FCSTD DOCUMENT  (FreeCAD 1.1R44795 (Git))
Label: Travel_buddy_V1.1
License: All rights reserved
LicenseURL: https://en.wikipedia.org/wiki/All_rights_reserved
objects: Part::Feature×201, Sketcher::SketchObject×50, App::Point×35, PartDesign::Pad×31, App::Part×21, PartDesign::Pocket×18, PartDesign::Body×14, PartDesign::Fillet×14, PartDesign::SubShapeBinder×8, PartDesign::Chamfer×6, PartDesign::Plane×3, PartDesign::LinearPattern×3, Spreadsheet::Sheet×1, PartDesign::Thickness×1, PartDesign::Revolution×1, PartDesign::Groove×1, PartDesign::FeatureBase×1, PartDesign::Boolean×1, Part::DatumPoint×1, Part::DatumPlane×1
note: 552 computed .brp shape members not serialized (recipe doc carries the construction recipe); baked Part::Feature solids carry a one-line shape summary decoded from their .brp

FEATURE [Part::Feature] Part__Feature003  label="FPC0_5K-DH-24PWB"
  Placement = pos=(129.7,-96.32,1.595) rot=(0,0,-1;1.5708rad)
  shape: bbox 5.251 x 15.51 x 3.201 mm, 2199 faces (baked)
FEATURE [Part::Feature] Part__Feature004  label="MESHTASTIC_REPEATER_HANDLE_1__1"
  shape: bbox 4.5 x 4.5 x 0.5047 mm, 32 faces (baked)
FEATURE [Part::Feature] Part__Feature005  label="MESHTASTIC_REPEATER_HANDLE_1__2"
  shape: bbox 6.901 x 4.502 x 3.811 mm, 367 faces (baked)
FEATURE [App::Part] MESHTASTIC_REPEATER_HANDLE_1_3__ASM
  Group = -> [Part__Feature004,Part__Feature005]
  Origin = -> Origin002
FEATURE [App::Part] TS4543TP_ASM
  Group = -> [MESHTASTIC_REPEATER_HANDLE_1_3__ASM]
  Origin = -> Origin003
  Placement = pos=(120.7,-117.2,1.595) rot=(0,0,-1;1.5708rad)
FEATURE [Part::Feature] Part__Feature009  label="FPC0_5K-DH-30PWB"
  Placement = pos=(112.1,-96.1,1.595) rot=(0,0,1;0rad)
  shape: bbox 18.51 x 5.251 x 3.201 mm, 2685 faces (baked)
FEATURE [Part::Feature] Part__Feature023  label="MESHTASTIC_REPEATER_HANDLE_1__3"
  shape: bbox 7.796 x 8.2 x 6.5 mm, 341 faces (baked)
FEATURE [Part::Feature] Part__Feature024  label="MESHTASTIC_REPEATER_HANDLE_1__4"
  shape: bbox 0.2041 x 0.1074 x 0.001 mm, 8 faces (baked)
FEATURE [Part::Feature] Part__Feature025  label="MESHTASTIC_REPEATER_HANDLE_1__5"
  shape: bbox 0.2106 x 0.1532 x 0.001 mm, 16 faces (baked)
FEATURE [Part::Feature] Part__Feature026  label="MESHTASTIC_REPEATER_HANDLE_1__6"
  shape: bbox 0.2041 x 0.1095 x 0.001 mm, 14 faces (baked)
FEATURE [Part::Feature] Part__Feature027  label="MESHTASTIC_REPEATER_HANDLE_1__7"
  shape: bbox 0.204 x 0.1665 x 0.001 mm, 16 faces (baked)
FEATURE [Part::Feature] Part__Feature028  label="MESHTASTIC_REPEATER_HANDLE_1__8"
  shape: bbox 0.2041 x 0.183 x 0.001 mm, 16 faces (baked)
FEATURE [Part::Feature] Part__Feature029  label="MESHTASTIC_REPEATER_HANDLE_1__9"
  shape: bbox 0.2041 x 0.1095 x 0.001 mm, 14 faces (baked)
FEATURE [Part::Feature] Part__Feature030  label="MESHTASTIC_REPEATER_HANDLE_1_10"
  shape: bbox 0.1522 x 0.1175 x 0.001 mm, 24 faces (baked)
FEATURE [Part::Feature] Part__Feature031  label="MESHTASTIC_REPEATER_HANDLE_1_11"
  shape: bbox 0.1521 x 0.09841 x 0.001 mm, 23 faces (baked)
FEATURE [Part::Feature] Part__Feature032  label="MESHTASTIC_REPEATER_HANDLE_1_12"
  shape: bbox 0.214 x 0.1394 x 0.001 mm, 17 faces (baked)
FEATURE [Part::Feature] Part__Feature033  label="MESHTASTIC_REPEATER_HANDLE_1_13"
  shape: bbox 0.2041 x 0.1095 x 0.001 mm, 14 faces (baked)
FEATURE [Part::Feature] Part__Feature034  label="MESHTASTIC_REPEATER_HANDLE_1_14"
  shape: bbox 0.204 x 0.1665 x 0.001 mm, 16 faces (baked)
FEATURE [Part::Feature] Part__Feature035  label="MESHTASTIC_REPEATER_HANDLE_1_15"
  shape: bbox 0.2041 x 0.183 x 0.001 mm, 16 faces (baked)
FEATURE [Part::Feature] Part__Feature036  label="MESHTASTIC_REPEATER_HANDLE_1_16"
  shape: bbox 0.6764 x 0.9228 x 0.00103 mm, 37 faces (baked)
FEATURE [App::Part] MESHTASTIC_REPEATER_HANDLE_1_21_ASM
  Group = -> [Part__Feature023,Part__Feature024,Part__Feature025,Part__Feature026,Part__Feature027,Part__Feature028,Part__Feature029,Part__Feature030,Part__Feature031,Part__Feature032,Part__Feature033,Part__Feature034,Part__Feature035,Part__Feature036]
  Origin = -> Origin004
FEATURE [App::Part] K1_5203UA_06_ASM  label="K1-5203UA-06_ASM"
  Group = -> [MESHTASTIC_REPEATER_HANDLE_1_21_ASM]
  Origin = -> Origin005
  Placement = pos=(131.8,-117.2,1.595) rot=(0,0,1;0.785398rad)
FEATURE [Part::Feature] Part__Feature038  label="MESHTASTIC_REPEATER_HANDLE_1_17"
  shape: bbox 9 x 3.5 x 2.5 mm, 44 faces (baked)
FEATURE [Part::Feature] Part__Feature039  label="MESHTASTIC_REPEATER_HANDLE_1_18"
  shape: bbox 9.002 x 7.602 x 6.602 mm, 126 faces (baked)
FEATURE [Part::Feature] Part__Feature040  label="MESHTASTIC_REPEATER_HANDLE_1_19"
  shape: bbox 0.1074 x 0.2041 x 0.001 mm, 8 faces (baked)
FEATURE [Part::Feature] Part__Feature041  label="MESHTASTIC_REPEATER_HANDLE_1_20"
  shape: bbox 0.1532 x 0.2106 x 0.001 mm, 16 faces (baked)
FEATURE [Part::Feature] Part__Feature042  label="MESHTASTIC_REPEATER_HANDLE_1_22"
  shape: bbox 0.1095 x 0.2041 x 0.001 mm, 14 faces (baked)
FEATURE [Part::Feature] Part__Feature043  label="MESHTASTIC_REPEATER_HANDLE_1_24"
  shape: bbox 0.1665 x 0.204 x 0.001 mm, 16 faces (baked)
FEATURE [Part::Feature] Part__Feature044  label="MESHTASTIC_REPEATER_HANDLE_1_25"
  shape: bbox 0.183 x 0.2041 x 0.001 mm, 16 faces (baked)
FEATURE [Part::Feature] Part__Feature045  label="MESHTASTIC_REPEATER_HANDLE_1_26"
  shape: bbox 0.1095 x 0.2041 x 0.001 mm, 14 faces (baked)
FEATURE [Part::Feature] Part__Feature046  label="MESHTASTIC_REPEATER_HANDLE_1_27"
  shape: bbox 0.1175 x 0.1522 x 0.001 mm, 24 faces (baked)
FEATURE [Part::Feature] Part__Feature047  label="MESHTASTIC_REPEATER_HANDLE_1_28"
  shape: bbox 0.09841 x 0.1521 x 0.001 mm, 23 faces (baked)
FEATURE [Part::Feature] Part__Feature048  label="MESHTASTIC_REPEATER_HANDLE_1_29"
  shape: bbox 0.1394 x 0.214 x 0.001 mm, 17 faces (baked)
FEATURE [Part::Feature] Part__Feature049  label="MESHTASTIC_REPEATER_HANDLE_1_30"
  shape: bbox 0.1095 x 0.2041 x 0.001 mm, 14 faces (baked)
FEATURE [Part::Feature] Part__Feature050  label="MESHTASTIC_REPEATER_HANDLE_1_31"
  shape: bbox 0.1665 x 0.204 x 0.001 mm, 16 faces (baked)
FEATURE [Part::Feature] Part__Feature051  label="MESHTASTIC_REPEATER_HANDLE_1_32"
  shape: bbox 0.183 x 0.2041 x 0.001 mm, 16 faces (baked)
FEATURE [Part::Feature] Part__Feature052  label="MESHTASTIC_REPEATER_HANDLE_1_33"
  shape: bbox 0.9228 x 0.6764 x 0.00103 mm, 37 faces (baked)
FEATURE [App::Part] MESHTASTIC_REPEATER_HANDLE_1_23_ASM
  Group = -> [Part__Feature038,Part__Feature039,Part__Feature040,Part__Feature041,Part__Feature042,Part__Feature043,Part__Feature044,Part__Feature045,Part__Feature046,Part__Feature047,Part__Feature048,Part__Feature049,Part__Feature050,Part__Feature051,Part__Feature052]
  Origin = -> Origin006
FEATURE [App::Part] SK_3245D_02_L4_ASM  label="SK-3245D-02-L4_ASM"
  Group = -> [MESHTASTIC_REPEATER_HANDLE_1_23_ASM]
  Origin = -> Origin007
  Placement = pos=(92.0567,-102.6,1.595) rot=(0,0,-1;1.5708rad)
FEATURE [Part::Feature] Part__Feature072  label="USB_C_RECEPTACLE_GCT_USB4105-_1"
  shape: bbox 0.25 x 2.4 x 0.1 mm, 6 faces (baked)
FEATURE [Part::Feature] Part__Feature073  label="USB_C_RECEPTACLE_GCT_USB4105-_2"
  shape: bbox 0.25 x 2.4 x 0.1 mm, 6 faces (baked)
FEATURE [Part::Feature] Part__Feature074  label="USB_C_RECEPTACLE_GCT_USB4105-_3"
  shape: bbox 0.25 x 1.9 x 0.1 mm, 6 faces (baked)
FEATURE [Part::Feature] Part__Feature075  label="USB_C_RECEPTACLE_GCT_USB4105-_4"
  shape: bbox 0.25 x 1.9 x 0.1 mm, 6 faces (baked)
FEATURE [Part::Feature] Part__Feature076  label="USB_C_RECEPTACLE_GCT_USB4105-_5"
  shape: bbox 0.25 x 2.4 x 0.1 mm, 6 faces (baked)
FEATURE [Part::Feature] Part__Feature077  label="USB_C_RECEPTACLE_GCT_USB4105-_6"
  shape: bbox 0.25 x 2.4 x 0.1 mm, 6 faces (baked)
FEATURE [Part::Feature] Part__Feature078  label="USB_C_RECEPTACLE_GCT_USB4105-_7"
  shape: bbox 0.25 x 1.9 x 0.1 mm, 6 faces (baked)
FEATURE [Part::Feature] Part__Feature079  label="USB_C_RECEPTACLE_GCT_USB4105-_8"
  shape: bbox 0.25 x 1.9 x 0.1 mm, 6 faces (baked)
FEATURE [Part::Feature] Part__Feature080  label="USB_C_RECEPTACLE_GCT_USB4105-_9"
  shape: bbox 4.45 x 7.05 x 3.59 mm, 69 faces (baked)
FEATURE [Part::Feature] Part__Feature081  label="USB_C_RECEPTACLE_GCT_USB4105_10"
  shape: bbox 0.2 x 0.8 x 0.12 mm, 6 faces (baked)
FEATURE [Part::Feature] Part__Feature082  label="USB_C_RECEPTACLE_GCT_USB4105_11"
  shape: bbox 0.2 x 0.8 x 0.12 mm, 6 faces (baked)
FEATURE [Part::Feature] Part__Feature083  label="USB_C_RECEPTACLE_GCT_USB4105_12"
  shape: bbox 0.2 x 0.8 x 0.12 mm, 6 faces (baked)
FEATURE [Part::Feature] Part__Feature084  label="USB_C_RECEPTACLE_GCT_USB4105_13"
  shape: bbox 0.2 x 0.8 x 0.12 mm, 6 faces (baked)
FEATURE [Part::Feature] Part__Feature085  label="USB_C_RECEPTACLE_GCT_USB4105_14"
  shape: bbox 0.2 x 0.8 x 0.12 mm, 6 faces (baked)
FEATURE [Part::Feature] Part__Feature086  label="USB_C_RECEPTACLE_GCT_USB4105_15"
  shape: bbox 0.2 x 0.8 x 0.12 mm, 6 faces (baked)
FEATURE [Part::Feature] Part__Feature087  label="USB_C_RECEPTACLE_GCT_USB4105_16"
  shape: bbox 0.2 x 0.8 x 0.12 mm, 6 faces (baked)
FEATURE [Part::Feature] Part__Feature088  label="USB_C_RECEPTACLE_GCT_USB4105_17"
  shape: bbox 0.2 x 0.8 x 0.12 mm, 6 faces (baked)
FEATURE [Part::Feature] Part__Feature089  label="USB_C_RECEPTACLE_GCT_USB4105_18"
  shape: bbox 4.47 x 7.33 x 4.26 mm, 161 faces (baked)
FEATURE [Part::Feature] Part__Feature090  label="USB_C_RECEPTACLE_GCT_USB4105_19"
  shape: bbox 0.25 x 2.4 x 0.1 mm, 6 faces (baked)
FEATURE [Part::Feature] Part__Feature091  label="USB_C_RECEPTACLE_GCT_USB4105_20"
  shape: bbox 0.25 x 2.4 x 0.1 mm, 6 faces (baked)
FEATURE [Part::Feature] Part__Feature092  label="USB_C_RECEPTACLE_GCT_USB4105_21"
  shape: bbox 0.25 x 1.9 x 0.1 mm, 6 faces (baked)
FEATURE [Part::Feature] Part__Feature093  label="USB_C_RECEPTACLE_GCT_USB4105_22"
  shape: bbox 0.25 x 1.9 x 0.1 mm, 6 faces (baked)
FEATURE [Part::Feature] Part__Feature094  label="USB_C_RECEPTACLE_GCT_USB4105_23"
  shape: bbox 0.25 x 2.4 x 0.1 mm, 6 faces (baked)
FEATURE [Part::Feature] Part__Feature095  label="USB_C_RECEPTACLE_GCT_USB4105_24"
  shape: bbox 0.25 x 2.4 x 0.1 mm, 6 faces (baked)
FEATURE [Part::Feature] Part__Feature096  label="USB_C_RECEPTACLE_GCT_USB4105_25"
  shape: bbox 0.25 x 1.9 x 0.1 mm, 6 faces (baked)
FEATURE [Part::Feature] Part__Feature097  label="USB_C_RECEPTACLE_GCT_USB4105_26"
  shape: bbox 0.25 x 1.9 x 0.1 mm, 6 faces (baked)
FEATURE [Part::Feature] Part__Feature098  label="USB_C_RECEPTACLE_GCT_USB4105_27"
  shape: bbox 4.45 x 7.05 x 3.59 mm, 69 faces (baked)
FEATURE [Part::Feature] Part__Feature099  label="USB_C_RECEPTACLE_GCT_USB4105_28"
  shape: bbox 0.2 x 0.8 x 0.12 mm, 6 faces (baked)
FEATURE [Part::Feature] Part__Feature100  label="USB_C_RECEPTACLE_GCT_USB4105_29"
  shape: bbox 0.2 x 0.8 x 0.12 mm, 6 faces (baked)
FEATURE [Part::Feature] Part__Feature101  label="USB_C_RECEPTACLE_GCT_USB4105_30"
  shape: bbox 0.2 x 0.8 x 0.12 mm, 6 faces (baked)
FEATURE [Part::Feature] Part__Feature102  label="USB_C_RECEPTACLE_GCT_USB4105_31"
  shape: bbox 0.2 x 0.8 x 0.12 mm, 6 faces (baked)
FEATURE [Part::Feature] Part__Feature103  label="USB_C_RECEPTACLE_GCT_USB4105_32"
  shape: bbox 0.2 x 0.8 x 0.12 mm, 6 faces (baked)
FEATURE [Part::Feature] Part__Feature104  label="USB_C_RECEPTACLE_GCT_USB4105_33"
  shape: bbox 0.2 x 0.8 x 0.12 mm, 6 faces (baked)
FEATURE [Part::Feature] Part__Feature105  label="USB_C_RECEPTACLE_GCT_USB4105_34"
  shape: bbox 0.2 x 0.8 x 0.12 mm, 6 faces (baked)
FEATURE [Part::Feature] Part__Feature106  label="USB_C_RECEPTACLE_GCT_USB4105_35"
  shape: bbox 0.2 x 0.8 x 0.12 mm, 6 faces (baked)
FEATURE [Part::Feature] Part__Feature107  label="USB_C_RECEPTACLE_GCT_USB4105_36"
  shape: bbox 4.47 x 7.33 x 4.26 mm, 161 faces (baked)
FEATURE [App::Part] USB_C_RECEPTACLE_GCT_USB4105_XX_ASM  label="USB_C_RECEPTACLE_GCT_USB4105-XX_ASM"
  Group = -> [Part__Feature072,Part__Feature073,Part__Feature074,Part__Feature075,Part__Feature076,Part__Feature077,Part__Feature078,Part__Feature079,Part__Feature080,Part__Feature081,Part__Feature082,Part__Feature083,Part__Feature084,Part__Feature085,Part__Feature086,Part__Feature087,Part__Feature088,Part__Feature089,Part__Feature090,Part__Feature091,Part__Feature092,Part__Feature093,Part__Feature094,+13 more]
  Origin = -> Origin009
  Placement = pos=(92.8,-116.7,1.595) rot=(0,0,-1;1.5708rad)
FEATURE [Part::Feature] Part__Feature108  label="S2B-PH-SM4-TB-2_0-BAT_1"
  shape: bbox 0.5 x 3.45 x 7.65 mm, 21 faces (baked)
FEATURE [Part::Feature] Part__Feature109  label="S2B-PH-SM4-TB-2_0-BAT_2"
  shape: bbox 0.5 x 3.45 x 7.65 mm, 21 faces (baked)
FEATURE [Part::Feature] Part__Feature110  label="S2B-PH-SM4-TB-2_0-BAT_3"
  shape: bbox 0.4 x 2.2 x 2.9 mm, 16 faces (baked)
FEATURE [Part::Feature] Part__Feature111  label="S2B-PH-SM4-TB-2_0-BAT_4"
  shape: bbox 7.9 x 5.5 x 7.6 mm, 88 faces (baked)
FEATURE [Part::Feature] Part__Feature112  label="S2B-PH-SM4-TB-2_0-BAT_5"
  shape: bbox 0.4 x 2.2 x 2.9 mm, 16 faces (baked)
FEATURE [App::Part] S2B_PH_SM4_TB_2_0_BAT_ASM  label="S2B-PH-SM4-TB-2_0-BAT_ASM"
  Group = -> [Part__Feature108,Part__Feature109,Part__Feature110,Part__Feature111,Part__Feature112]
  Origin = -> Origin010
  Placement = pos=(98.9,-131.3,1.595) rot=(1,0,0;1.5708rad)
FEATURE [Part::Feature] Part__Feature114  label="MESHTASTIC_REPEATER_HANDLE_1_34"
  shape: bbox 7 x 3.7 x 4.257 mm, 143 faces (baked)
FEATURE [Part::Feature] Part__Feature115  label="MESHTASTIC_REPEATER_HANDLE_1_35"
  shape: bbox 7.801 x 1.101 x 3.501 mm, 292 faces (baked)
FEATURE [App::Part] MESHTASTIC_REPEATER_HANDLE_1_43_ASM
  Group = -> [Part__Feature114,Part__Feature115]
  Origin = -> Origin011
FEATURE [App::Part] K2_1112SA_A4DW_01_ASM  label="K2-1112SA-A4DW-01_ASM"
  Group = -> [MESHTASTIC_REPEATER_HANDLE_1_43_ASM]
  Origin = -> Origin012
  Placement = pos=(91.735,-93,1.595) rot=(0,0,1;1.5708rad)
FEATURE [Part::Feature] Part__Feature118  label="320110032_GROVE--WOSHI"
  Placement = pos=(126.1,-130.939,1.595) rot=(0,0,-1;1.5708rad)
  shape: bbox 11.9 x 10.5 x 5.2 mm, 137 faces (baked)
FEATURE [Part::Feature] Part__Feature236  label="MESHTASTIC_REPEATER_HANDLE_1_036"
  shape: bbox 0.1522 x 0.1175 x 0.001 mm, 24 faces (baked)
FEATURE [App::Part] __25_2A_WT_ASM  label="1_25-2A-WT_ASM"
  Group = -> [Part__Feature236]
  Origin = -> Origin028
  Placement = pos=(98.9,-128.5,-0.085) rot=(0,1,0;3.14159rad)
FEATURE [Part::Feature] Part__Feature258  label="U_FL-R-SMT-1"
  Placement = pos=(155.43,-85.97,-22.585) rot=(0,0.707107,0.707107;3.14159rad)
  shape: bbox 3 x 3.1 x 1.254 mm, 59 faces (baked)
FEATURE [Part::Feature] Part__Feature318  label="MESHTASTIC_REPEATER_HANDLE_1_037"
  shape: bbox 9 x 3.5 x 2.5 mm, 44 faces (baked)
FEATURE [App::Part] MLT_8530_ASM  label="MLT-8530_ASM"
  Group = -> [Part__Feature318]
  Origin = -> Origin034
  Placement = pos=(132.4,-120.2,-0.085) rot=(0.707107,-0.707107,0;3.14159rad)
FEATURE [Part::Feature] Part__Feature343  label="MESHTASTIC_REPEATER_HAND-335774"
  shape: bbox 11.6 x 11 x 0.7984 mm, 32 faces (baked)
FEATURE [Part::Feature] Part__Feature344  label="MESHTASTIC_REPEATER_HAND-336798"
  shape: bbox 3.1 x 3 x 1.26 mm, 121 faces (baked)
FEATURE [Part::Feature] Part__Feature345  label="MESHTASTIC_REPEATER_HAND-340261"
  shape: bbox 11.3 x 10.1 x 2.15 mm, 59 faces (baked)
FEATURE [App::Part] WIO_SX1262_ASM  label="WIO-SX1262_ASM"
  Group = -> [Part__Feature343,Part__Feature344,Part__Feature345]
  Origin = -> Origin038
  Placement = pos=(115.729,-94.5,-0.085) rot=(1,0,0;3.14159rad)
FEATURE [Part::Feature] Part__Feature1355  label="MESHTASTIC_REPEATER_HANDLE_SILK"
  shape: bbox 48.07 x 52 x 1.66 mm, 604 faces, 0 solids (baked)
FEATURE [Part::Feature] Part__Feature1356  label="MESHTASTIC_REPEATER_HANDLE_PCB"
  shape: bbox 48.07 x 52 x 5.31 mm, 248 faces (baked)
FEATURE [App::Part] MESHTASTIC_REPEATER_HANDLE_1_ASM  label="Wio_tracker_L1-MinimalStep"
  Group = -> [Part__Feature003,TS4543TP_ASM,Part__Feature009,K1_5203UA_06_ASM,SK_3245D_02_L4_ASM,USB_C_RECEPTACLE_GCT_USB4105_XX_ASM,S2B_PH_SM4_TB_2_0_BAT_ASM,K2_1112SA_A4DW_01_ASM,Part__Feature118,__25_2A_WT_ASM,Part__Feature258,MLT_8530_ASM,WIO_SX1262_ASM,Part__Feature1355,Part__Feature1356]
  Origin = -> Origin052
  Placement = pos=(124.75,-5.55,-136.35) rot=(0,-0.707107,0.707107;3.14159rad)
FEATURE [Spreadsheet::Sheet] Spreadsheet
  cells = A1='General; C1='Solar panel; E1='GPS antenna; G1='Keypad; A2(Tolerance)=0.2; C2(Solar_panel_x)=69; E2(GPS_ant_Size)=15; G2(KPD_x_ofset)=6; A3(Wall)=1.5; C3(Solar_panel_y)=110; G3(KPD_y_ofset)=10; A4(Fillet)=2; A5(body_height)==17 + Wall; G5(KPD_x_grid)=20; G6(KPD_y_grid)=15; A7(twoM_holes_thread)=1.7; A8(threeM_holes_thread)=2.7; G8(KPD_tab_length)==KPD_x_grid - 7; A9(threeM_holes_slip_fit)=3.2; G9(KPD_tab_margin_sides)=1; G10(KPD_tab_margin_bottom)=1.5; A11(Mounting_height)==body_height - Wall; A15(EINKfoam)=2.7
FEATURE [Part::Feature] Part__Feature  label="Choc_V1"
  Placement = pos=(108.835,-85.6907,1.595) rot=(0,0,1;0rad)
  shape: bbox 15 x 15 x 11.08 mm, 495 faces, 5 solids (baked)
FEATURE [Part::Feature] Part__Feature1442  label="Choc_V002"
  Placement = pos=(90.8431,-85.6984,1.595) rot=(0,0,1;0rad)
  shape: bbox 15 x 15 x 11.08 mm, 495 faces, 5 solids (baked)
FEATURE [Part::Feature] Part__Feature1443  label="Choc_V003"
  Placement = pos=(72.8446,-102.701,1.595) rot=(0,0,1;0rad)
  shape: bbox 15 x 15 x 11.08 mm, 495 faces, 5 solids (baked)
FEATURE [Part::Feature] Part__Feature1444  label="Choc_V004"
  Placement = pos=(72.85,-68.7,1.595) rot=(0,0,1;0rad)
  shape: bbox 15 x 15 x 11.08 mm, 495 faces, 5 solids (baked)
FEATURE [Part::Feature] Part__Feature1445  label="PinHeader_1x03_P2.54mm_Vertical"
  Placement = pos=(133.2,-50.97,1.595) rot=(0,0,1;0rad)
  shape: bbox 2.54 x 7.62 x 11.54 mm, 76 faces (baked)
FEATURE [Part::Feature] Part__Feature1446  label="Choc_V005"
  Placement = pos=(72.8454,-85.7013,1.595) rot=(0,0,1;0rad)
  shape: bbox 15 x 15 x 11.08 mm, 495 faces, 5 solids (baked)
FEATURE [Part::Feature] Part__Feature1447  label="Choc_V006"
  Placement = pos=(90.8449,-102.697,1.595) rot=(0,0,1;0rad)
  shape: bbox 15 x 15 x 11.08 mm, 495 faces, 5 solids (baked)
FEATURE [Part::Feature] Part__Feature1448  label="Choc_V007"
  Placement = pos=(126.847,-85.6531,1.595) rot=(0,0,1;0rad)
  shape: bbox 15 x 15 x 11.08 mm, 495 faces, 5 solids (baked)
FEATURE [Part::Feature] Part__Feature1449  label="Choc_V008"
  Placement = pos=(126.864,-102.697,1.595) rot=(0,0,1;0rad)
  shape: bbox 15 x 15 x 11.08 mm, 495 faces, 5 solids (baked)
FEATURE [Part::Feature] Part__Feature1450  label="Choc_V009"
  Placement = pos=(126.849,-68.7,1.595) rot=(0,0,1;0rad)
  shape: bbox 15 x 15 x 11.08 mm, 495 faces, 5 solids (baked)
FEATURE [Part::Feature] Part__Feature1451  label="Choc_V010"
  Placement = pos=(108.843,-68.7,1.595) rot=(0,0,1;0rad)
  shape: bbox 15 x 15 x 11.08 mm, 495 faces, 5 solids (baked)
FEATURE [Part::Feature] Part__Feature1452  label="Choc_V011"
  Placement = pos=(90.8359,-68.7,1.595) rot=(0,0,1;0rad)
  shape: bbox 15 x 15 x 11.08 mm, 495 faces, 5 solids (baked)
FEATURE [Part::Feature] Part__Feature1453  label="Choc_V012"
  Placement = pos=(108.838,-102.697,1.595) rot=(0,0,1;0rad)
  shape: bbox 15 x 15 x 11.08 mm, 495 faces, 5 solids (baked)
FEATURE [Part::Feature] Part__Feature1454  label="C_0805_2012Metric"
  Placement = pos=(99.7,-53.45,-0.085) rot=(0.707107,-0.707107,0;3.14159rad)
  shape: bbox 1.25 x 2 x 1.25 mm, 28 faces (baked)
FEATURE [Part::Feature] Part__Feature1455  label="D_SOD-323"
  Placement = pos=(98.8,-82.95,-0.085) rot=(0.707107,-0.707107,0;3.14159rad)
  shape: bbox 1.25 x 2.5 x 1.11 mm, 59 faces (baked)
FEATURE [Part::Feature] Part__Feature1456  label="D_SOD-324"
  Placement = pos=(116.8,-65.95,-0.085) rot=(0.707107,-0.707107,0;3.14159rad)
  shape: bbox 1.25 x 2.5 x 1.11 mm, 59 faces (baked)
FEATURE [Part::Feature] Part__Feature1457  label="D_SOD-325"
  Placement = pos=(130.8,-79.55,-0.085) rot=(0,1,0;3.14159rad)
  shape: bbox 2.5 x 1.25 x 1.11 mm, 59 faces (baked)
FEATURE [Part::Feature] Part__Feature1458  label="D_SOD-326"
  Placement = pos=(116.816,-99.9438,-0.085) rot=(0.707107,-0.707107,0;3.14159rad)
  shape: bbox 1.25 x 2.5 x 1.11 mm, 59 faces (baked)
FEATURE [Part::Feature] Part__Feature1459  label="R_0805_2012Metric"
  Placement = pos=(129.499,-50.9679,-0.085) rot=(0,1,0;3.14159rad)
  shape: bbox 2 x 1.2 x 0.45 mm, 26 faces (baked)
FEATURE [Part::Feature] Part__Feature1460  label="D_SOD-327"
  Placement = pos=(130.813,-96.557,-0.085) rot=(0,1,0;3.14159rad)
  shape: bbox 2.5 x 1.25 x 1.11 mm, 59 faces (baked)
FEATURE [Part::Feature] Part__Feature1461  label="C_0805_2012Metric001"
  Placement = pos=(95.6851,-53.3637,-0.085) rot=(0.707107,0.707107,0;3.14159rad)
  shape: bbox 1.25 x 2 x 1.25 mm, 28 faces (baked)
FEATURE [Part::Feature] Part__Feature1462  label="C_0805_2012Metric002"
  Placement = pos=(90.3,-50.75,-0.085) rot=(0.707107,0.707107,0;3.14159rad)
  shape: bbox 1.25 x 2 x 1.25 mm, 28 faces (baked)
FEATURE [Part::Feature] Part__Feature1463  label="C_0805_2012Metric003"
  Placement = pos=(101.8,-53.45,-0.085) rot=(0.707107,-0.707107,0;3.14159rad)
  shape: bbox 1.25 x 2 x 1.25 mm, 28 faces (baked)
FEATURE [Part::Feature] Part__Feature1464  label="SOT-23"
  Placement = pos=(92.5,-53.35,-0.085) rot=(0,1,0;3.14159rad)
  shape: bbox 2.5 x 3 x 1.2 mm, 69 faces (baked)
FEATURE [Part::Feature] Part__Feature1465  label="R_0805_2012Metric001"
  Placement = pos=(129.5,-53.5112,-0.085) rot=(0,1,0;3.14159rad)
  shape: bbox 2 x 1.2 x 0.45 mm, 26 faces (baked)
FEATURE [Part::Feature] Part__Feature1466  label="D_SOD-328"
  Placement = pos=(80.8,-82.95,-0.085) rot=(0.707107,-0.707107,0;3.14159rad)
  shape: bbox 1.25 x 2.5 x 1.11 mm, 59 faces (baked)
FEATURE [Part::Feature] Part__Feature1467  label="JST_PH_S4B-PH-K_1x04_P2.00mm_Horizontal"
  Placement = pos=(75.3,-52.2,-0.085) rot=(1,0,0;3.14159rad)
  shape: bbox 9.9 x 7.6 x 8.25 mm, 174 faces (baked)
FEATURE [Part::Feature] Part__Feature1468  label="D_SOD-329"
  Placement = pos=(80.8,-99.95,-0.085) rot=(0.707107,-0.707107,0;3.14159rad)
  shape: bbox 1.25 x 2.5 x 1.11 mm, 59 faces (baked)
FEATURE [Part::Feature] Part__Feature1469  label="D_SOD-330"
  Placement = pos=(98.8,-99.95,-0.085) rot=(0.707107,-0.707107,0;3.14159rad)
  shape: bbox 1.25 x 2.5 x 1.11 mm, 59 faces (baked)
FEATURE [Part::Feature] Part__Feature1470  label="SOIC-20W_7.5x12.8mm_P1.27mm"
  Placement = pos=(109.7,-53.45,-0.085) rot=(0.707107,-0.707107,0;3.14159rad)
  shape: bbox 12.8 x 10.3 x 2.75 mm, 327 faces (baked)
FEATURE [Part::Feature] Part__Feature1471  label="D_SOD-331"
  Placement = pos=(116.8,-82.95,-0.085) rot=(0.707107,-0.707107,0;3.14159rad)
  shape: bbox 1.25 x 2.5 x 1.11 mm, 59 faces (baked)
FEATURE [Part::Feature] Part__Feature1472  label="D_SOD-332"
  Placement = pos=(98.8,-65.95,-0.085) rot=(0.707107,-0.707107,0;3.14159rad)
  shape: bbox 1.25 x 2.5 x 1.11 mm, 59 faces (baked)
FEATURE [Part::Feature] Part__Feature1473  label="D_SOD-333"
  Placement = pos=(130.8,-62.55,-0.085) rot=(0,1,0;3.14159rad)
  shape: bbox 2.5 x 1.25 x 1.11 mm, 59 faces (baked)
FEATURE [Part::Feature] Part__Feature1474  label="D_SOD-334"
  Placement = pos=(80.8,-65.95,-0.085) rot=(0.707107,-0.707107,0;3.14159rad)
  shape: bbox 1.25 x 2.5 x 1.11 mm, 59 faces (baked)
FEATURE [Part::Feature] Part__Feature1475  label="T9_keyboard_PCB"
  shape: bbox 70.5 x 65.3 x 1.51 mm, 85 faces (baked)
FEATURE [App::Part] T9_keyboard_1  label="T9_keyboard-Choco_switches-V0"
  Group = -> [Part__Feature,Part__Feature1442,Part__Feature1443,Part__Feature1444,Part__Feature1445,Part__Feature1446,Part__Feature1447,Part__Feature1448,Part__Feature1449,Part__Feature1450,Part__Feature1451,Part__Feature1452,Part__Feature1453,Part__Feature1454,Part__Feature1455,Part__Feature1456,Part__Feature1457,Part__Feature1458,Part__Feature1459,Part__Feature1460,Part__Feature1461,Part__Feature1462,+13 more]
  Origin = -> Origin068
  Placement = pos=(-99,-14.5,99.5) rot=(1,0,0;1.5708rad)
FEATURE [Sketcher::SketchObject] Sketch
  ArcFitTolerance = 1e-06
  AttachmentSupport = -> [XZ_Plane067]
  ExternalTypes = [0]
  FullyConstrained = true
  MakeInternals = false
  MapMode = 5
  Placement = pos=(0,0,0) rot=(1,0,0;1.5708rad)
  _ExternalGeoVersion = 0
  sketch-geometry (5):
    g0: LineSegment StartX=-34.5 StartY=-55 StartZ=0 EndX=34.5 EndY=-55 EndZ=0
    g1: LineSegment StartX=34.5 StartY=-55 StartZ=0 EndX=34.5 EndY=55 EndZ=0
    g2: LineSegment StartX=34.5 StartY=55 StartZ=0 EndX=-34.5 EndY=55 EndZ=0
    g3: LineSegment StartX=-34.5 StartY=55 StartZ=0 EndX=-34.5 EndY=-55 EndZ=0
    g4: GeomPoint [constr] X=0 Y=0 Z=0
  constraints (12):
    c: Coincident(g0,g1)
    c: Coincident(g1,g2)
    c: Coincident(g2,g3)
    c: Coincident(g3,g0)
    c: Horizontal(g0)
    c: Horizontal(g2)
    c: Vertical(g1)
    c: Vertical(g3)
    c: Symmetric(g2,g0,g4)
    c: Distance(g1,g3) = 69
    c: Distance(g0,g2) = 110
    c: Coincident(g4,g-1)
FEATURE [PartDesign::Pad] Pad
  Direction = (0,-1,2e-16)
  Length = 2.2
  Length2 = 10
  Placement = pos=(0,0,0) rot=(1,0,0;1.5708rad)
  Profile = -> Sketch
  ReferenceAxis = -> Sketch [N_Axis]
  Refine = true
  Reversed = true
  SideType = 0
  Suppressed = false
  Type = 0
  Type2 = 0
FEATURE [PartDesign::Body] Body  label="Solar_panel"
  AllowCompound = false
  Group = -> [Sketch,Pad]
  Origin = -> Origin
  Tip = -> Pad
FEATURE [Part::Feature] Part__Feature1476  label="D_SOD-335"
  Placement = pos=(165.1,-90,1.595) rot=(0,0,1;0rad)
  shape: bbox 2.5 x 1.25 x 1.11 mm, 59 faces (baked)
FEATURE [Part::Feature] Part__Feature1477  label="D_SOD-336"
  Placement = pos=(118.9,-130,1.595) rot=(0,0,1;3.14159rad)
  shape: bbox 2.5 x 1.25 x 1.11 mm, 59 faces (baked)
FEATURE [Part::Feature] Part__Feature1478  label="D_SOD-337"
  Placement = pos=(165.1,-130,1.595) rot=(0,0,1;0rad)
  shape: bbox 2.5 x 1.25 x 1.11 mm, 59 faces (baked)
FEATURE [Part::Feature] Part__Feature1479  label="C_0805_2012Metric004"
  Placement = pos=(145.7,-90.8,1.595) rot=(0,0,1;1.5708rad)
  shape: bbox 1.25 x 2 x 1.25 mm, 28 faces (baked)
FEATURE [Part::Feature] Part__Feature1480  label="SW_Push_1P1T_XKB_TS-1187A"
  Placement = pos=(122,-66,1.595) rot=(0,0,1;0rad)
  shape: bbox 6.5 x 5.1 x 1.4 mm, 132 faces, 10 solids (baked)
FEATURE [Part::Feature] Part__Feature1481  label="SW_Push_1P1T_XKB_TS-1187A001"
  Placement = pos=(142,-126,1.595) rot=(0,0,1;0rad)
  shape: bbox 6.5 x 5.1 x 1.4 mm, 132 faces, 10 solids (baked)
FEATURE [Part::Feature] Part__Feature1482  label="D_SOD-338"
  Placement = pos=(118.9,-110,1.595) rot=(0,0,1;3.14159rad)
  shape: bbox 2.5 x 1.25 x 1.11 mm, 59 faces (baked)
FEATURE [Part::Feature] Part__Feature1483  label="R_0805_2012Metric002"
  Placement = pos=(160.9,-97.2,1.595) rot=(0,0,1;3.14159rad)
  shape: bbox 2 x 1.2 x 0.45 mm, 26 faces (baked)
FEATURE [Part::Feature] Part__Feature1484  label="D_SOD-339"
  Placement = pos=(137.1,-88.45,1.595) rot=(0,0,-1;1.5708rad)
  shape: bbox 1.25 x 2.5 x 1.11 mm, 59 faces (baked)
FEATURE [Part::Feature] Part__Feature1485  label="D_SOD-340"
  Placement = pos=(136.9,-128.4,1.595) rot=(0,0,-1;1.5708rad)
  shape: bbox 1.25 x 2.5 x 1.11 mm, 59 faces (baked)
FEATURE [Part::Feature] Part__Feature1486  label="D_SOD-341"
  Placement = pos=(139,-70.6,1.595) rot=(0,0,-1;1.5708rad)
  shape: bbox 1.25 x 2.5 x 1.11 mm, 59 faces (baked)
FEATURE [Part::Feature] Part__Feature1487  label="SW_Push_1P1T_XKB_TS-1187A002"
  Placement = pos=(162,-106,1.595) rot=(0,0,1;0rad)
  shape: bbox 6.5 x 5.1 x 1.4 mm, 132 faces, 10 solids (baked)
FEATURE [Part::Feature] Part__Feature1488  label="SOT-024"
  Placement = pos=(151.7,-95.55,1.595) rot=(0,0,1;3.14159rad)
  shape: bbox 2.5 x 3 x 1.2 mm, 69 faces (baked)
FEATURE [Part::Feature] Part__Feature1489  label="D_SOD-342"
  Placement = pos=(139,-110.6,1.595) rot=(0,0,-1;1.5708rad)
  shape: bbox 1.25 x 2.5 x 1.11 mm, 59 faces (baked)
FEATURE [Part::Feature] Part__Feature1490  label="SW_Push_1P1T_XKB_TS-1187A003"
  Placement = pos=(122,-126,1.595) rot=(0,0,1;0rad)
  shape: bbox 6.5 x 5.1 x 1.4 mm, 132 faces, 10 solids (baked)
FEATURE [Part::Feature] Part__Feature1491  label="SW_Push_1P1T_XKB_TS-1187A004"
  Placement = pos=(122,-106,1.595) rot=(0,0,1;0rad)
  shape: bbox 6.5 x 5.1 x 1.4 mm, 132 faces, 10 solids (baked)
FEATURE [Part::Feature] Part__Feature1493  label="D_SOD-343"
  Placement = pos=(118.9,-90,1.595) rot=(0,0,1;3.14159rad)
  shape: bbox 2.5 x 1.25 x 1.11 mm, 59 faces (baked)
FEATURE [Part::Feature] Part__Feature1494  label="SW_Push_1P1T_XKB_TS-1187A005"
  Placement = pos=(142,-86,1.595) rot=(0,0,1;0rad)
  shape: bbox 6.5 x 5.1 x 1.4 mm, 132 faces, 10 solids (baked)
FEATURE [Part::Feature] Part__Feature1495  label="SW_Push_1P1T_XKB_TS-1187A006"
  Placement = pos=(122,-86,1.595) rot=(0,0,1;0rad)
  shape: bbox 6.5 x 5.1 x 1.4 mm, 132 faces, 10 solids (baked)
FEATURE [Part::Feature] Part__Feature1496  label="D_SOD-344"
  Placement = pos=(165.1,-70,1.595) rot=(0,0,1;0rad)
  shape: bbox 2.5 x 1.25 x 1.11 mm, 59 faces (baked)
FEATURE [Part::Feature] Part__Feature1497  label="C_0805_2012Metric005"
  Placement = pos=(147.7,-90.3,1.595) rot=(0,0,1;1.5708rad)
  shape: bbox 1.25 x 2 x 1.25 mm, 28 faces (baked)
FEATURE [Part::Feature] Part__Feature1498  label="D_SOD-345"
  Placement = pos=(118.9,-70,1.595) rot=(0,0,1;3.14159rad)
  shape: bbox 2.5 x 1.25 x 1.11 mm, 59 faces (baked)
FEATURE [Part::Feature] Part__Feature1499  label="SW_Push_1P1T_XKB_TS-1187A007"
  Placement = pos=(162,-66,1.595) rot=(0,0,1;0rad)
  shape: bbox 6.5 x 5.1 x 1.4 mm, 132 faces, 10 solids (baked)
FEATURE [Part::Feature] Part__Feature1500  label="C_0805_2012Metric006"
  Placement = pos=(151.6,-98.45,1.595) rot=(0,0,1;0rad)
  shape: bbox 2 x 1.25 x 1.25 mm, 28 faces (baked)
FEATURE [Part::Feature] Part__Feature1501  label="D_SOD-346"
  Placement = pos=(165.1,-110,1.595) rot=(0,0,1;0rad)
  shape: bbox 2.5 x 1.25 x 1.11 mm, 59 faces (baked)
FEATURE [Part::Feature] Part__Feature1502  label="SW_Push_1P1T_XKB_TS-1187A008"
  Placement = pos=(142,-66,1.595) rot=(0,0,1;0rad)
  shape: bbox 6.5 x 5.1 x 1.4 mm, 132 faces, 10 solids (baked)
FEATURE [Part::Feature] Part__Feature1503  label="C_0805_2012Metric007"
  Placement = pos=(154.8,-95.65,1.595) rot=(0,0,-1;1.5708rad)
  shape: bbox 1.25 x 2 x 1.25 mm, 28 faces (baked)
FEATURE [Part::Feature] Part__Feature1504  label="SW_Push_1P1T_XKB_TS-1187A009"
  Placement = pos=(162,-86,1.595) rot=(0,0,1;0rad)
  shape: bbox 6.5 x 5.1 x 1.4 mm, 132 faces, 10 solids (baked)
FEATURE [Part::Feature] Part__Feature1505  label="SW_Push_1P1T_XKB_TS-1187A010"
  Placement = pos=(162,-126,1.595) rot=(0,0,1;0rad)
  shape: bbox 6.5 x 5.1 x 1.4 mm, 132 faces, 10 solids (baked)
FEATURE [Part::Feature] Part__Feature1506  label="SW_Push_1P1T_XKB_TS-1187A011"
  Placement = pos=(142,-106,1.595) rot=(0,0,1;0rad)
  shape: bbox 6.5 x 5.1 x 1.4 mm, 132 faces, 10 solids (baked)
FEATURE [Part::Feature] Part__Feature1507  label="R_0805_2012Metric003"
  Placement = pos=(160.9,-95.1,1.595) rot=(0,0,1;3.14159rad)
  shape: bbox 2 x 1.2 x 0.45 mm, 26 faces (baked)
FEATURE [Part::Feature] Part__Feature1508  label="JST_PH_S4B-PH-K_1x04_P2.00mm_Horizontal001"
  Placement = pos=(146.6,-100.65,-0.085) rot=(1,0,0;3.14159rad)
  shape: bbox 9.9 x 7.6 x 8.25 mm, 174 faces (baked)
FEATURE [Part::Feature] Part__Feature1509  label="T9_keyboard_PCB001"
  shape: bbox 50.6 x 70 x 1.51 mm, 13 faces (baked)
FEATURE [App::Part] T9_keyboard_002  label="T9_keyboard-MicroSwitches-V1"
  Group = -> [Part__Feature1476,Part__Feature1477,Part__Feature1478,Part__Feature1479,Part__Feature1480,Part__Feature1481,Part__Feature1482,Part__Feature1483,Part__Feature1484,Part__Feature1485,Part__Feature1486,Part__Feature1487,Part__Feature1488,Part__Feature1489,Part__Feature1490,Part__Feature1491,Part__Feature1493,Part__Feature1494,Part__Feature1495,Part__Feature1496,Part__Feature1497,Part__Feature1498,+11 more]
  Origin = -> Origin069
  Placement = pos=(136,-13.05,-77) rot=(0,-0.707107,0.707107;3.14159rad)
FEATURE [Sketcher::SketchObject] Sketch007
  ArcFitTolerance = 1e-06
  AttachmentSupport = -> [XZ_Plane067]
  ExternalTypes = [0]
  FullyConstrained = true
  MakeInternals = false
  MapMode = 5
  Placement = pos=(0,0,0) rot=(1,0,0;1.5708rad)
  _ExternalGeoVersion = 0
  sketch-geometry (5):
    g0: LineSegment StartX=-17.25 StartY=-26.25 StartZ=0 EndX=17.25 EndY=-26.25 EndZ=0
    g1: LineSegment StartX=17.25 StartY=-26.25 StartZ=0 EndX=17.25 EndY=26.25 EndZ=0
    g2: LineSegment StartX=17.25 StartY=26.25 StartZ=0 EndX=-17.25 EndY=26.25 EndZ=0
    g3: LineSegment StartX=-17.25 StartY=26.25 StartZ=0 EndX=-17.25 EndY=-26.25 EndZ=0
    g4: GeomPoint [constr] X=0 Y=0 Z=0
  constraints (12):
    c: Coincident(g0,g1)
    c: Coincident(g1,g2)
    c: Coincident(g2,g3)
    c: Coincident(g3,g0)
    c: Horizontal(g0)
    c: Horizontal(g2)
    c: Vertical(g1)
    c: Vertical(g3)
    c: Symmetric(g2,g0,g4)
    c: Distance(g1,g3) = 34.5
    c: Distance(g0,g2) = 52.5
    c: Coincident(g4,g-1)
FEATURE [PartDesign::Pad] Pad006
  Direction = (0,-1,2e-16)
  Length = 10.3
  Length2 = 10
  Placement = pos=(0,0,0) rot=(1,0,0;1.5708rad)
  Profile = -> Sketch007
  ReferenceAxis = -> Sketch007 [N_Axis]
  Refine = true
  SideType = 0
  Suppressed = false
  Type = 0
  Type2 = 0
FEATURE [PartDesign::Body] Body003  label="Proposed Battery"
  AllowCompound = false
  Group = -> [Sketch007,Pad006]
  Origin = -> Origin073
  Placement = pos=(16.2,-1.65,27.1) rot=(0,-1,0;3.14159rad)
  Tip = -> Pad006
FEATURE [Sketcher::SketchObject] Sketch008
  ArcFitTolerance = 1e-06
  AttachmentSupport = -> [XZ_Plane067]
  ExternalTypes = [0]
  FullyConstrained = true
  MakeInternals = false
  MapMode = 5
  Placement = pos=(0,0,0) rot=(1,0,0;1.5708rad)
  _ExternalGeoVersion = 0
  sketch-geometry (5):
    g0: LineSegment StartX=-30 StartY=-25 StartZ=0 EndX=30 EndY=-25 EndZ=0
    g1: LineSegment StartX=30 StartY=-25 StartZ=0 EndX=30 EndY=25 EndZ=0
    g2: LineSegment StartX=30 StartY=25 StartZ=0 EndX=-30 EndY=25 EndZ=0
    g3: LineSegment StartX=-30 StartY=25 StartZ=0 EndX=-30 EndY=-25 EndZ=0
    g4: GeomPoint [constr] X=0 Y=0 Z=0
  constraints (12):
    c: Coincident(g0,g1)
    c: Coincident(g1,g2)
    c: Coincident(g2,g3)
    c: Coincident(g3,g0)
    c: Horizontal(g0)
    c: Horizontal(g2)
    c: Vertical(g1)
    c: Vertical(g3)
    c: Symmetric(g2,g0,g4)
    c: Distance(g1,g3) = 60
    c: Distance(g0,g2) = 50
    c: Coincident(g4,g-1)
FEATURE [PartDesign::Pad] Pad007
  Direction = (0,-1,2e-16)
  Length = 6
  Length2 = 10
  Placement = pos=(0,0,0) rot=(1,0,0;1.5708rad)
  Profile = -> Sketch008
  ReferenceAxis = -> Sketch008 [N_Axis]
  Refine = true
  SideType = 0
  Suppressed = false
  Type = 0
  Type2 = 0
FEATURE [PartDesign::Body] Body006  label="Battery 60x50x6-2.2Ah"
  AllowCompound = false
  Group = -> [Sketch008,Pad007]
  Origin = -> Origin076
  Placement = pos=(0,-1.5,29.4) rot=(0,0,1;0rad)
  Tip = -> Pad007
FEATURE [Sketcher::SketchObject] Sketch012
  ArcFitTolerance = 1e-06
  AttachmentSupport = -> [XZ_Plane067]
  ExternalTypes = [0]
  FullyConstrained = true
  MakeInternals = false
  MapMode = 5
  Placement = pos=(0,0,0) rot=(1,0,0;1.5708rad)
  _ExternalGeoVersion = 0
  expr: Constraints[9] = Spreadsheet.GPS_ant_Size
  sketch-geometry (5):
    g0: LineSegment StartX=-7.5 StartY=-7.5 StartZ=0 EndX=7.5 EndY=-7.5 EndZ=0
    g1: LineSegment StartX=7.5 StartY=-7.5 StartZ=0 EndX=7.5 EndY=7.5 EndZ=0
    g2: LineSegment StartX=7.5 StartY=7.5 StartZ=0 EndX=-7.5 EndY=7.5 EndZ=0
    g3: LineSegment StartX=-7.5 StartY=7.5 StartZ=0 EndX=-7.5 EndY=-7.5 EndZ=0
    g4: GeomPoint [constr] X=0 Y=0 Z=0
  constraints (12):
    c: Coincident(g0,g1)
    c: Coincident(g1,g2)
    c: Coincident(g2,g3)
    c: Coincident(g3,g0)
    c: Horizontal(g0)
    c: Horizontal(g2)
    c: Vertical(g1)
    c: Vertical(g3)
    c: Symmetric(g2,g0,g4)
    c: Distance(g1,g3) = 15
    c: Coincident(g4,g-1)
    c: Equal(g3,g0)
FEATURE [PartDesign::Pad] Pad009
  Direction = (0,-1,2e-16)
  Length = 4
  Length2 = 10
  Placement = pos=(0,0,0) rot=(1,0,0;1.5708rad)
  Profile = -> Sketch012
  ReferenceAxis = -> Sketch012 [N_Axis]
  Refine = true
  SideType = 0
  Suppressed = false
  Type = 0
  Type2 = 0
FEATURE [PartDesign::Body] Body004  label="GPS"
  AllowCompound = false
  Group = -> [Sketch012,Pad009]
  Origin = -> Origin074
  Placement = pos=(23.55,-9.05,-58.3) rot=(1,0,0;1.5708rad)
  Tip = -> Pad009
FEATURE [PartDesign::SubShapeBinder] Binder
  BindCopyOnChange = 0
  BindMode = 0
  ClaimChildren = false
  Context = -> Part002 [Part001.Body007.Binder.]
  Fuse = false
  MakeFace = true
  OffsetFill = false
  OffsetIntersection = false
  OffsetJoinType = 0
  OffsetOpenResult = false
  PartialLoad = false
  Refine = true
  Relative = true
  Support = -> [Body002]
  _Version = 2
FEATURE [Part::Feature] Part__Feature1510  label="D_SOD-347"
  Placement = pos=(165.1,-90,1.595) rot=(0,0,1;0rad)
  shape: bbox 2.5 x 1.25 x 1.11 mm, 59 faces (baked)
FEATURE [Part::Feature] Part__Feature1511  label="D_SOD-348"
  Placement = pos=(118.9,-130,1.595) rot=(0,0,1;3.14159rad)
  shape: bbox 2.5 x 1.25 x 1.11 mm, 59 faces (baked)
FEATURE [Part::Feature] Part__Feature1512  label="D_SOD-349"
  Placement = pos=(165.1,-130,1.595) rot=(0,0,1;0rad)
  shape: bbox 2.5 x 1.25 x 1.11 mm, 59 faces (baked)
FEATURE [Part::Feature] Part__Feature1513  label="C_0805_2012Metric008"
  Placement = pos=(145.7,-90.8,1.595) rot=(0,0,1;1.5708rad)
  shape: bbox 1.25 x 2 x 1.25 mm, 28 faces (baked)
FEATURE [Part::Feature] Part__Feature1514  label="SW_Push_1P1T_XKB_TS-1187A012"
  Placement = pos=(122,-66,1.595) rot=(0,0,1;0rad)
  shape: bbox 6.5 x 5.1 x 1.4 mm, 132 faces, 10 solids (baked)
FEATURE [Part::Feature] Part__Feature1515  label="SW_Push_1P1T_XKB_TS-1187A013"
  Placement = pos=(142,-126,1.595) rot=(0,0,1;0rad)
  shape: bbox 6.5 x 5.1 x 1.4 mm, 132 faces, 10 solids (baked)
FEATURE [Part::Feature] Part__Feature1516  label="D_SOD-350"
  Placement = pos=(118.9,-110,1.595) rot=(0,0,1;3.14159rad)
  shape: bbox 2.5 x 1.25 x 1.11 mm, 59 faces (baked)
FEATURE [Part::Feature] Part__Feature1517  label="R_0805_2012Metric004"
  Placement = pos=(160.9,-97.2,1.595) rot=(0,0,1;3.14159rad)
  shape: bbox 2 x 1.2 x 0.45 mm, 26 faces (baked)
FEATURE [Part::Feature] Part__Feature1518  label="D_SOD-351"
  Placement = pos=(137.1,-88.45,1.595) rot=(0,0,-1;1.5708rad)
  shape: bbox 1.25 x 2.5 x 1.11 mm, 59 faces (baked)
FEATURE [Part::Feature] Part__Feature1519  label="D_SOD-352"
  Placement = pos=(136.9,-128.4,1.595) rot=(0,0,-1;1.5708rad)
  shape: bbox 1.25 x 2.5 x 1.11 mm, 59 faces (baked)
FEATURE [Part::Feature] Part__Feature1520  label="D_SOD-353"
  Placement = pos=(139,-70.6,1.595) rot=(0,0,-1;1.5708rad)
  shape: bbox 1.25 x 2.5 x 1.11 mm, 59 faces (baked)
FEATURE [Part::Feature] Part__Feature1521  label="SW_Push_1P1T_XKB_TS-1187A014"
  Placement = pos=(162,-106,1.595) rot=(0,0,1;0rad)
  shape: bbox 6.5 x 5.1 x 1.4 mm, 132 faces, 10 solids (baked)
FEATURE [Part::Feature] Part__Feature1522  label="SOT-025"
  Placement = pos=(151.7,-95.55,1.595) rot=(0,0,1;3.14159rad)
  shape: bbox 2.5 x 3 x 1.2 mm, 69 faces (baked)
FEATURE [Part::Feature] Part__Feature1523  label="D_SOD-354"
  Placement = pos=(139,-110.6,1.595) rot=(0,0,-1;1.5708rad)
  shape: bbox 1.25 x 2.5 x 1.11 mm, 59 faces (baked)
FEATURE [Part::Feature] Part__Feature1524  label="SW_Push_1P1T_XKB_TS-1187A015"
  Placement = pos=(122,-126,1.595) rot=(0,0,1;0rad)
  shape: bbox 6.5 x 5.1 x 1.4 mm, 132 faces, 10 solids (baked)
FEATURE [Part::Feature] Part__Feature1525  label="SW_Push_1P1T_XKB_TS-1187A016"
  Placement = pos=(122,-106,1.595) rot=(0,0,1;0rad)
  shape: bbox 6.5 x 5.1 x 1.4 mm, 132 faces, 10 solids (baked)
FEATURE [Part::Feature] Part__Feature1526  label="PinHeader_1x03_P2.54mm_Vertical001"
  Placement = pos=(164.6,-94.66,1.595) rot=(0,0,1;0rad)
  shape: bbox 2.54 x 7.62 x 11.54 mm, 76 faces (baked)
FEATURE [Part::Feature] Part__Feature1527  label="D_SOD-355"
  Placement = pos=(118.9,-90,1.595) rot=(0,0,1;3.14159rad)
  shape: bbox 2.5 x 1.25 x 1.11 mm, 59 faces (baked)
FEATURE [Part::Feature] Part__Feature1528  label="SW_Push_1P1T_XKB_TS-1187A017"
  Placement = pos=(142,-86,1.595) rot=(0,0,1;0rad)
  shape: bbox 6.5 x 5.1 x 1.4 mm, 132 faces, 10 solids (baked)
FEATURE [Part::Feature] Part__Feature1529  label="SW_Push_1P1T_XKB_TS-1187A018"
  Placement = pos=(122,-86,1.595) rot=(0,0,1;0rad)
  shape: bbox 6.5 x 5.1 x 1.4 mm, 132 faces, 10 solids (baked)
FEATURE [Part::Feature] Part__Feature1530  label="D_SOD-356"
  Placement = pos=(165.1,-70,1.595) rot=(0,0,1;0rad)
  shape: bbox 2.5 x 1.25 x 1.11 mm, 59 faces (baked)
FEATURE [Part::Feature] Part__Feature1531  label="C_0805_2012Metric009"
  Placement = pos=(147.7,-90.3,1.595) rot=(0,0,1;1.5708rad)
  shape: bbox 1.25 x 2 x 1.25 mm, 28 faces (baked)
FEATURE [Part::Feature] Part__Feature1532  label="D_SOD-357"
  Placement = pos=(118.9,-70,1.595) rot=(0,0,1;3.14159rad)
  shape: bbox 2.5 x 1.25 x 1.11 mm, 59 faces (baked)
FEATURE [Part::Feature] Part__Feature1533  label="SW_Push_1P1T_XKB_TS-1187A019"
  Placement = pos=(162,-66,1.595) rot=(0,0,1;0rad)
  shape: bbox 6.5 x 5.1 x 1.4 mm, 132 faces, 10 solids (baked)
FEATURE [Part::Feature] Part__Feature1534  label="C_0805_2012Metric010"
  Placement = pos=(151.6,-98.45,1.595) rot=(0,0,1;0rad)
  shape: bbox 2 x 1.25 x 1.25 mm, 28 faces (baked)
FEATURE [Part::Feature] Part__Feature1535  label="D_SOD-358"
  Placement = pos=(165.1,-110,1.595) rot=(0,0,1;0rad)
  shape: bbox 2.5 x 1.25 x 1.11 mm, 59 faces (baked)
FEATURE [Part::Feature] Part__Feature1536  label="SW_Push_1P1T_XKB_TS-1187A020"
  Placement = pos=(142,-66,1.595) rot=(0,0,1;0rad)
  shape: bbox 6.5 x 5.1 x 1.4 mm, 132 faces, 10 solids (baked)
FEATURE [Part::Feature] Part__Feature1537  label="C_0805_2012Metric011"
  Placement = pos=(154.8,-95.65,1.595) rot=(0,0,-1;1.5708rad)
  shape: bbox 1.25 x 2 x 1.25 mm, 28 faces (baked)
FEATURE [Part::Feature] Part__Feature1538  label="SW_Push_1P1T_XKB_TS-1187A021"
  Placement = pos=(162,-86,1.595) rot=(0,0,1;0rad)
  shape: bbox 6.5 x 5.1 x 1.4 mm, 132 faces, 10 solids (baked)
FEATURE [Part::Feature] Part__Feature1539  label="SW_Push_1P1T_XKB_TS-1187A022"
  Placement = pos=(162,-126,1.595) rot=(0,0,1;0rad)
  shape: bbox 6.5 x 5.1 x 1.4 mm, 132 faces, 10 solids (baked)
FEATURE [Part::Feature] Part__Feature1540  label="SW_Push_1P1T_XKB_TS-1187A023"
  Placement = pos=(142,-106,1.595) rot=(0,0,1;0rad)
  shape: bbox 6.5 x 5.1 x 1.4 mm, 132 faces, 10 solids (baked)
FEATURE [Part::Feature] Part__Feature1541  label="R_0805_2012Metric005"
  Placement = pos=(160.9,-95.1,1.595) rot=(0,0,1;3.14159rad)
  shape: bbox 2 x 1.2 x 0.45 mm, 26 faces (baked)
FEATURE [Part::Feature] Part__Feature1542  label="JST_PH_S4B-PH-K_1x04_P2.00mm_Horizontal002"
  Placement = pos=(146.6,-100.65,-0.085) rot=(1,0,0;3.14159rad)
  shape: bbox 9.9 x 7.6 x 8.25 mm, 174 faces (baked)
FEATURE [Part::Feature] Part__Feature1543  label="T9_keyboard_PCB002"
  shape: bbox 65 x 71 x 1.51 mm, 21 faces (baked)
FEATURE [App::Part] T9_keyboard_003  label="T9_keyboard-MicroSwitches-V1.1"
  Group = -> [Part__Feature1510,Part__Feature1511,Part__Feature1512,Part__Feature1513,Part__Feature1514,Part__Feature1515,Part__Feature1516,Part__Feature1517,Part__Feature1518,Part__Feature1519,Part__Feature1520,Part__Feature1521,Part__Feature1522,Part__Feature1523,Part__Feature1524,Part__Feature1525,Part__Feature1526,Part__Feature1527,Part__Feature1528,Part__Feature1529,Part__Feature1530,Part__Feature1531,+12 more]
  Origin = -> Origin078
  Placement = pos=(134.55,-13,-87.8) rot=(0,-0.707107,0.707107;3.14159rad)
FEATURE [Part::Feature] Part__Feature1544  label="SW_Push_1P1T_XKB_TS-1187A024"
  Placement = pos=(122,-66,1.595) rot=(0,0,1;0rad)
  shape: bbox 6.5 x 5.1 x 1.4 mm, 132 faces, 10 solids (baked)
FEATURE [Part::Feature] Part__Feature1545  label="SW_Push_1P1T_XKB_TS-1187A025"
  Placement = pos=(142,-111,1.595) rot=(0,0,1;0rad)
  shape: bbox 6.5 x 5.1 x 1.4 mm, 132 faces, 10 solids (baked)
FEATURE [Part::Feature] Part__Feature1546  label="SW_Push_1P1T_XKB_TS-1187A026"
  Placement = pos=(162,-96,1.595) rot=(0,0,1;0rad)
  shape: bbox 6.5 x 5.1 x 1.4 mm, 132 faces, 10 solids (baked)
FEATURE [Part::Feature] Part__Feature1547  label="SW_Push_1P1T_XKB_TS-1187A027"
  Placement = pos=(122,-111,1.595) rot=(0,0,1;0rad)
  shape: bbox 6.5 x 5.1 x 1.4 mm, 132 faces, 10 solids (baked)
FEATURE [Part::Feature] Part__Feature1548  label="SW_Push_1P1T_XKB_TS-1187A028"
  Placement = pos=(122,-96,1.595) rot=(0,0,1;0rad)
  shape: bbox 6.5 x 5.1 x 1.4 mm, 132 faces, 10 solids (baked)
FEATURE [Part::Feature] Part__Feature1549  label="SW_Push_1P1T_XKB_TS-1187A029"
  Placement = pos=(142,-81,1.595) rot=(0,0,1;0rad)
  shape: bbox 6.5 x 5.1 x 1.4 mm, 132 faces, 10 solids (baked)
FEATURE [Part::Feature] Part__Feature1550  label="SW_Push_1P1T_XKB_TS-1187A030"
  Placement = pos=(122,-81,1.595) rot=(0,0,1;0rad)
  shape: bbox 6.5 x 5.1 x 1.4 mm, 132 faces, 10 solids (baked)
FEATURE [Part::Feature] Part__Feature1551  label="SW_Push_1P1T_XKB_TS-1187A031"
  Placement = pos=(162,-66,1.595) rot=(0,0,1;0rad)
  shape: bbox 6.5 x 5.1 x 1.4 mm, 132 faces, 10 solids (baked)
FEATURE [Part::Feature] Part__Feature1552  label="SW_Push_1P1T_XKB_TS-1187A032"
  Placement = pos=(142,-66,1.595) rot=(0,0,1;0rad)
  shape: bbox 6.5 x 5.1 x 1.4 mm, 132 faces, 10 solids (baked)
FEATURE [Part::Feature] Part__Feature1553  label="SW_Push_1P1T_XKB_TS-1187A033"
  Placement = pos=(162,-81,1.595) rot=(0,0,1;0rad)
  shape: bbox 6.5 x 5.1 x 1.4 mm, 132 faces, 10 solids (baked)
FEATURE [Part::Feature] Part__Feature1554  label="SW_Push_1P1T_XKB_TS-1187A034"
  Placement = pos=(162,-111,1.595) rot=(0,0,1;0rad)
  shape: bbox 6.5 x 5.1 x 1.4 mm, 132 faces, 10 solids (baked)
FEATURE [Part::Feature] Part__Feature1555  label="SW_Push_1P1T_XKB_TS-1187A035"
  Placement = pos=(142,-96,1.595) rot=(0,0,1;0rad)
  shape: bbox 6.5 x 5.1 x 1.4 mm, 132 faces, 10 solids (baked)
FEATURE [Part::Feature] Part__Feature1556  label="T9_keyboard_PCB003"
  shape: bbox 60 x 55 x 1.51 mm, 15 faces (baked)
FEATURE [App::Part] T9_keyboard_004  label="T9_keyboard-MicroSwitches-V1.2"
  Group = -> [Part__Feature1544,Part__Feature1545,Part__Feature1546,Part__Feature1547,Part__Feature1548,Part__Feature1549,Part__Feature1550,Part__Feature1551,Part__Feature1552,Part__Feature1553,Part__Feature1554,Part__Feature1555,Part__Feature1556]
  Origin = -> Origin079
  Placement = pos=(135.5,-13.5,-70.05) rot=(0,0.707107,-0.707107;3.14159rad)
FEATURE [Sketcher::SketchObject] Sketch018
  ArcFitTolerance = 1e-06
  AttachmentSupport = -> [XZ_Plane067]
  ExternalTypes = [0]
  FullyConstrained = true
  MakeInternals = false
  MapMode = 5
  Placement = pos=(0,0,0) rot=(1,0,0;1.5708rad)
  _ExternalGeoVersion = 0
  sketch-geometry (5):
    g0: LineSegment StartX=-14.6 StartY=-29.6 StartZ=0 EndX=14.6 EndY=-29.6 EndZ=0
    g1: LineSegment StartX=14.6 StartY=-29.6 StartZ=0 EndX=14.6 EndY=29.6 EndZ=0
    g2: LineSegment StartX=14.6 StartY=29.6 StartZ=0 EndX=-14.6 EndY=29.6 EndZ=0
    g3: LineSegment StartX=-14.6 StartY=29.6 StartZ=0 EndX=-14.6 EndY=-29.6 EndZ=0
    g4: GeomPoint [constr] X=0 Y=0 Z=0
  constraints (12):
    c: Coincident(g0,g1)
    c: Coincident(g1,g2)
    c: Coincident(g2,g3)
    c: Coincident(g3,g0)
    c: Horizontal(g0)
    c: Horizontal(g2)
    c: Vertical(g1)
    c: Vertical(g3)
    c: Symmetric(g2,g0,g4)
    c: Coincident(g4,g-1)
    c: DistanceX(g2,g2) = 29.2
    c: DistanceY(g3,g3) = 59.2
FEATURE [PartDesign::Pad] Pad014
  Direction = (0,-1,2e-16)
  Length = 1
  Length2 = 10
  Placement = pos=(0,0,0) rot=(1,0,0;1.5708rad)
  Profile = -> Sketch018
  ReferenceAxis = -> Sketch018 [N_Axis]
  Refine = true
  SideType = 0
  Suppressed = false
  Type = 0
  Type2 = 0
FEATURE [PartDesign::Body] Body005  label="E-ink"
  AllowCompound = false
  Group = -> [Sketch018,Pad014]
  Origin = -> Origin075
  Placement = pos=(-2.6,-17.4,-39.9) rot=(0,1,0;4.71239rad)
  Tip = -> Pad014
FEATURE [Part::Feature] Part__Feature1557  label="ON-OFF button"
  Placement = pos=(35.8,-8.9,-34.5) rot=(-0.57735,-0.57735,0.57735;4.18879rad)
  shape: bbox 4.5 x 6 x 10.7 mm, 34 faces (baked)
FEATURE [Sketcher::SketchObject] Sketch023
  ArcFitTolerance = 1e-06
  ExternalTypes = [0]
  FullyConstrained = true
  MakeInternals = false
  MapMode = 5
  Placement = pos=(0,-20,4.5e-15) rot=(1,0,0;1.5708rad)
  _ExternalGeoVersion = 0
  sketch-geometry (5):
    g0: Circle CenterX=4.05 CenterY=-19.15 CenterZ=0 NormalX=0 NormalY=0 NormalZ=1 AngleXU=0 Radius=3.5
    g1: LineSegment [constr] StartX=4.05 StartY=-19.15 StartZ=0 EndX=37.5 EndY=-19.15 EndZ=0
    g2: GeomPoint [constr] X=37.5 Y=-19.65 Z=0
    g3: LineSegment [constr] StartX=4.05 StartY=-19.15 StartZ=0 EndX=-7.05 EndY=-19.15 EndZ=0
    g4: Circle CenterX=-7.05 CenterY=-19.15 CenterZ=0 NormalX=0 NormalY=0 NormalZ=1 AngleXU=0 Radius=3.75
  constraints (12):
    c: Diameter(g0) = 7
    c: Coincident(g1,g0)
    c: PointOnObject(g1,g-3)
    c: Horizontal(g1)
    c: Symmetric(g-3,g-3,g2)
    c: DistanceY(g2,g1) = 0.5
    c: DistanceX(g0,g-3) = 33.45
    c: Coincident(g3,g0)
    c: Horizontal(g3)
    c: Coincident(g4,g3)
    c: DistanceX(g3,g0) = 11.1
    c: Diameter(g4) = 7.5
FEATURE [PartDesign::SubShapeBinder] Binder001
  BindCopyOnChange = 0
  BindMode = 0
  ClaimChildren = false
  Context = -> Part002 [Part001.Body007.Binder001.]
  Fuse = false
  MakeFace = true
  OffsetFill = false
  OffsetIntersection = false
  OffsetJoinType = 0
  OffsetOpenResult = false
  PartialLoad = false
  Refine = true
  Relative = true
  Support = -> [Body002]
  _Version = 2
FEATURE [PartDesign::SubShapeBinder] Binder002
  BindCopyOnChange = 0
  BindMode = 0
  ClaimChildren = false
  Context = -> Part002 [Part001.Body008.Binder002.]
  Fuse = false
  MakeFace = true
  OffsetFill = false
  OffsetIntersection = false
  OffsetJoinType = 0
  OffsetOpenResult = false
  PartialLoad = false
  Refine = true
  Relative = true
  Support = -> [Body007[Pocket006.,Pocket006.]]
  _Version = 2
FEATURE [PartDesign::SubShapeBinder] Binder003
  BindCopyOnChange = 0
  BindMode = 0
  ClaimChildren = false
  Context = -> Part002 [Part001.Body009.Binder003.]
  Fuse = false
  MakeFace = true
  OffsetFill = false
  OffsetIntersection = false
  OffsetJoinType = 0
  OffsetOpenResult = false
  PartialLoad = false
  Refine = true
  Relative = true
  Support = -> [Body007[Pocket006.]]
  _Version = 2
FEATURE [Sketcher::SketchObject] Sketch032
  ArcFitTolerance = 1e-06
  ExternalTypes = [0]
  FullyConstrained = true
  MakeInternals = false
  MapMode = 5
  Placement = pos=(-3.3,-10.5,-19.15) rot=(-1,0,0;1.5708rad)
  _ExternalGeoVersion = 0
  expr: Constraints[13] = 1.9 + Spreadsheet.Tolerance / 2
  sketch-geometry (5):
    g0: LineSegment StartX=-3.75 StartY=1.41421 StartZ=0 EndX=-5.16421 EndY=0 EndZ=0
    g1: LineSegment StartX=-5.16421 StartY=0 StartZ=0 EndX=-3.75 EndY=-1.41421 EndZ=0
    g2: LineSegment StartX=-3.75 StartY=-1.41421 StartZ=0 EndX=-2.33579 EndY=7.1e-15 EndZ=0
    g3: LineSegment StartX=-2.33579 StartY=7.1e-15 StartZ=0 EndX=-3.75 EndY=1.41421 EndZ=0
    g4: Circle [constr] CenterX=-3.75 CenterY=3.6e-15 CenterZ=0 NormalX=0 NormalY=0 NormalZ=1 AngleXU=0 Radius=1.41421
  constraints (14):
    c: Coincident(g0,g1)
    c: Coincident(g1,g2)
    c: Coincident(g2,g3)
    c: Coincident(g3,g0)
    c: Equal(g0,g1)
    c: Equal(g0,g2)
    c: Equal(g0,g3)
    c: PointOnObject(g0,g4)
    c: PointOnObject(g1,g4)
    c: PointOnObject(g2,g4)
    c: PointOnObject(g3,g4)
    c: Coincident(g4,g-3)
    c: PointOnObject(g0,g-1)
    c: Distance(g0,g0) = 2
FEATURE [Sketcher::SketchObject] Sketch039
  ArcFitTolerance = 1e-06
  ExternalTypes = [0]
  FullyConstrained = true
  MakeInternals = false
  MapMode = 5
  Placement = pos=(0,-17.2,4.5e-15) rot=(1,0,0;1.5708rad)
  _ExternalGeoVersion = 0
  sketch-geometry (6):
    g0: LineSegment StartX=22.2142 StartY=-55.08 StartZ=0 EndX=27.8 EndY=-55.08 EndZ=0
    g1: LineSegment StartX=27.8 StartY=-55.08 StartZ=0 EndX=27.8 EndY=-49.4942 EndZ=0
    g2: LineSegment StartX=27.8 StartY=-49.4942 StartZ=0 EndX=22.2142 EndY=-55.08 EndZ=0
    g3: LineSegment StartX=27.8 StartY=-24.71 StartZ=0 EndX=22.2142 EndY=-24.71 EndZ=0
    g4: LineSegment StartX=22.2142 StartY=-24.71 StartZ=0 EndX=27.8 EndY=-30.2958 EndZ=0
    g5: LineSegment StartX=27.8 StartY=-30.2958 StartZ=0 EndX=27.8 EndY=-24.71 EndZ=0
  constraints (16):
    c: Horizontal(g0)
    c: Coincident(g0,g1)
    c: Vertical(g1)
    c: Coincident(g1,g2)
    c: Coincident(g2,g0)
    c: Parallel(g-4,g2)
    c: Coincident(g0,g-8)
    c: Distance(g-4,g2) = 1
    c: Coincident(g-6,g3)
    c: PointOnObject(g3,g-5)
    c: Coincident(g3,g4)
    c: PointOnObject(g4,g-6)
    c: Coincident(g4,g5)
    c: Coincident(g5,g3)
    c: Parallel(g-3,g4)
    c: Distance(g-3,g4) = 1
FEATURE [PartDesign::SubShapeBinder] Binder005
  BindCopyOnChange = 0
  BindMode = 0
  ClaimChildren = false
  Context = -> Part002 [Part001.Body007.Binder005.]
  Fuse = false
  MakeFace = true
  OffsetFill = false
  OffsetIntersection = false
  OffsetJoinType = 0
  OffsetOpenResult = false
  PartialLoad = false
  Refine = true
  Relative = true
  Support = -> [Body002]
  _Version = 2
FEATURE [PartDesign::SubShapeBinder] Binder006
  BindCopyOnChange = 0
  BindMode = 0
  ClaimChildren = false
  Context = -> Part001 [Group001.Body010.Binder006.]
  Fuse = false
  MakeFace = true
  OffsetFill = false
  OffsetIntersection = false
  OffsetJoinType = 0
  OffsetOpenResult = false
  PartialLoad = false
  Refine = true
  Relative = true
  Support = -> [Body002]
  _Version = 2
FEATURE [Sketcher::SketchObject] Sketch042
  ArcFitTolerance = 1e-06
  AttachmentSupport = -> [XZ_Plane071]
  ExternalGeometry = -> [Binder006]
  ExternalTypes = [0]
  FullyConstrained = true
  MakeInternals = false
  MapMode = 5
  Placement = pos=(0,0,0) rot=(1,0,0;1.5708rad)
  _ExternalGeoVersion = 0
  expr: Constraints[13] = Spreadsheet.Wall
  sketch-geometry (23):
    g0: ArcOfCircle CenterX=-35.5 CenterY=56 CenterZ=0 NormalX=0 NormalY=0 NormalZ=1 AngleXU=0 Radius=3.5 StartAngle=1.5708 EndAngle=3.14159
    g1: ArcOfCircle CenterX=35.5 CenterY=56 CenterZ=0 NormalX=0 NormalY=0 NormalZ=1 AngleXU=0 Radius=3.5 StartAngle=0 EndAngle=1.5708
    g2: LineSegment StartX=-35.5 StartY=59.5 StartZ=0 EndX=35.5 EndY=59.5 EndZ=0
    g3: LineSegment StartX=-39 StartY=56 StartZ=0 EndX=-39 EndY=-56 EndZ=0
    g4: ArcOfCircle CenterX=-35.5 CenterY=-56 CenterZ=0 NormalX=0 NormalY=0 NormalZ=1 AngleXU=0 Radius=3.5 StartAngle=3.14159 EndAngle=4.71239
    g5: ArcOfCircle CenterX=33.5 CenterY=-60.5 CenterZ=0 NormalX=0 NormalY=0 NormalZ=1 AngleXU=0 Radius=5.5 StartAngle=4.71239 EndAngle=6.28319
    g6: LineSegment StartX=39 StartY=56 StartZ=0 EndX=39 EndY=-60.5 EndZ=0
    g7: LineSegment StartX=-35.5 StartY=-59.5 StartZ=0 EndX=6.51788 EndY=-59.5 EndZ=0
    g8: LineSegment StartX=33.5 StartY=-66 StartZ=0 EndX=13.5 EndY=-66 EndZ=0
    g9: ArcOfCircle CenterX=13.5 CenterY=-60.5 CenterZ=0 NormalX=0 NormalY=0 NormalZ=1 AngleXU=0 Radius=5.5 StartAngle=3.21308 EndAngle=4.71239
    g10: ArcOfCircle CenterX=6.51788 CenterY=-61 CenterZ=0 NormalX=0 NormalY=0 NormalZ=1 AngleXU=0 Radius=1.5 StartAngle=0.0714894 EndAngle=1.5708
    g11: LineSegment StartX=-37.5 StartY=56 StartZ=0 EndX=-37.5 EndY=-56 EndZ=0
    g12: LineSegment StartX=-35.5 StartY=-58 StartZ=0 EndX=8 EndY=-58 EndZ=0
    g13: LineSegment StartX=9.5 StartY=-59.5 StartZ=0 EndX=9.5 EndY=-60.5 EndZ=0
    g14: LineSegment StartX=13.5 StartY=-64.5 StartZ=0 EndX=33.5 EndY=-64.5 EndZ=0
    g15: LineSegment StartX=37.5 StartY=-60.5 StartZ=0 EndX=37.5 EndY=56 EndZ=0
    g16: LineSegment StartX=35.5 StartY=58 StartZ=0 EndX=-35.5 EndY=58 EndZ=0
    g17: ArcOfCircle CenterX=-35.5 CenterY=56 CenterZ=0 NormalX=0 NormalY=0 NormalZ=1 AngleXU=0 Radius=2.00001 StartAngle=1.5708 EndAngle=3.14159
    g18: ArcOfCircle CenterX=35.5 CenterY=56 CenterZ=0 NormalX=0 NormalY=0 NormalZ=1 AngleXU=0 Radius=1.99999 StartAngle=6.28318 EndAngle=7.85399
    g19: ArcOfCircle CenterX=33.5 CenterY=-60.5 CenterZ=0 NormalX=0 NormalY=0 NormalZ=1 AngleXU=0 Radius=3.99999 StartAngle=4.71239 EndAngle=6.28319
    g20: ArcOfCircle CenterX=13.5 CenterY=-60.5 CenterZ=0 NormalX=0 NormalY=0 NormalZ=1 AngleXU=0 Radius=4.00001 StartAngle=3.14159 EndAngle=4.71239
    g21: ArcOfCircle CenterX=7.99999 CenterY=-59.5 CenterZ=0 NormalX=0 NormalY=0 NormalZ=1 AngleXU=0 Radius=1.50001 StartAngle=4.85905e-06 EndAngle=1.57079
    g22: ArcOfCircle CenterX=-35.5 CenterY=-56 CenterZ=0 NormalX=0 NormalY=0 NormalZ=1 AngleXU=0 Radius=2.00001 StartAngle=3.1416 EndAngle=4.71239
  constraints (53):
    c: Coincident(g0,g-4)
    c: Coincident(g1,g-6)
    c: Horizontal(g2)
    c: Tangent(g2,g0) = 1.5708
    c: Tangent(g2,g1) = 1.5708
    c: Vertical(g3)
    c: Coincident(g4,g-12)
    c: Coincident(g5,g-9)
    c: Vertical(g6)
    c: Tangent(g4,g3) = -1.5708
    c: Tangent(g6,g5) = 1.5708
    c: Tangent(g6,g1) = 1.5708
    c: Tangent(g3,g0) = -1.5708
    c: DistanceY(g-6,g1) = 1.5
    c: Horizontal(g7)
    c: Horizontal(g8)
    c: Coincident(g9,g-10)
    c: Tangent(g10,g7) = 1.5708
    c: Tangent(g9,g8) = 1.5708
    c: Tangent(g8,g5) = 1.5708
    c: Tangent(g7,g4) = -1.5708
    c: Tangent(g10,g9) = 1.5708
    c: Equal(g10,g-13)
    c: Coincident(g-4,g16)
    c: Coincident(g-6,g16)
    c: Coincident(g15,g-7)
    c: Coincident(g15,g-9)
    c: Coincident(g14,g-9)
    c: Coincident(g-10,g14)
    c: Coincident(g-14,g13)
    c: Coincident(g13,g-14)
    c: Coincident(g-13,g12)
    c: Coincident(g-12,g12)
    c: Coincident(g-12,g11)
    c: Coincident(g11,g-5)
    c: Coincident(g17,g11)
    c: Coincident(g17,g16)
    c: Coincident(g18,g16)
    c: Coincident(g18,g15)
    c: Coincident(g19,g15)
    c: Coincident(g19,g14)
    c: Coincident(g20,g14)
    c: Coincident(g20,g13)
    c: Coincident(g21,g13)
    c: Coincident(g21,g12)
    c: Coincident(g22,g12)
    c: Coincident(g22,g11)
    c: Tangent(g-4,g17)
    c: Tangent(g-6,g18)
    c: Tangent(g-9,g19)
    c: Tangent(g-10,g20)
    c: Tangent(g21,g-13)
    c: Tangent(g-12,g22)
FEATURE [PartDesign::Pad] Pad024
  Direction = (0,-1,2e-16)
  Length = 20
  Length2 = 10
  Placement = pos=(0,0,0) rot=(1,0,0;1.5708rad)
  Profile = -> Sketch042
  ReferenceAxis = -> Sketch042 [N_Axis]
  Refine = true
  SideType = 0
  Suppressed = false
  Type = 0
  Type2 = 0
  expr: Length = Spreadsheet.body_height + Spreadsheet.Wall
FEATURE [Sketcher::SketchObject] Sketch004
  ArcFitTolerance = 1e-06
  AttachmentSupport = -> [XZ_Plane067]
  ExternalTypes = [0]
  FullyConstrained = true
  MakeInternals = false
  MapMode = 5
  Placement = pos=(0,0,0) rot=(1,0,0;1.5708rad)
  _ExternalGeoVersion = 0
  expr: Constraints[11] = Spreadsheet.Solar_panel_x
  expr: Constraints[40] = Spreadsheet.Fillet
  expr: Constraints[51] = 5 + Spreadsheet.Wall
  sketch-geometry (24):
    g0: LineSegment [constr] StartX=-34.5 StartY=-55 StartZ=0 EndX=34.5 EndY=-55 EndZ=0
    g1: LineSegment [constr] StartX=34.5 StartY=-55 StartZ=0 EndX=34.5 EndY=55 EndZ=0
    g2: LineSegment [constr] StartX=34.5 StartY=55 StartZ=0 EndX=-34.5 EndY=55 EndZ=0
    g3: LineSegment [constr] StartX=-34.5 StartY=55 StartZ=0 EndX=-34.5 EndY=-55 EndZ=0
    g4: GeomPoint [constr] X=0 Y=0 Z=0
    g5: LineSegment StartX=37.5 StartY=-60.5 StartZ=0 EndX=37.5 EndY=56 EndZ=0
    g6: LineSegment StartX=35.5 StartY=58 StartZ=0 EndX=-35.5 EndY=58 EndZ=0
    g7: LineSegment StartX=-37.5 StartY=56 StartZ=0 EndX=-37.5 EndY=-56 EndZ=0
    g8: GeomPoint [constr] X=0 Y=0 Z=0
    g9: LineSegment StartX=-35.5 StartY=-58 StartZ=0 EndX=8 EndY=-58 EndZ=0
    g10: LineSegment StartX=9.5 StartY=-59.5 StartZ=0 EndX=9.5 EndY=-60.5 EndZ=0
    g11: LineSegment StartX=13.5 StartY=-64.5 StartZ=0 EndX=33.5 EndY=-64.5 EndZ=0
    g12: ArcOfCircle CenterX=8 CenterY=-59.5 CenterZ=0 NormalX=0 NormalY=0 NormalZ=1 AngleXU=0 Radius=1.5 StartAngle=-9e-16 EndAngle=1.5708
    g13: GeomPoint [constr] X=9.5 Y=-58 Z=0
    g14: ArcOfCircle CenterX=13.5 CenterY=-60.5 CenterZ=0 NormalX=0 NormalY=0 NormalZ=1 AngleXU=0 Radius=4 StartAngle=3.14159 EndAngle=4.71239
    g15: GeomPoint [constr] X=9.5 Y=-64.5 Z=0
    g16: ArcOfCircle CenterX=33.5 CenterY=-60.5 CenterZ=0 NormalX=0 NormalY=0 NormalZ=1 AngleXU=0 Radius=4 StartAngle=4.71239 EndAngle=6.28319
    g17: GeomPoint [constr] X=37.5 Y=-64.5 Z=0
    g18: ArcOfCircle CenterX=35.5 CenterY=56 CenterZ=0 NormalX=0 NormalY=0 NormalZ=1 AngleXU=0 Radius=2 StartAngle=1e-15 EndAngle=1.5708
    g19: GeomPoint [constr] X=37.5 Y=58 Z=0
    g20: ArcOfCircle CenterX=-35.5 CenterY=56 CenterZ=0 NormalX=0 NormalY=0 NormalZ=1 AngleXU=0 Radius=2 StartAngle=1.5708 EndAngle=3.14159
    g21: GeomPoint [constr] X=-37.5 Y=58 Z=0
    g22: ArcOfCircle CenterX=-35.5 CenterY=-56 CenterZ=0 NormalX=0 NormalY=0 NormalZ=1 AngleXU=0 Radius=2 StartAngle=3.14159 EndAngle=4.71239
    g23: GeomPoint [constr] X=-37.5 Y=-58 Z=0
  constraints (55):
    c: Coincident(g0,g1)
    c: Coincident(g1,g2)
    c: Coincident(g2,g3)
    c: Coincident(g3,g0)
    c: Horizontal(g0)
    c: Horizontal(g2)
    c: Vertical(g1)
    c: Vertical(g3)
    c: Symmetric(g2,g0,g4)
    c: Coincident(g4,g-1)
    c: DistanceY(g3,g3) = 110
    c: DistanceX(g0,g0) = 69
    c: Horizontal(g6)
    c: Vertical(g5)
    c: Vertical(g7)
    c: Symmetric(g19,g23,g8)
    c: Coincident(g8,g4)
    c: Distance(g2,g6) = 3
    c: DistanceX(g21,g2) = 3
    c: Horizontal(g9)
    c: Vertical(g10)
    c: Horizontal(g11)
    c: PointOnObject(g13,g9)
    c: PointOnObject(g13,g10)
    c: Tangent(g9,g12) = 1.5708
    c: Tangent(g10,g12) = 1.5708
    c: PointOnObject(g15,g10)
    c: PointOnObject(g15,g11)
    c: Tangent(g10,g14) = -1.5708
    c: Tangent(g11,g14) = -1.5708
    c: Distance(g10,g10) = 1
    c: PointOnObject(g17,g11)
    c: PointOnObject(g17,g5)
    c: Tangent(g11,g16) = -1.5708
    c: Tangent(g5,g16) = -1.5708
    c: DistanceX(g11,g11) = 20
    c: PointOnObject(g19,g6)
    c: PointOnObject(g19,g5)
    c: Tangent(g6,g18) = -1.5708
    c: Tangent(g5,g18) = -1.5708
    c: Radius(g18) = 2
    c: PointOnObject(g21,g6)
    c: PointOnObject(g21,g7)
    c: Tangent(g6,g20) = -1.5708
    c: Tangent(g7,g20) = -1.5708
    c: Radius(g20) = 2
    c: PointOnObject(g23,g7)
    c: PointOnObject(g23,g9)
    c: Tangent(g7,g22) = -1.5708
    c: Tangent(g9,g22) = -1.5708
    c: Radius(g22) = 2
    c: DistanceY(g11,g9) = 6.5
    c: Radius(g12) = 1.5
    c: Radius(g14) = 4
    c: Equal(g14,g16)
FEATURE [PartDesign::Pad] Pad004  label="Rough shape"
  Direction = (0,-1,2e-16)
  Length = 18.5
  Length2 = 10
  Placement = pos=(0,0,0) rot=(1,0,0;1.5708rad)
  Profile = -> Sketch004
  ReferenceAxis = -> Sketch004 [N_Axis]
  Refine = true
  SideType = 0
  Suppressed = false
  Type = 0
  Type2 = 0
  expr: Length = Spreadsheet.body_height
FEATURE [PartDesign::Thickness] Thickness
  Base = -> Pad004 [Face14]
  BaseFeature = -> Pad004
  Intersection = false
  Join = 0
  Mode = 0
  Refine = true
  Reversed = true
  SupportTransform = false
  Suppressed = false
  Value = 1.5
  expr: Value = Spreadsheet.Wall
FEATURE [PartDesign::Plane] DatumPlane  label="linking the shape from BASE"
  AttachmentSupport = -> [Thickness]
  Length = 94.1703
  MapMode = 5
  Placement = pos=(0,-18.5,4.1e-15) rot=(1,0,0;1.5708rad)
  ResizeMode = 0
  Width = 141.67
FEATURE [Sketcher::SketchObject] Sketch014
  ArcFitTolerance = 1e-06
  AttachmentSupport = -> [DatumPlane]
  ExternalTypes = [0]
  FullyConstrained = true
  MakeInternals = false
  MapMode = 5
  Placement = pos=(0,-18.5,4.1e-15) rot=(1,0,0;1.5708rad)
  _ExternalGeoVersion = 0
  sketch-geometry (12):
    g0: LineSegment StartX=-35.5 StartY=58 StartZ=0 EndX=35.5 EndY=58 EndZ=0
    g1: LineSegment StartX=37.5 StartY=56 StartZ=0 EndX=37.5 EndY=-60.5 EndZ=0
    g2: LineSegment StartX=-37.5 StartY=56 StartZ=0 EndX=-37.5 EndY=-56 EndZ=0
    g3: LineSegment StartX=13.5 StartY=-64.5 StartZ=0 EndX=33.5 EndY=-64.5 EndZ=0
    g4: LineSegment StartX=9.5 StartY=-60.5 StartZ=0 EndX=9.5 EndY=-59.5 EndZ=0
    g5: LineSegment StartX=8 StartY=-58 StartZ=0 EndX=-35.5 EndY=-58 EndZ=0
    g6: ArcOfCircle CenterX=-35.5 CenterY=-56 CenterZ=0 NormalX=0 NormalY=0 NormalZ=1 AngleXU=0 Radius=2 StartAngle=3.14159 EndAngle=4.71239
    g7: ArcOfCircle CenterX=8 CenterY=-59.5 CenterZ=0 NormalX=0 NormalY=0 NormalZ=1 AngleXU=0 Radius=1.5 StartAngle=-9e-16 EndAngle=1.5708
    g8: ArcOfCircle CenterX=13.5 CenterY=-60.5 CenterZ=0 NormalX=0 NormalY=0 NormalZ=1 AngleXU=0 Radius=4 StartAngle=3.14159 EndAngle=4.71239
    g9: ArcOfCircle CenterX=33.5 CenterY=-60.5 CenterZ=0 NormalX=0 NormalY=0 NormalZ=1 AngleXU=0 Radius=4 StartAngle=4.71239 EndAngle=6.28319
    g10: ArcOfCircle CenterX=35.5 CenterY=56 CenterZ=0 NormalX=0 NormalY=0 NormalZ=1 AngleXU=0 Radius=2 StartAngle=5.933e-13 EndAngle=1.5708
    g11: ArcOfCircle CenterX=-35.5 CenterY=56 CenterZ=0 NormalX=0 NormalY=0 NormalZ=1 AngleXU=0 Radius=2 StartAngle=1.5708 EndAngle=3.14159
  constraints (30):
    c: Coincident(g-15,g0)
    c: Coincident(g-14,g0)
    c: Coincident(g-14,g1)
    c: Coincident(g1,g-12)
    c: Coincident(g-4,g2)
    c: Coincident(g2,g-15)
    c: Coincident(g3,g-10)
    c: Coincident(g3,g-11)
    c: Coincident(g4,g-9)
    c: Coincident(g4,g-8)
    c: Coincident(g-5,g5)
    c: Coincident(g-6,g5)
    c: Coincident(g6,g2)
    c: Coincident(g6,g5)
    c: Equal(g-4,g6)
    c: Coincident(g7,g5)
    c: Coincident(g7,g4)
    c: Coincident(g8,g4)
    c: Coincident(g8,g3)
    c: Coincident(g9,g1)
    c: Coincident(g9,g3)
    c: Equal(g-11,g9)
    c: Equal(g-9,g8)
    c: Equal(g-6,g7)
    c: Coincident(g10,g0)
    c: Coincident(g10,g1)
    c: Coincident(g11,g2)
    c: Coincident(g11,g0)
    c: Equal(g-15,g11)
    c: Equal(g10,g-14)
FEATURE [PartDesign::Pad] Pad011  label="Rough shape001"
  Direction = (0,-1,2e-16)
  Length = 1.5
  Length2 = 10
  Placement = pos=(0,-18.5,4.1e-15) rot=(1,0,0;1.5708rad)
  Profile = -> Sketch014
  ReferenceAxis = -> Sketch014 [N_Axis]
  Refine = true
  SideType = 0
  Suppressed = false
  Type = 0
  Type2 = 0
  expr: Length = Spreadsheet.Wall
FEATURE [Sketcher::SketchObject] Sketch015
  ArcFitTolerance = 1e-06
  AttachmentSupport = -> [Pad011]
  ExternalGeometry = -> [Pad011]
  ExternalTypes = [0]
  FullyConstrained = true
  MakeInternals = false
  MapMode = 5
  Placement = pos=(0,-18.5,4.1e-15) rot=(-1,0,0;1.5708rad)
  _ExternalGeoVersion = 0
  expr: Constraints[11] = Spreadsheet.KPD_x_ofset
  expr: Constraints[12] = Spreadsheet.KPD_y_ofset
  expr: Constraints[2] = Spreadsheet.Wall
  expr: Constraints[31] = Spreadsheet.KPD_tab_margin_bottom
  expr: Constraints[32] = Spreadsheet.KPD_tab_margin_sides
  expr: Constraints[36] = Spreadsheet.KPD_y_grid
  expr: Constraints[39] = Spreadsheet.KPD_tab_length
  expr: Constraints[63] = Spreadsheet.KPD_x_grid
  expr: Constraints[87] = Spreadsheet.KPD_x_grid
  sketch-geometry (30):
    g0: LineSegment [constr] StartX=-36 StartY=-56 StartZ=0 EndX=-36 EndY=56 EndZ=0
    g1: LineSegment [constr] StartX=-35.5 StartY=-56.5 StartZ=0 EndX=35.5 EndY=-56.5 EndZ=0
    g2: LineSegment [constr] StartX=-31.5 StartY=-48 StartZ=0 EndX=35.5 EndY=-48 EndZ=0
    g3: LineSegment [constr] StartX=-31.5 StartY=56 StartZ=0 EndX=-31.5 EndY=-48 EndZ=0
    g4: LineSegment StartX=-31.5 StartY=-48 StartZ=0 EndX=-20 EndY=-48 EndZ=0
    g5: LineSegment StartX=-31.5 StartY=-48 StartZ=0 EndX=-31.5 EndY=-34 EndZ=0
    g6: LineSegment StartX=-31.5 StartY=-34 StartZ=0 EndX=-20 EndY=-34 EndZ=0
    g7: LineSegment StartX=-20 StartY=-34 StartZ=0 EndX=-20 EndY=-33 EndZ=0
    g8: LineSegment StartX=-20 StartY=-33 StartZ=0 EndX=-33 EndY=-33 EndZ=0
    g9: LineSegment StartX=-33 StartY=-33 StartZ=0 EndX=-33 EndY=-49 EndZ=0
    g10: LineSegment StartX=-33 StartY=-49 StartZ=0 EndX=-20 EndY=-49 EndZ=0
    g11: LineSegment StartX=-20 StartY=-48 StartZ=0 EndX=-20 EndY=-49 EndZ=0
    g12: GeomPoint X=-20 Y=-48.5 Z=0
    g13: GeomPoint X=-20 Y=-33.5 Z=0
    g14: LineSegment StartX=1.8e-15 StartY=-33 StartZ=0 EndX=-13 EndY=-33 EndZ=0
    g15: LineSegment StartX=-13 StartY=-33 StartZ=0 EndX=-13 EndY=-49 EndZ=0
    g16: LineSegment StartX=-13 StartY=-49 StartZ=0 EndX=1.8e-15 EndY=-49 EndZ=0
    g17: LineSegment StartX=1.8e-15 StartY=-49 StartZ=0 EndX=1.8e-15 EndY=-48 EndZ=0
    g18: LineSegment StartX=1.8e-15 StartY=-48 StartZ=0 EndX=-11.5 EndY=-48 EndZ=0
    g19: LineSegment StartX=-11.5 StartY=-48 StartZ=0 EndX=-11.5 EndY=-34 EndZ=0
    g20: LineSegment StartX=-11.5 StartY=-34 StartZ=0 EndX=1.8e-15 EndY=-34 EndZ=0
    g21: LineSegment StartX=1.8e-15 StartY=-34 StartZ=0 EndX=1.8e-15 EndY=-33 EndZ=0
    g22: LineSegment StartX=8.5 StartY=-48 StartZ=0 EndX=20 EndY=-48 EndZ=0
    g23: LineSegment StartX=20 StartY=-48 StartZ=0 EndX=20 EndY=-49 EndZ=0
    g24: LineSegment StartX=20 StartY=-49 StartZ=0 EndX=7 EndY=-49 EndZ=0
    g25: LineSegment StartX=7 StartY=-49 StartZ=0 EndX=7 EndY=-33 EndZ=0
    g26: LineSegment StartX=7 StartY=-33 StartZ=0 EndX=20 EndY=-33 EndZ=0
    g27: LineSegment StartX=20 StartY=-33 StartZ=0 EndX=20 EndY=-34 EndZ=0
    g28: LineSegment StartX=20 StartY=-34 StartZ=0 EndX=8.5 EndY=-34 EndZ=0
    g29: LineSegment StartX=8.5 StartY=-34 StartZ=0 EndX=8.5 EndY=-48 EndZ=0
  constraints (88):
    c: Vertical(g0)
    c: Horizontal(g-3,g0)
    c: DistanceX(g-3,g0) = 1.5
    c: Horizontal(g-3,g0)
    c: Horizontal(g1)
    c: DistanceY(g-4,g1) = 1.5
    c: Vertical(g-4,g1)
    c: Vertical(g-4,g1)
    c: Coincident(g3,g2)
    c: Horizontal(g2)
    c: Vertical(g3)
    c: DistanceX(g-3,g2) = 6
    c: Distance(g2,g-4) = 10
    c: Coincident(g2,g4)
    c: PointOnObject(g4,g2)
    c: Coincident(g2,g5)
    c: PointOnObject(g5,g3)
    c: Coincident(g5,g6)
    c: Horizontal(g6)
    c: Vertical(g6,g4)
    c: Coincident(g6,g7)
    c: Vertical(g7)
    c: Coincident(g7,g8)
    c: Horizontal(g8)
    c: Coincident(g9,g8)
    c: Vertical(g9)
    c: Coincident(g10,g9)
    c: Horizontal(g10)
    c: Coincident(g11,g4)
    c: Coincident(g11,g10)
    c: Vertical(g11)
    c: DistanceX(g8,g5) = 1.5
    c: DistanceY(g11,g11) = 1
    c: Equal(g7,g11)
    c: Symmetric(g11,g11,g12)
    c: Symmetric(g7,g7,g13)
    c: DistanceY(g12,g13) = 15
    c: Horizontal(g0,g3)
    c: Vertical(g2,g1)
    c: DistanceX(g8,g7) = 13
    c: Horizontal(g14)
    c: Coincident(g14,g15)
    c: Vertical(g15)
    c: Coincident(g15,g16)
    c: Horizontal(g16)
    c: Coincident(g16,g17)
    c: PointOnObject(g17,g2)
    c: Coincident(g17,g18)
    c: Horizontal(g18)
    c: Coincident(g18,g19)
    c: Vertical(g19)
    c: Coincident(g19,g20)
    c: Horizontal(g20)
    c: Coincident(g20,g21)
    c: Coincident(g21,g14)
    c: Vertical(g21)
    c: Vertical(g17)
    c: Equal(g9,g15)
    c: Equal(g8,g14)
    c: Equal(g20,g6)
    c: Equal(g17,g11)
    c: Equal(g21,g17)
    c: Vertical(g17,g20)
    c: DistanceX(g8,g14) = 20
    c: PointOnObject(g22,g2)
    c: Horizontal(g22)
    c: Coincident(g22,g23)
    c: Vertical(g23)
    c: Coincident(g23,g24)
    c: Horizontal(g24)
    c: Coincident(g24,g25)
    c: Vertical(g25)
    c: Coincident(g25,g26)
    c: Horizontal(g26)
    c: Coincident(g26,g27)
    c: Vertical(g27)
    c: Coincident(g27,g28)
    c: Horizontal(g28)
    c: Coincident(g28,g29)
    c: Coincident(g29,g22)
    c: Vertical(g29)
    c: Equal(g25,g15)
    c: Equal(g19,g29)
    c: Equal(g23,g17)
    c: Equal(g26,g14)
    c: Equal(g28,g20)
    c: Equal(g26,g24)
    c: DistanceX(g14,g25) = 20
FEATURE [PartDesign::Pocket] Pocket003  label="Compliant buttons"
  BaseFeature = -> Pad011
  Direction = (0,-1,-2e-16)
  Length = 5
  Length2 = 5
  Placement = pos=(0,-18.5,4.1e-15) rot=(1,0,0;1.5708rad)
  Profile = -> Sketch015
  ReferenceAxis = -> Sketch015 [N_Axis]
  Refine = true
  SideType = 0
  Suppressed = false
  Type = 2
  Type2 = 0
FEATURE [PartDesign::LinearPattern] LinearPattern  label="LinearPattern of Compliant buttons"
  BaseFeature = -> Pocket003
  Direction = -> Sketch015 [V_Axis]
  Length = 45
  Length2 = 100
  Mode = 1
  Mode2 = 0
  Occurrences = 4
  Occurrences2 = 1
  Offset = 15
  Offset2 = 10
  Originals = -> [Pocket003]
  Placement = pos=(0,-18.5,4.1e-15) rot=(1,0,0;1.5708rad)
  Refine = true
  Reversed2 = false
  SpacingPattern = [0]
  SpacingPattern2 = [0]
  Spacings = [-1,-1,-1]
  Suppressed = false
  TransformMode = 0
FEATURE [Sketcher::SketchObject] Sketch016
  ArcFitTolerance = 1e-06
  AttachmentSupport = -> [LinearPattern]
  ExternalTypes = [0]
  FullyConstrained = true
  MakeInternals = false
  MapMode = 5
  Placement = pos=(0,-18.5,4.1e-15) rot=(-1,0,0;1.5708rad)
  _ExternalGeoVersion = 0
  expr: Constraints[17] = Spreadsheet.KPD_x_grid
  expr: Constraints[2] = Spreadsheet.twoM_holes_thread
  sketch-geometry (9):
    g0: Circle CenterX=-16.5 CenterY=-33.5 CenterZ=0 NormalX=0 NormalY=0 NormalZ=1 AngleXU=0 Radius=0.85
    g1: Circle CenterX=-16.5 CenterY=-33.5 CenterZ=0 NormalX=0 NormalY=0 NormalZ=1 AngleXU=0 Radius=2
    g2: GeomPoint X=-20 Y=-33.5 Z=0
    g3: LineSegment [constr] StartX=-20 StartY=-33.5 StartZ=0 EndX=-13 EndY=-33.5 EndZ=0
    g4: GeomPoint [constr] X=-16.5 Y=-33.5 Z=0
    g5: Circle CenterX=3.5 CenterY=-33.5 CenterZ=0 NormalX=0 NormalY=0 NormalZ=1 AngleXU=0 Radius=0.85
    g6: Circle CenterX=3.5 CenterY=-33.5 CenterZ=0 NormalX=0 NormalY=0 NormalZ=1 AngleXU=0 Radius=2
    g7: Circle CenterX=23.5 CenterY=-33.5 CenterZ=0 NormalX=0 NormalY=0 NormalZ=1 AngleXU=0 Radius=2
    g8: Circle CenterX=23.5 CenterY=-33.5 CenterZ=0 NormalX=0 NormalY=0 NormalZ=1 AngleXU=0 Radius=0.85
  constraints (19):
    c: Coincident(g1,g0)
    c: Diameter(g1) = 4
    c: Diameter(g0) = 1.7
    c: Symmetric(g-3,g-3,g2)
    c: Horizontal(g2,g0)
    c: Coincident(g3,g2)
    c: PointOnObject(g3,g-4)
    c: Symmetric(g3,g3,g4)
    c: Coincident(g4,g0)
    c: Coincident(g6,g5)
    c: Coincident(g8,g7)
    c: Horizontal(g5,g7)
    c: Horizontal(g5,g0)
    c: Equal(g0,g5)
    c: Equal(g6,g1)
    c: Equal(g8,g5)
    c: Equal(g7,g6)
    c: DistanceX(g0,g5) = 20
    c: DistanceX(g5,g7) = 20
FEATURE [Sketcher::SketchObject] Sketch017
  ArcFitTolerance = 1e-06
  AttachmentSupport = -> [LinearPattern]
  ExternalGeometry = -> [Sketch016]
  ExternalTypes = [0]
  FullyConstrained = true
  MakeInternals = false
  MapMode = 5
  Placement = pos=(0,-18.5,4.1e-15) rot=(-1,0,0;1.5708rad)
  _ExternalGeoVersion = 0
  expr: Constraints[13] = Spreadsheet.KPD_x_grid / 2
  expr: Constraints[40] = Spreadsheet.KPD_x_grid
  sketch-geometry (16):
    g0: LineSegment [constr] StartX=-31.5 StartY=-41 StartZ=0 EndX=-16.5 EndY=-41 EndZ=0
    g1: LineSegment StartX=-28 StartY=-42.25 StartZ=0 EndX=-25 EndY=-42.25 EndZ=0
    g2: LineSegment StartX=-25 StartY=-42.25 StartZ=0 EndX=-25 EndY=-39.75 EndZ=0
    g3: LineSegment StartX=-25 StartY=-39.75 StartZ=0 EndX=-28 EndY=-39.75 EndZ=0
    g4: LineSegment StartX=-28 StartY=-39.75 StartZ=0 EndX=-28 EndY=-42.25 EndZ=0
    g5: GeomPoint [constr] X=-26.5 Y=-41 Z=0
    g6: LineSegment StartX=-8 StartY=-42.25 StartZ=0 EndX=-5 EndY=-42.25 EndZ=0
    g7: LineSegment StartX=-5 StartY=-42.25 StartZ=0 EndX=-5 EndY=-39.75 EndZ=0
    g8: LineSegment StartX=-5 StartY=-39.75 StartZ=0 EndX=-8 EndY=-39.75 EndZ=0
    g9: LineSegment StartX=-8 StartY=-39.75 StartZ=0 EndX=-8 EndY=-42.25 EndZ=0
    g10: GeomPoint [constr] X=-6.5 Y=-41 Z=0
    g11: LineSegment StartX=12 StartY=-42.25 StartZ=0 EndX=15 EndY=-42.25 EndZ=0
    g12: LineSegment StartX=15 StartY=-42.25 StartZ=0 EndX=15 EndY=-39.75 EndZ=0
    g13: LineSegment StartX=15 StartY=-39.75 StartZ=0 EndX=12 EndY=-39.75 EndZ=0
    g14: LineSegment StartX=12 StartY=-39.75 StartZ=0 EndX=12 EndY=-42.25 EndZ=0
    g15: GeomPoint [constr] X=13.5 Y=-41 Z=0
  constraints (42):
    c: Symmetric(g-3,g-3,g0)
    c: Horizontal(g0)
    c: Vertical(g-4,g0)
    c: Coincident(g1,g2)
    c: Coincident(g2,g3)
    c: Coincident(g3,g4)
    c: Coincident(g4,g1)
    c: Horizontal(g1)
    c: Horizontal(g3)
    c: Vertical(g2)
    c: Vertical(g4)
    c: Symmetric(g3,g1,g5)
    c: PointOnObject(g5,g0)
    c: DistanceX(g5,g-4) = 10
    c: DistanceY(g2,g2) = 2.5
    c: DistanceX(g3,g3) = 3
    c: Coincident(g6,g7)
    c: Coincident(g7,g8)
    c: Coincident(g8,g9)
    c: Coincident(g9,g6)
    c: Horizontal(g6)
    c: Horizontal(g8)
    c: Vertical(g7)
    c: Vertical(g9)
    c: Symmetric(g8,g6,g10)
    c: Coincident(g11,g12)
    c: Coincident(g12,g13)
    c: Coincident(g13,g14)
    c: Coincident(g14,g11)
    c: Horizontal(g11)
    c: Horizontal(g13)
    c: Vertical(g12)
    c: Vertical(g14)
    c: Symmetric(g13,g11,g15)
    c: Horizontal(g10,g0)
    c: Horizontal(g10,g15)
    c: Equal(g3,g8)
    c: Equal(g8,g13)
    c: Equal(g14,g9)
    c: Equal(g9,g4)
    c: DistanceX(g5,g10) = 20
    c: DistanceX(g10,g15) = 20
FEATURE [PartDesign::Pad] Pad012  label="KPD Holes"
  BaseFeature = -> LinearPattern
  Direction = (0,1,2e-16)
  Length = 3.5
  Length2 = 10
  Placement = pos=(0,-18.5,4.1e-15) rot=(1,0,0;1.5708rad)
  Profile = -> Sketch016
  ReferenceAxis = -> Sketch016 [N_Axis]
  Refine = true
  SideType = 0
  Suppressed = false
  Type = 0
  Type2 = 0
FEATURE [PartDesign::Chamfer] Chamfer002
  Angle = 45
  Base = -> Pad012 [Edge228,Edge227,Edge226]
  BaseFeature = -> Pad012
  ChamferType = 0
  FlipDirection = false
  Placement = pos=(0,-18.5,4.1e-15) rot=(1,0,0;1.5708rad)
  Refine = true
  Size = 0.5
  Size2 = 1
  SupportTransform = false
  Suppressed = false
  UseAllEdges = false
FEATURE [PartDesign::LinearPattern] LinearPattern001  label="LinearPattern of KPD Holes"
  BaseFeature = -> Chamfer002
  Direction = -> Sketch016 [V_Axis]
  Length = 30
  Length2 = 100
  Mode = 1
  Mode2 = 0
  Occurrences = 3
  Occurrences2 = 1
  Offset = 15
  Offset2 = 10
  Originals = -> [Pad012,Chamfer002]
  Placement = pos=(0,-18.5,4.1e-15) rot=(1,0,0;1.5708rad)
  Refine = true
  Reversed2 = false
  SpacingPattern = [0]
  SpacingPattern2 = [0]
  Spacings = [-1,-1]
  Suppressed = false
  TransformMode = 0
  expr: Offset = Spreadsheet.KPD_y_grid
FEATURE [PartDesign::Pad] Pad013  label="KPD Button pressy"
  BaseFeature = -> LinearPattern001
  Direction = (0,1,2e-16)
  Length = 2
  Length2 = 10
  Placement = pos=(0,-18.5,4.1e-15) rot=(1,0,0;1.5708rad)
  Profile = -> Sketch017
  ReferenceAxis = -> Sketch017 [N_Axis]
  Refine = true
  SideType = 0
  Suppressed = false
  Type = 0
  Type2 = 0
FEATURE [PartDesign::Fillet] Fillet  label="Filleton KPD Button pressy"
  Base = -> Pad013 [Edge173,Edge176,Edge224,Edge221,Edge284,Edge281]
  BaseFeature = -> Pad013
  Placement = pos=(0,-18.5,4.1e-15) rot=(1,0,0;1.5708rad)
  Radius = 1.3
  Refine = true
  SupportTransform = false
  Suppressed = false
  UseAllEdges = false
FEATURE [PartDesign::Fillet] Fillet001  label="Fillet001 on KPD Button pressy"
  Base = -> Fillet [Edge70,Edge69,Edge46,Edge3,Edge99,Edge100,Edge102,Edge101,Edge71,Edge72,Edge47,Edge9]
  BaseFeature = -> Fillet
  Placement = pos=(0,-18.5,4.1e-15) rot=(1,0,0;1.5708rad)
  Radius = 0.6
  Refine = true
  SupportTransform = false
  Suppressed = false
  UseAllEdges = false
FEATURE [PartDesign::LinearPattern] LinearPattern003  label="LinearPattern of KPD Button pressy"
  BaseFeature = -> Fillet001
  Direction = -> Sketch017 [V_Axis]
  Length = 45
  Length2 = 100
  Mode = 1
  Mode2 = 0
  Occurrences = 4
  Occurrences2 = 1
  Offset = 15
  Offset2 = 10
  Originals = -> [Pad013,Fillet,Fillet001]
  Placement = pos=(0,-18.5,4.1e-15) rot=(1,0,0;1.5708rad)
  Refine = true
  Reversed2 = false
  SpacingPattern = [0]
  SpacingPattern2 = [0]
  Spacings = [-1,-1,-1]
  Suppressed = false
  TransformMode = 0
  expr: Length = Spreadsheet.KPD_y_grid
FEATURE [Sketcher::SketchObject] Sketch020
  ArcFitTolerance = 1e-06
  AttachmentSupport = -> [LinearPattern003]
  ExternalTypes = [0]
  FullyConstrained = true
  MakeInternals = false
  MapMode = 5
  Placement = pos=(0,-20,4.5e-15) rot=(1,0,0;1.5708rad)
  _ExternalGeoVersion = 0
  sketch-geometry (5):
    g0: LineSegment StartX=-26.05 StartY=-53.15 StartZ=0 EndX=26.05 EndY=-53.15 EndZ=0
    g1: LineSegment StartX=26.05 StartY=-53.15 StartZ=0 EndX=26.05 EndY=-26.55 EndZ=0
    g2: LineSegment StartX=26.05 StartY=-26.55 StartZ=0 EndX=-26.05 EndY=-26.55 EndZ=0
    g3: LineSegment StartX=-26.05 StartY=-26.55 StartZ=0 EndX=-26.05 EndY=-53.15 EndZ=0
    g4: GeomPoint [constr] X=0 Y=-39.85 Z=0
  constraints (13):
    c: Coincident(g0,g1)
    c: Coincident(g1,g2)
    c: Coincident(g2,g3)
    c: Coincident(g3,g0)
    c: Horizontal(g0)
    c: Horizontal(g2)
    c: Vertical(g1)
    c: Vertical(g3)
    c: Symmetric(g2,g0,g4)
    c: Distance(g1,g3) = 52.1
    c: Distance(g0,g2) = 26.6
    c: PointOnObject(g4,g-2)
    c: Distance(g0,g-3) = 4.85
FEATURE [PartDesign::Pocket] Pocket005  label="Eink hole"
  BaseFeature = -> LinearPattern003
  Direction = (0,1,-2e-16)
  Length = 5
  Length2 = 5
  Placement = pos=(0,-18.5,4.1e-15) rot=(1,0,0;1.5708rad)
  Profile = -> Sketch020
  ReferenceAxis = -> Sketch020 [N_Axis]
  Refine = true
  SideType = 0
  Suppressed = false
  Type = 2
  Type2 = 0
FEATURE [Sketcher::SketchObject] Sketch021
  ArcFitTolerance = 1e-06
  AttachmentSupport = -> [Pocket005]
  ExternalTypes = [0]
  FullyConstrained = true
  MakeInternals = false
  MapMode = 5
  Placement = pos=(0,-18.5,4.1e-15) rot=(-1,0,0;1.5708rad)
  _ExternalGeoVersion = 0
  expr: Constraints[32] = Spreadsheet.Wall
  expr: Constraints[35] = Spreadsheet.Wall
  sketch-geometry (13):
    g0: LineSegment StartX=27.8 StartY=24.71 StartZ=0 EndX=27.8 EndY=55.08 EndZ=0
    g1: LineSegment StartX=27.8 StartY=55.08 StartZ=0 EndX=-32.67 EndY=55.08 EndZ=0
    g2: LineSegment StartX=-32.67 StartY=24.71 StartZ=0 EndX=27.8 EndY=24.71 EndZ=0
    g3: GeomPoint X=-2.435 Y=39.895 Z=0
    g4: LineSegment StartX=-32.67 StartY=55.08 StartZ=0 EndX=-32.67 EndY=47.78 EndZ=0
    g5: LineSegment StartX=-32.67 StartY=47.78 StartZ=0 EndX=-34.17 EndY=47.78 EndZ=0
    g6: LineSegment StartX=-34.17 StartY=47.78 StartZ=0 EndX=-34.17 EndY=56.58 EndZ=0
    g7: LineSegment StartX=-34.17 StartY=56.58 StartZ=0 EndX=29.3 EndY=56.58 EndZ=0
    g8: LineSegment StartX=29.3 StartY=56.58 StartZ=0 EndX=29.3 EndY=23.21 EndZ=0
    g9: LineSegment StartX=29.3 StartY=23.21 StartZ=0 EndX=-34.17 EndY=23.21 EndZ=0
    g10: LineSegment StartX=-34.17 StartY=23.21 StartZ=0 EndX=-34.17 EndY=30.01 EndZ=0
    g11: LineSegment StartX=-34.17 StartY=30.01 StartZ=0 EndX=-32.67 EndY=30.01 EndZ=0
    g12: LineSegment StartX=-32.67 StartY=30.01 StartZ=0 EndX=-32.67 EndY=24.71 EndZ=0
  constraints (36):
    c: Coincident(g0,g1)
    c: Coincident(g2,g0)
    c: Vertical(g0)
    c: Horizontal(g1)
    c: Horizontal(g2)
    c: DistanceY(g-4,g1) = 1.93
    c: DistanceX(g1,g-4) = 6.62
    c: DistanceY(g2,g-6) = 1.84
    c: DistanceX(g-5,g0) = 1.75
    c: Symmetric(g2,g0,g3)
    c: Vertical(g1,g2)
    c: Coincident(g1,g4)
    c: Vertical(g4)
    c: Coincident(g4,g5)
    c: Horizontal(g5)
    c: Coincident(g5,g6)
    c: Vertical(g6)
    c: Coincident(g6,g7)
    c: Horizontal(g7)
    c: Coincident(g7,g8)
    c: Vertical(g8)
    c: Coincident(g8,g9)
    c: Horizontal(g9)
    c: Coincident(g9,g10)
    c: Vertical(g10)
    c: Coincident(g10,g11)
    c: Horizontal(g11)
    c: Coincident(g11,g12)
    c: Coincident(g12,g2)
    c: Vertical(g12)
    c: DistanceY(g4,g4) = 7.3
    c: DistanceY(g12,g12) = 5.3
    c: DistanceY(g9,g2) = 1.5
    c: Symmetric(g9,g7,g3)
    c: Vertical(g5,g10)
    c: DistanceX(g9,g2) = 1.5
FEATURE [PartDesign::Pad] Pad015  label="Eink frame"
  BaseFeature = -> Pocket005
  Direction = (0,1,2e-16)
  Length = 1.3
  Length2 = 10
  Placement = pos=(0,-18.5,4.1e-15) rot=(1,0,0;1.5708rad)
  Profile = -> Sketch021
  ReferenceAxis = -> Sketch021 [N_Axis]
  Refine = true
  SideType = 0
  Suppressed = false
  Type = 0
  Type2 = 0
FEATURE [PartDesign::Pocket] Pocket013
  BaseFeature = -> Pad015
  Direction = (0,1,-2e-16)
  Length = 0.2
  Length2 = 5
  Placement = pos=(0,-18.5,4.1e-15) rot=(1,0,0;1.5708rad)
  Profile = -> Sketch039
  ReferenceAxis = -> Sketch039 [N_Axis]
  Refine = true
  SideType = 0
  Suppressed = false
  Type = 0
  Type2 = 0
FEATURE [PartDesign::Pocket] Pocket006  label="menu BTNs"
  BaseFeature = -> Pocket013
  Direction = (0,1,-2e-16)
  Length = 5
  Length2 = 5
  Placement = pos=(0,-18.5,4.1e-15) rot=(1,0,0;1.5708rad)
  Profile = -> Sketch023
  ReferenceAxis = -> Sketch023 [N_Axis]
  Refine = true
  SideType = 0
  Suppressed = false
  Type = 0
  Type2 = 0
FEATURE [PartDesign::Plane] DatumPlane001
  AttachmentOffset = pos=(0,0,1.5) rot=(0,0,1;0rad)
  AttachmentSupport = -> [Pocket006]
  Length = 60
  MapMode = 5
  Placement = pos=(0,-21.5,4.8e-15) rot=(1,0,0;1.5708rad)
  ResizeMode = 0
  Width = 60
FEATURE [Sketcher::SketchObject] Sketch024
  ArcFitTolerance = 1e-06
  AttachmentSupport = -> [DatumPlane001]
  ExternalTypes = [0]
  FullyConstrained = true
  MakeInternals = false
  MapMode = 5
  Placement = pos=(0,-21.5,4.8e-15) rot=(1,0,0;1.5708rad)
  _ExternalGeoVersion = 0
  expr: Constraints[1] = Spreadsheet.Tolerance
  sketch-geometry (1):
    g0: Circle CenterX=4.05 CenterY=-19.15 CenterZ=0 NormalX=0 NormalY=0 NormalZ=1 AngleXU=0 Radius=3.3
  constraints (3):
    c: Coincident(g0,g-3)
    c: Distance(g-3,g0) = 0.2
    c: Diameter(g0) = 6.6
FEATURE [PartDesign::Pad] Pad017
  Direction = (0,-1,0)
  Length = 2.5
  Length2 = 10
  Placement = pos=(0,-21.5,4.8e-15) rot=(1,0,0;1.5708rad)
  Profile = -> Sketch024
  ReferenceAxis = -> Sketch024 [N_Axis]
  Refine = true
  SideType = 0
  Suppressed = false
  Type = 0
  Type2 = 0
FEATURE [Sketcher::SketchObject] Sketch025
  ArcFitTolerance = 1e-06
  AttachmentSupport = -> [Pad017]
  ExternalTypes = [0]
  FullyConstrained = true
  MakeInternals = false
  MapMode = 5
  Placement = pos=(0,-21.5,4.8e-15) rot=(-1,0,0;1.5708rad)
  _ExternalGeoVersion = 0
  sketch-geometry (1):
    g0: Circle CenterX=4.05 CenterY=19.15 CenterZ=0 NormalX=0 NormalY=0 NormalZ=1 AngleXU=0 Radius=3.9
  constraints (2):
    c: Coincident(g0,g-3)
    c: Distance(g-3,g0) = 0.6
FEATURE [PartDesign::Pad] Pad018
  BaseFeature = -> Pad017
  Direction = (0,1,0)
  Length = 7
  Length2 = 10
  Placement = pos=(0,-21.5,4.8e-15) rot=(1,0,0;1.5708rad)
  Profile = -> Sketch025
  ReferenceAxis = -> Sketch025 [N_Axis]
  Refine = true
  SideType = 0
  Suppressed = false
  Type = 0
  Type2 = 0
FEATURE [PartDesign::Body] Body008  label="Menu BTN"
  AllowCompound = false
  Group = -> [DatumPlane001,Binder002,Sketch024,Pad017,Sketch025,Pad018]
  Origin = -> Origin080
  Placement = pos=(0,3.2,0) rot=(0,0,1;0rad)
  Tip = -> Pad018
FEATURE [PartDesign::Plane] DatumPlane002
  AttachmentOffset = pos=(0,0,0) rot=(1,0,0;1.5708rad)
  AttachmentSupport = -> [Pocket006]
  Length = 60
  MapMode = 7
  Placement = pos=(-3.3,-20,-19.15) rot=(1,0,0;3.14159rad)
  ResizeMode = 0
  Width = 60
FEATURE [Sketcher::SketchObject] Sketch026
  ArcFitTolerance = 1e-06
  AttachmentSupport = -> [DatumPlane002]
  ExternalTypes = [0]
  FullyConstrained = true
  MakeInternals = false
  MapMode = 5
  Placement = pos=(-3.3,-20,-19.15) rot=(1,0,0;3.14159rad)
  _ExternalGeoVersion = 0
  expr: Constraints[13] = 10 / 2
  expr: Constraints[25] = 6 / 2
  expr: Constraints[31] = Spreadsheet.Wall + 1
  sketch-geometry (11):
    g0: LineSegment StartX=-3.75 StartY=-9.5 StartZ=0 EndX=-6.75 EndY=-9.5 EndZ=0
    g1: LineSegment StartX=-6.75 StartY=-9.5 StartZ=0 EndX=-6.75 EndY=-4.5 EndZ=0
    g2: LineSegment StartX=-6 StartY=-2.5 StartZ=0 EndX=-6 EndY=0.5 EndZ=0
    g3: LineSegment StartX=-6 StartY=0.5 StartZ=0 EndX=-8.75 EndY=2.42557 EndZ=0
    g4: LineSegment StartX=-8.75 StartY=2.42557 StartZ=0 EndX=-8.75 EndY=2.72557 EndZ=0
    g5: LineSegment StartX=-3.75 StartY=3.36065 StartZ=0 EndX=-3.75 EndY=-9.5 EndZ=0
    g6: GeomPoint X=-3.75 Y=0 Z=0
    g7: LineSegment [constr] StartX=-6 StartY=0.5 StartZ=0 EndX=-8.75 EndY=0.5 EndZ=0
    g8: ArcOfCircle CenterX=-3.75 CenterY=-16.6393 CenterZ=0 NormalX=0 NormalY=0 NormalZ=1 AngleXU=0 Radius=20 StartAngle=1.5708 EndAngle=1.82348
    g9: LineSegment [constr] StartX=-3.75 StartY=3.36065 StartZ=0 EndX=1.25 EndY=3.36065 EndZ=0
    g10: LineSegment StartX=-6 StartY=-2.5 StartZ=0 EndX=-6.75 EndY=-4.5 EndZ=0
  constraints (35):
    c: Horizontal(g0)
    c: Coincident(g0,g1)
    c: Vertical(g1)
    c: Vertical(g2)
    c: Coincident(g2,g3)
    c: Coincident(g3,g4)
    c: Vertical(g4)
    c: Vertical(g5)
    c: Coincident(g0,g5)
    c: DistanceY(g0,g-4) = 9.5
    c: PointOnObject(g6,g5)
    c: Symmetric(g-4,g-1,g6)
    c: DistanceX(g-4,g2) = 1.5
    c: DistanceX(g4,g5) = 5
    c: Coincident(g7,g2)
    c: Horizontal(g7)
    c: Vertical(g3,g7)
    c: Angle(g3,g7) = 0.610865
    c: DistanceY(g4,g4) = 0.3
    c: Coincident(g8,g5)
    c: Coincident(g8,g4)
    c: Coincident(g9,g5)
    c: Horizontal(g9)
    c: Tangent(g9,g8)
    c: DistanceX(g9,g9) = 5
    c: DistanceX(g0,g0) = 3
    c: DistanceY(g1,g1) = 5
    c: Radius(g8) = 20
    c: Distance(g5,g-4) = 3.36065
    c: Distance(g2,g-4) = 0.5
    c: DistanceX(g2,g6) = 2.25
    c: DistanceY(g2,g-4) = 2.5
    c: Coincident(g10,g2)
    c: Coincident(g10,g1)
    c: DistanceY(g1,g2) = 2
FEATURE [PartDesign::Revolution] Revolution
  Angle = 360
  Angle2 = 60
  Axis = (0,1,0)
  Base = (-7.05,-23.3607,-19.15)
  FuseOrder = 1
  Placement = pos=(-3.3,-20,-19.15) rot=(1,0,0;3.14159rad)
  Profile = -> Sketch026
  ReferenceAxis = -> Sketch026 [Edge1]
  Refine = true
  Suppressed = false
  Type = 0
FEATURE [Sketcher::SketchObject] Sketch040
  ArcFitTolerance = 1e-06
  AttachmentSupport = -> [Pocket006]
  ExternalGeometry = -> [Binder005]
  ExternalTypes = [0,0]
  FullyConstrained = true
  MakeInternals = false
  MapMode = 5
  Placement = pos=(0,-20,4.5e-15) rot=(1,0,0;1.5708rad)
  _ExternalGeoVersion = 0
  expr: Constraints[1] = Spreadsheet.threeM_holes_slip_fit
  sketch-geometry (5):
    g0: Circle CenterX=-33 CenterY=53.5 CenterZ=0 NormalX=0 NormalY=0 NormalZ=1 AngleXU=0 Radius=1.6
    g1: Circle CenterX=33 CenterY=53.5 CenterZ=0 NormalX=0 NormalY=0 NormalZ=1 AngleXU=0 Radius=1.6
    g2: Circle CenterX=32.5 CenterY=-17.45 CenterZ=0 NormalX=0 NormalY=0 NormalZ=1 AngleXU=0 Radius=1.6
    g3: Circle CenterX=-20.25 CenterY=-17.45 CenterZ=0 NormalX=0 NormalY=0 NormalZ=1 AngleXU=0 Radius=1.6
    g4: Circle CenterX=32.5 CenterY=-51 CenterZ=0 NormalX=0 NormalY=0 NormalZ=1 AngleXU=0 Radius=1.6
  constraints (10):
    c: Coincident(g0,g-5)
    c: Diameter(g0) = 3.2
    c: Coincident(g1,g-4)
    c: Coincident(g4,g-3)
    c: Equal(g2,g1)
    c: Equal(g2,g3)
    c: Equal(g3,g4)
    c: Equal(g1,g0)
    c: Coincident(g3,g-6)
    c: Coincident(g-7,g2)
FEATURE [Sketcher::SketchObject] Sketch041
  ArcFitTolerance = 1e-06
  AttachmentSupport = -> [DatumPlane002]
  ExternalGeometry = -> [Revolution]
  ExternalTypes = [0]
  FullyConstrained = true
  MakeInternals = false
  MapMode = 5
  Placement = pos=(-3.3,-20,-19.15) rot=(1,0,0;3.14159rad)
  _ExternalGeoVersion = 0
  sketch-geometry (24):
    g0: LineSegment [constr] StartX=-8.75 StartY=3.36067 StartZ=0 EndX=1.25 EndY=3.36067 EndZ=0
    g1: LineSegment [constr] StartX=-3.75 StartY=-9.5 StartZ=0 EndX=-3.75 EndY=16.2213 EndZ=0
    g2: ArcOfCircle CenterX=-7.95 CenterY=3.36067 CenterZ=0 NormalX=0 NormalY=0 NormalZ=1 AngleXU=0 Radius=0.5 StartAngle=3.14159 EndAngle=6.28319
    g3: ArcOfCircle CenterX=-6.55 CenterY=3.36067 CenterZ=0 NormalX=0 NormalY=0 NormalZ=1 AngleXU=0 Radius=0.5 StartAngle=3.14159 EndAngle=6.28319
    g4: ArcOfCircle CenterX=-5.15 CenterY=3.36067 CenterZ=0 NormalX=0 NormalY=0 NormalZ=1 AngleXU=0 Radius=0.5 StartAngle=3.14159 EndAngle=6.28319
    g5: Circle [constr] CenterX=-7.95 CenterY=3.36067 CenterZ=0 NormalX=0 NormalY=0 NormalZ=1 AngleXU=0 Radius=1.4
    g6: Circle [constr] CenterX=-6.55 CenterY=3.36067 CenterZ=0 NormalX=0 NormalY=0 NormalZ=1 AngleXU=0 Radius=1.4
    g7: ArcOfCircle CenterX=-3.75 CenterY=3.36067 CenterZ=0 NormalX=0 NormalY=0 NormalZ=1 AngleXU=0 Radius=0.5 StartAngle=3.14159 EndAngle=6.28319
    g8: Circle [constr] CenterX=-5.15 CenterY=3.36067 CenterZ=0 NormalX=0 NormalY=0 NormalZ=1 AngleXU=0 Radius=1.4
    g9: ArcOfCircle CenterX=-7.25 CenterY=3.36067 CenterZ=0 NormalX=0 NormalY=0 NormalZ=1 AngleXU=0 Radius=0.2 StartAngle=0 EndAngle=3.14159
    g10: ArcOfCircle CenterX=-5.85 CenterY=3.36067 CenterZ=0 NormalX=0 NormalY=0 NormalZ=1 AngleXU=0 Radius=0.2 StartAngle=5e-16 EndAngle=3.14159
    g11: ArcOfCircle CenterX=-4.45 CenterY=3.36067 CenterZ=0 NormalX=0 NormalY=0 NormalZ=1 AngleXU=0 Radius=0.2 StartAngle=0 EndAngle=3.14159
    g12: ArcOfCircle CenterX=-2.35 CenterY=3.36067 CenterZ=0 NormalX=0 NormalY=0 NormalZ=1 AngleXU=0 Radius=0.5 StartAngle=3.14159 EndAngle=6.28319
    g13: ArcOfCircle CenterX=-0.95 CenterY=3.36067 CenterZ=0 NormalX=0 NormalY=0 NormalZ=1 AngleXU=0 Radius=0.5 StartAngle=3.14159 EndAngle=6.28319
    g14: ArcOfCircle CenterX=0.45 CenterY=3.36067 CenterZ=0 NormalX=0 NormalY=0 NormalZ=1 AngleXU=0 Radius=0.5 StartAngle=3.14159 EndAngle=6.28319
    g15: ArcOfCircle CenterX=-0.25 CenterY=3.36067 CenterZ=0 NormalX=0 NormalY=0 NormalZ=1 AngleXU=0 Radius=0.2 StartAngle=0 EndAngle=3.14159
    g16: ArcOfCircle CenterX=-1.65 CenterY=3.36067 CenterZ=0 NormalX=0 NormalY=0 NormalZ=1 AngleXU=0 Radius=0.2 StartAngle=2e-16 EndAngle=3.14159
    g17: ArcOfCircle CenterX=-3.05 CenterY=3.36067 CenterZ=0 NormalX=0 NormalY=0 NormalZ=1 AngleXU=0 Radius=0.2 StartAngle=0 EndAngle=3.14159
    g18: LineSegment [constr] StartX=1.25 StartY=16.2213 StartZ=0 EndX=1.25 EndY=-9.5 EndZ=0
    g19: GeomPoint [constr] X=1.25 Y=3.36067 Z=0
    g20: ArcOfCircle CenterX=-3.75 CenterY=3.36067 CenterZ=0 NormalX=0 NormalY=0 NormalZ=1 AngleXU=0 Radius=4.7 StartAngle=0 EndAngle=3.14159
    g21: Circle [constr] CenterX=-3.75 CenterY=3.36067 CenterZ=0 NormalX=0 NormalY=0 NormalZ=1 AngleXU=0 Radius=1.4
    g22: Circle [constr] CenterX=-2.35 CenterY=3.36067 CenterZ=0 NormalX=0 NormalY=0 NormalZ=1 AngleXU=0 Radius=1.4
    g23: Circle [constr] CenterX=-0.95 CenterY=3.36067 CenterZ=0 NormalX=0 NormalY=0 NormalZ=1 AngleXU=0 Radius=1.4
  constraints (76):
    c: Horizontal(g0)
    c: Vertical(g-3,g0)
    c: Symmetric(g0,g0,g-3)
    c: Vertical(g1)
    c: Symmetric(g1,g1,g-3)
    c: PointOnObject(g1,g-4)
    c: PointOnObject(g2,g0)
    c: PointOnObject(g2,g0)
    c: PointOnObject(g2,g0)
    c: PointOnObject(g3,g0)
    c: PointOnObject(g3,g0)
    c: PointOnObject(g3,g0)
    c: PointOnObject(g4,g0)
    c: Equal(g3,g2)
    c: Equal(g3,g4)
    c: PointOnObject(g4,g0)
    c: Radius(g2) = 0.5
    c: Coincident(g5,g2)
    c: PointOnObject(g3,g5)
    c: Coincident(g6,g3)
    c: PointOnObject(g4,g6)
    c: Equal(g5,g6)
    c: DistanceX(g0,g2) = 0.3
    c: PointOnObject(g4,g0)
    c: Coincident(g7,g-3)
    c: PointOnObject(g7,g0)
    c: Equal(g7,g4)
    c: Coincident(g8,g4)
    c: PointOnObject(g7,g8)
    c: Equal(g8,g6)
    c: PointOnObject(g9,g0)
    c: Coincident(g9,g2)
    c: Coincident(g9,g3)
    c: PointOnObject(g10,g0)
    c: Coincident(g10,g3)
    c: Coincident(g10,g4)
    c: PointOnObject(g11,g0)
    c: Coincident(g11,g4)
    c: Coincident(g11,g7)
    c: PointOnObject(g7,g0)
    c: PointOnObject(g12,g0)
    c: PointOnObject(g12,g0)
    c: PointOnObject(g12,g0)
    c: PointOnObject(g13,g0)
    c: PointOnObject(g13,g0)
    c: PointOnObject(g13,g0)
    c: PointOnObject(g14,g0)
    c: PointOnObject(g14,g0)
    c: PointOnObject(g14,g0)
    c: PointOnObject(g15,g0)
    c: Coincident(g15,g14)
    c: Coincident(g15,g13)
    c: PointOnObject(g16,g0)
    c: Coincident(g16,g13)
    c: Coincident(g16,g12)
    c: PointOnObject(g17,g0)
    c: Coincident(g17,g7)
    c: Coincident(g17,g12)
    c: Equal(g7,g12)
    c: Equal(g13,g12)
    c: Equal(g13,g14)
    c: Equal(g17,g11)
    c: Vertical(g18)
    c: Symmetric(g18,g18,g19)
    c: Horizontal(g18,g-4)
    c: Coincident(g20,g7)
    c: Coincident(g20,g2)
    c: Coincident(g20,g14)
    c: Coincident(g21,g7)
    c: PointOnObject(g12,g21)
    c: Coincident(g22,g12)
    c: PointOnObject(g13,g22)
    c: Coincident(g23,g13)
    c: PointOnObject(g14,g23)
    c: Equal(g21,g22)
    c: Coincident(g0,g19)
FEATURE [PartDesign::Groove] Groove
  Angle = 360
  Angle2 = 60
  Axis = (0,25.7213,0)
  Base = (-2.05,-36.2213,-19.15)
  BaseFeature = -> Revolution
  Placement = pos=(-3.3,-20,-19.15) rot=(1,0,0;3.14159rad)
  Profile = -> Sketch041
  ReferenceAxis = -> Sketch041 [Axis2]
  Refine = true
  Suppressed = false
  Type = 0
FEATURE [PartDesign::Pocket] Pocket010
  BaseFeature = -> Groove
  Direction = (0,-1,-2e-16)
  Length = 4
  Length2 = 5
  Placement = pos=(-3.3,-20,-19.15) rot=(1,0,0;3.14159rad)
  Profile = -> Sketch032
  ReferenceAxis = -> Sketch032 [N_Axis]
  Refine = true
  SideType = 0
  Suppressed = false
  Type = 0
  Type2 = 0
FEATURE [Sketcher::SketchObject] Sketch033
  ArcFitTolerance = 1e-06
  AttachmentSupport = -> [Pocket010]
  ExternalTypes = [0]
  FullyConstrained = true
  MakeInternals = false
  MapMode = 5
  Placement = pos=(-3.3,-10.5,-19.15) rot=(-1,0,0;1.5708rad)
  _ExternalGeoVersion = 0
  sketch-geometry (4):
    g0: Circle CenterX=-3.75 CenterY=-1.41421 CenterZ=0 NormalX=0 NormalY=0 NormalZ=1 AngleXU=0 Radius=0.25
    g1: Circle CenterX=-2.33579 CenterY=0 CenterZ=0 NormalX=0 NormalY=0 NormalZ=1 AngleXU=0 Radius=0.25
    g2: Circle CenterX=-5.16421 CenterY=0 CenterZ=0 NormalX=0 NormalY=0 NormalZ=1 AngleXU=0 Radius=0.25
    g3: Circle CenterX=-3.75 CenterY=1.41421 CenterZ=0 NormalX=0 NormalY=0 NormalZ=1 AngleXU=0 Radius=0.25
  constraints (8):
    c: Coincident(g0,g-6)
    c: Coincident(g1,g-6)
    c: Coincident(g2,g-5)
    c: Diameter(g3) = 0.5
    c: Coincident(g3,g-4)
    c: Equal(g2,g3)
    c: Equal(g1,g3)
    c: Equal(g0,g1)
FEATURE [PartDesign::Pocket] Pocket011
  BaseFeature = -> Pocket010
  Direction = (0,-1,-2e-16)
  Length = 5
  Length2 = 5
  Placement = pos=(-3.3,-20,-19.15) rot=(1,0,0;3.14159rad)
  Profile = -> Sketch033
  ReferenceAxis = -> Sketch033 [N_Axis]
  Refine = true
  SideType = 0
  Suppressed = false
  Type = 2
  Type2 = 0
FEATURE [PartDesign::Chamfer] Chamfer
  Angle = 45
  Base = -> Pocket011 [Edge1]
  BaseFeature = -> Pocket011
  ChamferType = 0
  FlipDirection = false
  Placement = pos=(-3.3,-20,-19.15) rot=(1,0,0;3.14159rad)
  Refine = true
  Size = 1
  Size2 = 1
  SupportTransform = false
  Suppressed = false
  UseAllEdges = false
FEATURE [PartDesign::Body] Body009  label="joystick"
  AllowCompound = false
  Group = -> [DatumPlane002,Binder003,Sketch026,Revolution,Sketch041,Groove,Sketch032,Pocket010,Sketch033,Pocket011,Chamfer]
  Origin = -> Origin081
  Tip = -> Chamfer
FEATURE [PartDesign::Pocket] Pocket014
  BaseFeature = -> Pocket006
  Direction = (0,1,-1.1e-15)
  Length = 1.5
  Length2 = 5
  Placement = pos=(0,-18.5,4.1e-15) rot=(1,0,0;1.5708rad)
  Profile = -> Sketch040
  ReferenceAxis = -> Sketch040 [N_Axis]
  Refine = true
  SideType = 0
  Suppressed = false
  Type = 0
  Type2 = 0
  expr: Length = Spreadsheet.Wall
FEATURE [PartDesign::Body] Body007  label="LID"
  AllowCompound = false
  Group = -> [Binder,DatumPlane,Sketch014,Pad011,Sketch015,Pocket003,LinearPattern,Sketch016,Sketch017,Pad012,Chamfer002,LinearPattern001,Pad013,Fillet,Fillet001,LinearPattern003,Sketch020,Pocket005,Sketch021,Pad015,Binder001,Sketch023,Sketch039,Pocket013,Pocket006,Binder005,Sketch040,Pocket014]
  Origin = -> Origin077
  Tip = -> Pocket014
FEATURE [Sketcher::SketchObject] Sketch005
  ArcFitTolerance = 1e-06
  AttachmentSupport = -> [Thickness]
  ExternalTypes = [0]
  FullyConstrained = true
  MakeInternals = false
  MapMode = 5
  Placement = pos=(0,-1.5,3e-16) rot=(1,0,0;1.5708rad)
  _ExternalGeoVersion = 0
  expr: Constraints[12] = Spreadsheet.twoM_holes_thread
  sketch-geometry (18):
    g0: LineSegment StartX=32.5 StartY=-53.5 StartZ=0 EndX=36 EndY=-53.5 EndZ=0
    g1: LineSegment StartX=36 StartY=-53.5 StartZ=0 EndX=36 EndY=-48.5 EndZ=0
    g2: LineSegment StartX=36 StartY=-48.5 StartZ=0 EndX=32.5 EndY=-48.5 EndZ=0
    g3: ArcOfCircle CenterX=32.5 CenterY=-51 CenterZ=0 NormalX=0 NormalY=0 NormalZ=1 AngleXU=0 Radius=2.5 StartAngle=1.5708 EndAngle=4.71239
    g4: Circle CenterX=32.5 CenterY=-51 CenterZ=0 NormalX=0 NormalY=0 NormalZ=1 AngleXU=0 Radius=0.85
    g5: Circle CenterX=-10.56 CenterY=-51 CenterZ=0 NormalX=0 NormalY=0 NormalZ=1 AngleXU=0 Radius=0.85
    g6: Circle CenterX=-10.56 CenterY=-51 CenterZ=0 NormalX=0 NormalY=0 NormalZ=1 AngleXU=0 Radius=2.5
    g7: Circle CenterX=-10.56 CenterY=-4 CenterZ=0 NormalX=0 NormalY=0 NormalZ=1 AngleXU=0 Radius=0.85
    g8: Circle CenterX=-10.56 CenterY=-4 CenterZ=0 NormalX=0 NormalY=0 NormalZ=1 AngleXU=0 Radius=2.5
    g9: Circle CenterX=32.5 CenterY=-4 CenterZ=0 NormalX=0 NormalY=0 NormalZ=1 AngleXU=0 Radius=0.85
    g10: LineSegment [constr] StartX=-10.56 StartY=-51 StartZ=0 EndX=32.5 EndY=-51 EndZ=0
    g11: LineSegment [constr] StartX=32.5 StartY=-51 StartZ=0 EndX=32.5 EndY=-4 EndZ=0
    g12: LineSegment [constr] StartX=32.5 StartY=-4 StartZ=0 EndX=-10.56 EndY=-4 EndZ=0
    g13: LineSegment [constr] StartX=-10.56 StartY=-4 StartZ=0 EndX=-10.56 EndY=-51 EndZ=0
    g14: LineSegment StartX=32.5 StartY=-1.5 StartZ=0 EndX=36 EndY=-1.5 EndZ=0
    g15: LineSegment StartX=36 StartY=-1.5 StartZ=0 EndX=36 EndY=-6.5 EndZ=0
    g16: LineSegment StartX=36 StartY=-6.5 StartZ=0 EndX=32.5 EndY=-6.5 EndZ=0
    g17: ArcOfCircle CenterX=32.5 CenterY=-4 CenterZ=0 NormalX=0 NormalY=0 NormalZ=1 AngleXU=0 Radius=2.5 StartAngle=1.5708 EndAngle=4.71239
  constraints (47):
    c: PointOnObject(g0,g-3)
    c: Horizontal(g0)
    c: Coincident(g0,g1)
    c: PointOnObject(g1,g-3)
    c: Coincident(g1,g2)
    c: Horizontal(g2)
    c: Vertical(g0,g2)
    c: Coincident(g3,g0)
    c: Tangent(g3,g2) = -1.5708
    c: Coincident(g4,g3)
    c: DistanceY(g0,g2) = 5
    c: DistanceX(g3,g1) = 3.5
    c: Diameter(g4) = 1.7
    c: Coincident(g6,g5)
    c: Coincident(g8,g7)
    c: Equal(g4,g5)
    c: Equal(g4,g7)
    c: Equal(g3,g6)
    c: Equal(g3,g8)
    c: Coincident(g10,g11)
    c: Coincident(g11,g12)
    c: Coincident(g12,g13)
    c: Coincident(g13,g10)
    c: Horizontal(g10)
    c: Horizontal(g12)
    c: Vertical(g11)
    c: Vertical(g13)
    c: Coincident(g10,g5)
    c: Coincident(g11,g9)
    c: Coincident(g7,g12)
    c: Coincident(g10,g3)
    c: DistanceX(g5,g3) = 43.06
    c: DistanceY(g3,g9) = 47
    c: Equal(g9,g4)
    c: Horizontal(g14)
    c: Coincident(g14,g15)
    c: Coincident(g15,g16)
    c: Horizontal(g16)
    c: Vertical(g14,g16)
    c: Vertical(g9,g14)
    c: PointOnObject(g14,g-3)
    c: PointOnObject(g15,g-3)
    c: Coincident(g17,g9)
    c: Coincident(g17,g14)
    c: Coincident(g17,g16)
    c: Equal(g17,g3)
    c: DistanceY(g-4,g3) = 5.5
FEATURE [PartDesign::Pad] Pad005  label="Wio holes"
  BaseFeature = -> Thickness
  Direction = (0,-1,2e-16)
  Length = 4
  Length2 = 10
  Profile = -> Sketch005
  ReferenceAxis = -> Sketch005 [N_Axis]
  Refine = true
  SideType = 0
  Suppressed = false
  Type = 0
  Type2 = 0
FEATURE [Sketcher::SketchObject] Sketch006
  ArcFitTolerance = 1e-06
  AttachmentSupport = -> [Pad005]
  ExternalTypes = [0]
  FullyConstrained = true
  MakeInternals = false
  MapMode = 5
  Placement = pos=(37.5,0,0) rot=(0.57735,0.57735,0.57735;2.0944rad)
  _ExternalGeoVersion = 0
  expr: Constraints[43] = Spreadsheet.Tolerance
  sketch-geometry (20):
    g0: LineSegment [constr] StartX=-10.47 StartY=-16.43 StartZ=0 EndX=-10.47 EndY=-22.87 EndZ=0
    g1: LineSegment [constr] StartX=-9.19 StartY=-24.15 StartZ=0 EndX=-8.55 EndY=-24.15 EndZ=0
    g2: LineSegment [constr] StartX=-7.27 StartY=-22.87 StartZ=0 EndX=-7.27 EndY=-16.43 EndZ=0
    g3: LineSegment [constr] StartX=-8.55 StartY=-15.15 StartZ=0 EndX=-9.19 EndY=-15.15 EndZ=0
    g4: ArcOfCircle [constr] CenterX=-9.19 CenterY=-16.43 CenterZ=0 NormalX=0 NormalY=0 NormalZ=1 AngleXU=0 Radius=1.28 StartAngle=1.5708 EndAngle=3.14159
    g5: GeomPoint [constr] X=-10.47 Y=-15.15 Z=0
    g6: ArcOfCircle [constr] CenterX=-8.55 CenterY=-16.43 CenterZ=0 NormalX=0 NormalY=0 NormalZ=1 AngleXU=0 Radius=1.28 StartAngle=1.2e-15 EndAngle=1.5708
    g7: GeomPoint [constr] X=-7.27 Y=-15.15 Z=0
    g8: ArcOfCircle [constr] CenterX=-8.55 CenterY=-22.87 CenterZ=0 NormalX=0 NormalY=0 NormalZ=1 AngleXU=0 Radius=1.28 StartAngle=4.71239 EndAngle=6.28319
    g9: GeomPoint [constr] X=-7.27 Y=-24.15 Z=0
    g10: ArcOfCircle [constr] CenterX=-9.19 CenterY=-22.87 CenterZ=0 NormalX=0 NormalY=0 NormalZ=1 AngleXU=0 Radius=1.28 StartAngle=3.14159 EndAngle=4.71239
    g11: GeomPoint [constr] X=-10.47 Y=-24.15 Z=0
    g12: ArcOfCircle CenterX=-9.19 CenterY=-22.87 CenterZ=0 NormalX=0 NormalY=0 NormalZ=1 AngleXU=0 Radius=1.48 StartAngle=3.14159 EndAngle=4.71239
    g13: LineSegment StartX=-9.19 StartY=-24.35 StartZ=0 EndX=-8.55 EndY=-24.35 EndZ=0
    g14: ArcOfCircle CenterX=-8.55 CenterY=-22.87 CenterZ=0 NormalX=0 NormalY=0 NormalZ=1 AngleXU=0 Radius=1.48 StartAngle=4.71239 EndAngle=6.28319
    g15: LineSegment StartX=-7.07 StartY=-22.87 StartZ=0 EndX=-7.07 EndY=-16.43 EndZ=0
    g16: ArcOfCircle CenterX=-8.55 CenterY=-16.43 CenterZ=0 NormalX=0 NormalY=0 NormalZ=1 AngleXU=0 Radius=1.48 StartAngle=0 EndAngle=1.5708
    g17: LineSegment StartX=-8.55 StartY=-14.95 StartZ=0 EndX=-9.19 EndY=-14.95 EndZ=0
    g18: ArcOfCircle CenterX=-9.19 CenterY=-16.43 CenterZ=0 NormalX=0 NormalY=0 NormalZ=1 AngleXU=0 Radius=1.48 StartAngle=1.5708 EndAngle=3.14159
    g19: LineSegment StartX=-10.67 StartY=-16.43 StartZ=0 EndX=-10.67 EndY=-22.87 EndZ=0
  constraints (44):
    c: Vertical(g0)
    c: Vertical(g2)
    c: Horizontal(g1)
    c: Horizontal(g3)
    c: DistanceY(g11,g5) = 9
    c: DistanceX(g11,g9) = 3.2
    c: PointOnObject(g5,g0)
    c: PointOnObject(g5,g3)
    c: Tangent(g0,g4) = -1.5708
    c: Tangent(g3,g4) = -1.5708
    c: PointOnObject(g7,g3)
    c: PointOnObject(g7,g2)
    c: Tangent(g3,g6) = -1.5708
    c: Tangent(g2,g6) = -1.5708
    c: PointOnObject(g9,g2)
    c: PointOnObject(g9,g1)
    c: Tangent(g2,g8) = -1.5708
    c: Tangent(g1,g8) = -1.5708
    c: PointOnObject(g11,g1)
    c: PointOnObject(g11,g0)
    c: Tangent(g1,g10) = -1.5708
    c: Tangent(g0,g10) = -1.5708
    c: Equal(g4,g6)
    c: Equal(g6,g8)
    c: Equal(g8,g10)
    c: Radius(g10) = 1.28
    c: Distance(g2,g-3) = 5.77
    c: Distance(g9,g-4) = 26.85
    c: Tangent(g12,g13) = -1.5708
    c: Tangent(g12,g19) = -1.5708
    c: Tangent(g13,g14) = -1.5708
    c: Tangent(g14,g15) = -1.5708
    c: Tangent(g15,g16) = -1.5708
    c: Tangent(g16,g17) = -1.5708
    c: Tangent(g17,g18) = -1.5708
    c: Tangent(g18,g19) = -1.5708
    c: Parallel(g19,g0)
    c: Coincident(g12,g10)
    c: Parallel(g13,g1)
    c: Coincident(g14,g8)
    c: Parallel(g15,g2)
    c: Coincident(g16,g6)
    c: Coincident(g18,g4)
    c: Distance(g18,g4) = 0.2
FEATURE [PartDesign::Chamfer] Chamfer001
  Angle = 45
  Base = -> Pad005 [Edge93,Edge99,Edge110,Edge109]
  BaseFeature = -> Pad005
  ChamferType = 0
  FlipDirection = false
  Refine = true
  Size = 0.5
  Size2 = 1
  SupportTransform = false
  Suppressed = false
  UseAllEdges = false
FEATURE [PartDesign::SubShapeBinder] Binder007
  BindCopyOnChange = 0
  BindMode = 0
  ClaimChildren = false
  Context = -> Part002 [Part001.Body010.Binder007.]
  Fuse = false
  MakeFace = true
  OffsetFill = false
  OffsetIntersection = false
  OffsetJoinType = 0
  OffsetOpenResult = false
  PartialLoad = false
  Refine = true
  Relative = true
  Support = -> [Body002[Fillet008.]]
  _Version = 2
FEATURE [Sketcher::SketchObject] Sketch044
  ArcFitTolerance = 1e-06
  AttachmentSupport = -> [Pad024]
  ExternalGeometry = -> [Binder007]
  ExternalTypes = [1]
  FullyConstrained = true
  MakeInternals = false
  MapMode = 5
  Placement = pos=(-3.71565e-11,-2.55e-14,-58) rot=(0,0,1;3.14159rad)
  _ExternalGeoVersion = 0
  sketch-geometry (1):
    g0: Circle CenterX=25.5 CenterY=8.5 CenterZ=0 NormalX=0 NormalY=0 NormalZ=1 AngleXU=0 Radius=6
  constraints (2):
    c: Diameter(g0) = 12
    c: Coincident(g-3,g0)
FEATURE [PartDesign::Pocket] Pocket015
  BaseFeature = -> Pad024
  Direction = (-6.406e-13,0,-1)
  Length = 5
  Length2 = 5
  Placement = pos=(0,0,0) rot=(1,0,0;1.5708rad)
  Profile = -> Sketch044
  ReferenceAxis = -> Sketch044 [N_Axis]
  Refine = true
  SideType = 0
  Suppressed = false
  Type = 2
  Type2 = 0
FEATURE [PartDesign::SubShapeBinder] Binder008
  BindCopyOnChange = 0
  BindMode = 0
  ClaimChildren = false
  Context = -> Part002 [Part001.Body010.Binder008.]
  Fuse = false
  MakeFace = true
  OffsetFill = false
  OffsetIntersection = false
  OffsetJoinType = 0
  OffsetOpenResult = false
  PartialLoad = false
  Refine = true
  Relative = true
  Support = -> [Body002[Fillet008.,Fillet008.,Fillet008.,Fillet008.,Fillet008.,Fillet008.,Fillet008.,Fillet008.]]
  _Version = 2
FEATURE [Sketcher::SketchObject] Sketch045
  ArcFitTolerance = 1e-06
  AttachmentSupport = -> [Pocket015]
  ExternalGeometry = -> [Binder008]
  ExternalTypes = [0]
  FullyConstrained = true
  MakeInternals = false
  MapMode = 5
  Placement = pos=(37.5,0,2.5845e-12) rot=(0.707107,0,-0.707107;3.14159rad)
  _ExternalGeoVersion = 0
  sketch-geometry (29):
    g0: LineSegment [constr] StartX=16.43 StartY=7.07 StartZ=0 EndX=22.87 EndY=10.67 EndZ=0
    g1: GeomPoint [constr] X=19.65 Y=8.87 Z=0
    g2: LineSegment [constr] StartX=13.65 StartY=5.37 StartZ=0 EndX=25.65 EndY=5.37 EndZ=0
    g3: LineSegment [constr] StartX=25.65 StartY=5.37 StartZ=0 EndX=25.65 EndY=12.37 EndZ=0
    g4: LineSegment [constr] StartX=25.65 StartY=12.37 StartZ=0 EndX=13.65 EndY=12.37 EndZ=0
    g5: LineSegment [constr] StartX=13.65 StartY=12.37 StartZ=0 EndX=13.65 EndY=5.37 EndZ=0
    g6: GeomPoint [constr] X=19.65 Y=8.87 Z=0
    g7: LineSegment StartX=13.35 StartY=5.07 StartZ=0 EndX=25.95 EndY=5.07 EndZ=0
    g8: LineSegment StartX=25.95 StartY=5.07 StartZ=0 EndX=25.95 EndY=6.07 EndZ=0
    g9: LineSegment StartX=25.95 StartY=6.07 StartZ=0 EndX=37.25 EndY=6.07 EndZ=0
    g10: LineSegment StartX=37.25 StartY=6.07 StartZ=0 EndX=37.25 EndY=11.67 EndZ=0
    g11: LineSegment StartX=37.25 StartY=11.67 StartZ=0 EndX=25.95 EndY=11.67 EndZ=0
    g12: LineSegment StartX=25.95 StartY=11.67 StartZ=0 EndX=25.95 EndY=12.67 EndZ=0
    g13: LineSegment StartX=25.95 StartY=12.67 StartZ=0 EndX=13.35 EndY=12.67 EndZ=0
    g14: LineSegment [constr] StartX=19.65 StartY=12.67 StartZ=0 EndX=19.65 EndY=5.07 EndZ=0
    g15: LineSegment [constr] StartX=36.95 StartY=8.87 StartZ=0 EndX=37.25 EndY=8.87 EndZ=0
    g16: LineSegment [constr] StartX=33.45 StartY=11.37 StartZ=0 EndX=33.45 EndY=11.67 EndZ=0
    g17: LineSegment [constr] StartX=25.65 StartY=12.37 StartZ=0 EndX=25.65 EndY=12.67 EndZ=0
    g18: LineSegment [constr] StartX=25.65 StartY=12.37 StartZ=0 EndX=25.95 EndY=12.37 EndZ=0
    g19: ArcOfCircle CenterX=9 CenterY=7.7 CenterZ=0 NormalX=0 NormalY=0 NormalZ=1 AngleXU=0 Radius=1.3 StartAngle=1.5708 EndAngle=4.71239
    g20: LineSegment StartX=9 StartY=9 StartZ=0 EndX=13.35 EndY=9 EndZ=0
    g21: LineSegment StartX=9 StartY=6.4 StartZ=0 EndX=13.35 EndY=6.4 EndZ=0
    g22: LineSegment StartX=13.35 StartY=9 StartZ=0 EndX=13.35 EndY=12.67 EndZ=0
    g23: LineSegment StartX=13.35 StartY=6.4 StartZ=0 EndX=13.35 EndY=5.07 EndZ=0
    g24: LineSegment [constr] StartX=8 StartY=7.7 StartZ=0 EndX=7.7 EndY=7.7 EndZ=0
    g25: ArcOfCircle CenterX=42.6 CenterY=8.91 CenterZ=0 NormalX=0 NormalY=0 NormalZ=1 AngleXU=0 Radius=1 StartAngle=1.5708 EndAngle=4.71239
    g26: ArcOfCircle CenterX=44.1 CenterY=8.91 CenterZ=0 NormalX=0 NormalY=0 NormalZ=1 AngleXU=0 Radius=1 StartAngle=4.71239 EndAngle=7.85398
    g27: LineSegment StartX=42.6 StartY=9.91 StartZ=0 EndX=44.1 EndY=9.91 EndZ=0
    g28: LineSegment StartX=42.6 StartY=7.91 StartZ=0 EndX=44.1 EndY=7.91 EndZ=0
  constraints (73):
    c: Coincident(g0,g-10)
    c: Coincident(g0,g-7)
    c: Symmetric(g0,g0,g1)
    c: Coincident(g2,g3)
    c: Coincident(g3,g4)
    c: Coincident(g4,g5)
    c: Coincident(g5,g2)
    c: Horizontal(g2)
    c: Horizontal(g4)
    c: Vertical(g3)
    c: Vertical(g5)
    c: Symmetric(g4,g2,g6)
    c: Distance(g3,g5) = 12
    c: Distance(g2,g4) = 7
    c: Coincident(g6,g1)
    c: Horizontal(g7)
    c: Coincident(g7,g8)
    c: Vertical(g8)
    c: Coincident(g8,g9)
    c: Horizontal(g9)
    c: Coincident(g9,g10)
    c: Vertical(g10)
    c: Coincident(g10,g11)
    c: Horizontal(g11)
    c: Coincident(g11,g12)
    c: Vertical(g12)
    c: Coincident(g12,g13)
    c: Horizontal(g13)
    c: Vertical(g11,g8)
    c: PointOnObject(g14,g7)
    c: Vertical(g14)
    c: Symmetric(g14,g14,g1)
    c: Symmetric(g-16,g-16,g15)
    c: Symmetric(g10,g10,g15)
    c: Horizontal(g15)
    c: Symmetric(g-14,g-14,g16)
    c: PointOnObject(g16,g11)
    c: Vertical(g16)
    c: Equal(g16,g15)
    c: Symmetric(g13,g13,g14)
    c: DistanceX(g-16,g10) = 0.3
    c: Coincident(g17,g3)
    c: PointOnObject(g17,g13)
    c: Vertical(g17)
    c: Coincident(g18,g3)
    c: PointOnObject(g18,g12)
    c: Horizontal(g18)
    c: Equal(g18,g17)
    c: Equal(g18,g15)
    c: Tangent(g19,g20) = 1.5708
    c: Tangent(g19,g21) = -1.5708
    c: Coincident(g19,g-26)
    c: Horizontal(g20)
    c: Coincident(g22,g20)
    c: Coincident(g22,g13)
    c: Coincident(g23,g21)
    c: Coincident(g23,g7)
    c: Vertical(g23)
    c: Vertical(g22)
    c: PointOnObject(g24,g-26)
    c: PointOnObject(g24,g19)
    c: Horizontal(g24)
    c: Horizontal(g24,g19)
    c: Equal(g24,g18)
    c: Horizontal(g21)
    c: Vertical(g21,g20)
    c: Tangent(g25,g27) = 1.5708
    c: Tangent(g25,g28) = -1.5708
    c: Tangent(g26,g27) = 1.5708
    c: Tangent(g26,g28) = -1.5708
    c: Coincident(g-21,g25)
    c: Coincident(g26,g-23)
    c: Coincident(g-23,g26)
FEATURE [PartDesign::Pocket] Pocket016
  BaseFeature = -> Pocket015
  Direction = (1,0,6.89e-14)
  Length = 5
  Length2 = 5
  Placement = pos=(0,0,0) rot=(1,0,0;1.5708rad)
  Profile = -> Sketch045
  ReferenceAxis = -> Sketch045 [N_Axis]
  Refine = true
  SideType = 0
  Suppressed = false
  Type = 2
  Type2 = 0
FEATURE [PartDesign::Fillet] Fillet009
  Base = -> Pocket016 [Edge82,Edge84,Edge80,Edge76,Edge78,Edge74,Edge69,Edge72,Edge86,Edge88]
  BaseFeature = -> Pocket016
  Placement = pos=(0,0,0) rot=(1,0,0;1.5708rad)
  Radius = 0.499
  Refine = true
  SupportTransform = false
  Suppressed = false
  UseAllEdges = false
FEATURE [Sketcher::SketchObject] Sketch046
  ArcFitTolerance = 1e-06
  AttachmentSupport = -> [Fillet009]
  ExternalTypes = [0]
  FullyConstrained = true
  MakeInternals = false
  MapMode = 5
  Placement = pos=(39,0,0) rot=(0.707107,0,0.707107;3.14159rad)
  _ExternalGeoVersion = 0
  sketch-geometry (12):
    g0: LineSegment StartX=-36.751 StartY=11.67 StartZ=0 EndX=-26.449 EndY=11.67 EndZ=0
    g1: LineSegment StartX=-36.751 StartY=6.07 StartZ=0 EndX=-26.449 EndY=6.07 EndZ=0
    g2: LineSegment StartX=-37.25 StartY=6.569 StartZ=0 EndX=-37.25 EndY=11.171 EndZ=0
    g3: ArcOfCircle CenterX=-36.751 CenterY=11.171 CenterZ=0 NormalX=0 NormalY=0 NormalZ=1 AngleXU=0 Radius=0.499 StartAngle=1.5708 EndAngle=3.14159
    g4: ArcOfCircle CenterX=-36.751 CenterY=6.569 CenterZ=0 NormalX=0 NormalY=0 NormalZ=1 AngleXU=0 Radius=0.499 StartAngle=3.14159 EndAngle=4.71239
    g5: ArcOfCircle CenterX=-26.449 CenterY=12.169 CenterZ=0 NormalX=0 NormalY=0 NormalZ=1 AngleXU=0 Radius=0.499 StartAngle=4.71239 EndAngle=7.85398
    g6: ArcOfCircle CenterX=-26.449 CenterY=5.571 CenterZ=0 NormalX=0 NormalY=0 NormalZ=1 AngleXU=0 Radius=0.499 StartAngle=4.71239 EndAngle=7.85398
    g7: ArcOfCircle CenterX=-36.751 CenterY=11.171 CenterZ=0 NormalX=0 NormalY=0 NormalZ=1 AngleXU=0 Radius=1.497 StartAngle=1.5708 EndAngle=3.14159
    g8: ArcOfCircle CenterX=-36.751 CenterY=6.569 CenterZ=0 NormalX=0 NormalY=0 NormalZ=1 AngleXU=0 Radius=1.497 StartAngle=3.14159 EndAngle=4.71239
    g9: LineSegment StartX=-36.751 StartY=12.668 StartZ=0 EndX=-26.449 EndY=12.668 EndZ=0
    g10: LineSegment StartX=-26.449 StartY=5.072 StartZ=0 EndX=-36.751 EndY=5.072 EndZ=0
    g11: LineSegment StartX=-38.248 StartY=6.569 StartZ=0 EndX=-38.248 EndY=11.171 EndZ=0
  constraints (29):
    c: Coincident(g0,g-6)
    c: Coincident(g0,g-4)
    c: Coincident(g1,g-8)
    c: Coincident(g1,g-9)
    c: Coincident(g2,g-8)
    c: Coincident(g2,g-6)
    c: Coincident(g3,g2)
    c: Coincident(g3,g0)
    c: Coincident(g4,g2)
    c: Coincident(g4,g1)
    c: Tangent(g-8,g4)
    c: Tangent(g-6,g3)
    c: Coincident(g5,g0)
    c: Coincident(g6,g1)
    c: Tangent(g-4,g5) = -1.5708
    c: Tangent(g-9,g6) = -1.5708
    c: Vertical(g1,g6)
    c: Vertical(g5,g0)
    c: Coincident(g7,g3)
    c: Coincident(g8,g4)
    c: Coincident(g9,g7)
    c: Coincident(g9,g5)
    c: Horizontal(g9)
    c: Coincident(g10,g6)
    c: Horizontal(g10)
    c: Vertical(g11)
    c: Tangent(g10,g8) = 1.5708
    c: Tangent(g11,g8) = 1.5708
    c: Tangent(g11,g7) = 1.5708
FEATURE [PartDesign::Pad] Pad026
  BaseFeature = -> Fillet009
  Direction = (1,0,-2e-16)
  Length = 1
  Length2 = 10
  Placement = pos=(0,0,0) rot=(1,0,0;1.5708rad)
  Profile = -> Sketch046
  ReferenceAxis = -> Sketch046 [N_Axis]
  Refine = true
  SideType = 0
  Suppressed = false
  Type = 0
  Type2 = 0
FEATURE [PartDesign::Chamfer] Chamfer003
  Angle = 45
  Base = -> Pad026 [Edge17]
  BaseFeature = -> Pad026
  ChamferType = 0
  FlipDirection = false
  Placement = pos=(0,0,0) rot=(1,0,0;1.5708rad)
  Refine = true
  Size = 0.6
  Size2 = 1
  SupportTransform = false
  Suppressed = false
  UseAllEdges = false
FEATURE [Sketcher::SketchObject] Sketch047
  ArcFitTolerance = 1e-06
  AttachmentSupport = -> [Chamfer003]
  ExternalTypes = [0]
  FullyConstrained = true
  MakeInternals = false
  MapMode = 5
  Placement = pos=(0,0,0) rot=(-1,0,0;1.5708rad)
  _ExternalGeoVersion = 0
  sketch-geometry (21):
    g0: LineSegment StartX=-35.5 StartY=59.5 StartZ=0 EndX=6.51788 EndY=59.5 EndZ=0
    g1: LineSegment StartX=13.5 StartY=66 StartZ=0 EndX=33.5 EndY=66 EndZ=0
    g2: LineSegment StartX=39 StartY=60.5 StartZ=0 EndX=39 EndY=-56 EndZ=0
    g3: LineSegment StartX=35.5 StartY=-59.5 StartZ=0 EndX=-35.5 EndY=-59.5 EndZ=0
    g4: LineSegment StartX=-39 StartY=-56 StartZ=0 EndX=-39 EndY=56 EndZ=0
    g5: ArcOfCircle CenterX=-35.5 CenterY=-56 CenterZ=0 NormalX=0 NormalY=0 NormalZ=1 AngleXU=0 Radius=3.50001 StartAngle=3.14159 EndAngle=4.71239
    g6: ArcOfCircle CenterX=35.5 CenterY=-56 CenterZ=0 NormalX=0 NormalY=0 NormalZ=1 AngleXU=0 Radius=3.50001 StartAngle=4.71239 EndAngle=6.28318
    g7: ArcOfCircle CenterX=33.5 CenterY=60.5 CenterZ=0 NormalX=0 NormalY=0 NormalZ=1 AngleXU=0 Radius=5.49999 StartAngle=6.28318 EndAngle=7.85398
    g8: ArcOfCircle CenterX=13.5 CenterY=60.5 CenterZ=0 NormalX=0 NormalY=0 NormalZ=1 AngleXU=0 Radius=5.5 StartAngle=1.5708 EndAngle=3.0701
    g9: ArcOfCircle CenterX=6.51787 CenterY=61 CenterZ=0 NormalX=0 NormalY=0 NormalZ=1 AngleXU=0 Radius=1.50001 StartAngle=4.71239 EndAngle=6.21169
    g10: ArcOfCircle CenterX=-35.5 CenterY=56 CenterZ=0 NormalX=0 NormalY=0 NormalZ=1 AngleXU=0 Radius=3.50001 StartAngle=1.5708 EndAngle=3.14159
    g11: LineSegment StartX=-34.5 StartY=56 StartZ=0 EndX=34.5 EndY=56 EndZ=0
    g12: LineSegment StartX=35.5 StartY=55 StartZ=0 EndX=35.5 EndY=-55 EndZ=0
    g13: LineSegment StartX=34.5 StartY=-56 StartZ=0 EndX=-34.5 EndY=-56 EndZ=0
    g14: LineSegment StartX=-35.5 StartY=-55 StartZ=0 EndX=-35.5 EndY=55 EndZ=0
    g15: ArcOfCircle CenterX=-34.5 CenterY=55 CenterZ=0 NormalX=0 NormalY=0 NormalZ=1 AngleXU=0 Radius=1 StartAngle=1.5708 EndAngle=3.14159
    g16: ArcOfCircle CenterX=34.5 CenterY=55 CenterZ=0 NormalX=0 NormalY=0 NormalZ=1 AngleXU=0 Radius=1 StartAngle=-3.6e-15 EndAngle=1.5708
    g17: ArcOfCircle CenterX=34.5 CenterY=-55 CenterZ=0 NormalX=0 NormalY=0 NormalZ=1 AngleXU=0 Radius=1 StartAngle=4.71239 EndAngle=6.28319
    g18: ArcOfCircle CenterX=-34.5 CenterY=-55 CenterZ=0 NormalX=0 NormalY=0 NormalZ=1 AngleXU=0 Radius=1 StartAngle=3.14159 EndAngle=4.71239
    g19: LineSegment [constr] StartX=-35.5 StartY=55 StartZ=0 EndX=-37.5 EndY=55 EndZ=0
    g20: LineSegment [constr] StartX=-34.5 StartY=56 StartZ=0 EndX=-34.5 EndY=58 EndZ=0
  constraints (52):
    c: Coincident(g0,g-4)
    c: Coincident(g0,g-6)
    c: Coincident(g1,g-8)
    c: Coincident(g1,g-9)
    c: Coincident(g4,g-13)
    c: Coincident(g4,g-5)
    c: Coincident(g-10,g2)
    c: Coincident(g-12,g3)
    c: Coincident(g-11,g2)
    c: Coincident(g-13,g3)
    c: Coincident(g5,g4)
    c: Coincident(g5,g3)
    c: Coincident(g6,g2)
    c: Coincident(g6,g3)
    c: Coincident(g7,g1)
    c: Coincident(g7,g2)
    c: Coincident(g8,g1)
    c: Coincident(g9,g0)
    c: Coincident(g10,g0)
    c: Coincident(g10,g4)
    c: Tangent(g-13,g5)
    c: Tangent(g-11,g6)
    c: Tangent(g-9,g7)
    c: Tangent(g8,g-7) = -1.5708
    c: Tangent(g-6,g9)
    c: Coincident(g9,g8)
    c: Tangent(g-4,g10)
    c: Horizontal(g11)
    c: Vertical(g12)
    c: Horizontal(g13)
    c: Vertical(g14)
    c: Tangent(g18,g13) = 1.5708
    c: Tangent(g18,g14) = 1.5708
    c: Tangent(g17,g13) = 1.5708
    c: Tangent(g17,g12) = 1.5708
    c: Tangent(g16,g11) = 1.5708
    c: Tangent(g16,g12) = 1.5708
    c: Tangent(g15,g11) = 1.5708
    c: Tangent(g15,g14) = 1.5708
    c: Equal(g15,g16)
    c: Equal(g17,g18)
    c: Equal(g18,g15)
    c: Symmetric(g17,g15,g-1)
    c: Radius(g16) = 1
    c: DistanceX(g-14,g14) = 2
    c: Coincident(g19,g14)
    c: PointOnObject(g19,g-14)
    c: Horizontal(g19)
    c: Coincident(g20,g11)
    c: PointOnObject(g20,g-15)
    c: Vertical(g20)
    c: Equal(g20,g19)
FEATURE [PartDesign::Pad] Pad027
  BaseFeature = -> Chamfer003
  Direction = (0,1,2e-16)
  Length = 0.001
  Length2 = 2.5
  Placement = pos=(0,0,0) rot=(1,0,0;1.5708rad)
  Profile = -> Sketch047
  ReferenceAxis = -> Sketch047 [N_Axis]
  Refine = true
  Reversed = true
  SideType = 1
  Suppressed = false
  Type = 0
  Type2 = 0
FEATURE [PartDesign::Fillet] Fillet010
  Base = -> Pad027 [Face49]
  BaseFeature = -> Pad027
  Placement = pos=(0,0,0) rot=(1,0,0;1.5708rad)
  Radius = 1
  Refine = true
  SupportTransform = false
  Suppressed = false
  UseAllEdges = false
FEATURE [PartDesign::Fillet] Fillet011
  Base = -> Fillet010 [Edge8]
  BaseFeature = -> Fillet010
  Placement = pos=(0,0,0) rot=(1,0,0;1.5708rad)
  Radius = 1.4
  Refine = true
  SupportTransform = false
  Suppressed = false
  UseAllEdges = false
FEATURE [Sketcher::SketchObject] Sketch048
  ArcFitTolerance = 1e-06
  AttachmentSupport = -> [XY_Plane083]
  ExternalTypes = [0]
  FullyConstrained = true
  MakeInternals = false
  MapMode = 5
  _ExternalGeoVersion = 0
  sketch-geometry (1):
    g0: Circle CenterX=0 CenterY=0 CenterZ=0 NormalX=0 NormalY=0 NormalZ=1 AngleXU=0 Radius=3.25
  constraints (2):
    c: Diameter(g0) = 6.5
    c: Coincident(g0,g-1)
FEATURE [PartDesign::Pad] Pad028
  Direction = (0,0,1)
  Length = 55
  Length2 = 10
  Profile = -> Sketch048
  ReferenceAxis = -> Sketch048 [N_Axis]
  Refine = true
  SideType = 0
  Suppressed = false
  Type = 0
  Type2 = 0
FEATURE [PartDesign::Fillet] Fillet012
  Base = -> Pad028 [Edge2]
  BaseFeature = -> Pad028
  Radius = 3
  Refine = true
  SupportTransform = false
  Suppressed = false
  UseAllEdges = false
FEATURE [PartDesign::Body] Body011  label="LoRa antenna"
  AllowCompound = false
  Group = -> [Sketch048,Pad028,Fillet012]
  Origin = -> Origin083
  Placement = pos=(-25.5,-10,-108.8) rot=(0,0,1;0rad)
  Tip = -> Fillet012
FEATURE [PartDesign::Fillet] Fillet013
  Base = -> Fillet011 [Edge277]
  BaseFeature = -> Fillet011
  Placement = pos=(0,0,0) rot=(1,0,0;1.5708rad)
  Radius = 1
  Refine = true
  SupportTransform = false
  Suppressed = false
  UseAllEdges = false
FEATURE [App::Point] Origin086  label="Origin"
  Role = Origin
FEATURE [App::Point] Origin087  label="Origin"
  Role = Origin
FEATURE [App::Point] Origin088  label="Origin"
  Role = Origin
FEATURE [App::Point] Origin089  label="Origin"
  Role = Origin
FEATURE [App::Point] Origin090  label="Origin"
  Role = Origin
FEATURE [App::Point] Origin091  label="Origin"
  Role = Origin
FEATURE [App::Point] Origin092  label="Origin"
  Role = Origin
FEATURE [App::Point] Origin093  label="Origin"
  Role = Origin
FEATURE [App::Point] Origin094  label="Origin"
  Role = Origin
FEATURE [App::Point] Origin095  label="Origin"
  Role = Origin
FEATURE [App::Point] Origin096  label="Origin"
  Role = Origin
FEATURE [App::Point] Origin097  label="Origin"
  Role = Origin
FEATURE [App::Point] Origin098  label="Origin"
  Role = Origin
FEATURE [App::Point] Origin099  label="Origin"
  Role = Origin
FEATURE [App::Point] Origin100  label="Origin"
  Role = Origin
FEATURE [App::Point] Origin101  label="Origin"
  Role = Origin
FEATURE [App::Point] Origin102  label="Origin"
  Role = Origin
FEATURE [App::Point] Origin103  label="Origin"
  Role = Origin
FEATURE [App::Point] Origin104  label="Origin"
  Role = Origin
FEATURE [App::Point] Origin105  label="Origin"
  Role = Origin
FEATURE [App::Point] Origin106  label="Origin"
  Role = Origin
FEATURE [App::Point] Origin107  label="Origin"
  Role = Origin
FEATURE [App::Point] Origin108  label="Origin"
  Role = Origin
FEATURE [App::Point] Origin109  label="Origin"
  Role = Origin
FEATURE [App::Point] Origin110  label="Origin"
  Role = Origin
FEATURE [App::Point] Origin111  label="Origin"
  Role = Origin
FEATURE [App::Point] Origin112  label="Origin"
  Role = Origin
FEATURE [App::Point] Origin113  label="Origin"
  Role = Origin
FEATURE [App::Point] Origin114  label="Origin"
  Role = Origin
FEATURE [App::Point] Origin115  label="Origin"
  Role = Origin
FEATURE [App::Point] Origin116  label="Origin"
  Role = Origin
FEATURE [App::Point] Origin117  label="Origin"
  Role = Origin
FEATURE [App::Point] Origin118  label="Origin"
  Role = Origin
FEATURE [PartDesign::Fillet] Fillet005
  Base = -> Chamfer001 [Edge30,Edge19,Edge17,Edge23,Edge9,Edge15]
  BaseFeature = -> Chamfer001
  Radius = 1
  Refine = true
  SupportTransform = false
  Suppressed = false
  UseAllEdges = false
FEATURE [PartDesign::Chamfer] Chamfer004
  Angle = 45
  Base = -> Fillet005 [Edge53,Edge54]
  BaseFeature = -> Fillet005
  ChamferType = 0
  FlipDirection = false
  Refine = true
  Size = 2.6
  Size2 = 1
  SupportTransform = false
  Suppressed = false
  UseAllEdges = false
FEATURE [PartDesign::Pocket] Pocket  label="USB-c"
  BaseFeature = -> Chamfer004
  Direction = (-1,0,0)
  Length = 0
  Length2 = 5
  Profile = -> Sketch006
  ReferenceAxis = -> Sketch006 [N_Axis]
  Refine = true
  SideType = 0
  Suppressed = false
  Type = 2
  Type2 = 0
FEATURE [Sketcher::SketchObject] Sketch009
  ArcFitTolerance = 1e-06
  AttachmentSupport = -> [Pocket]
  ExternalTypes = [0]
  FullyConstrained = true
  MakeInternals = false
  MapMode = 5
  Placement = pos=(37.5,0,0) rot=(0.57735,0.57735,0.57735;2.0944rad)
  _ExternalGeoVersion = 0
  sketch-geometry (8):
    g0: LineSegment StartX=-7.91 StartY=-44.1 StartZ=0 EndX=-7.91 EndY=-42.6 EndZ=0
    g1: LineSegment StartX=-9.91 StartY=-42.6 StartZ=0 EndX=-9.91 EndY=-44.1 EndZ=0
    g2: ArcOfCircle CenterX=-8.91 CenterY=-44.1 CenterZ=0 NormalX=0 NormalY=0 NormalZ=1 AngleXU=0 Radius=1 StartAngle=3.14159 EndAngle=4.71239
    g3: ArcOfCircle CenterX=-8.91 CenterY=-44.1 CenterZ=0 NormalX=0 NormalY=0 NormalZ=1 AngleXU=0 Radius=1 StartAngle=4.71239 EndAngle=6.28319
    g4: ArcOfCircle CenterX=-8.91 CenterY=-42.6 CenterZ=0 NormalX=0 NormalY=0 NormalZ=1 AngleXU=0 Radius=1 StartAngle=2.8e-15 EndAngle=1.5708
    g5: ArcOfCircle CenterX=-8.91 CenterY=-42.6 CenterZ=0 NormalX=0 NormalY=0 NormalZ=1 AngleXU=0 Radius=1 StartAngle=1.5708 EndAngle=3.14159
    g6: GeomPoint X=-9.91 Y=-43.35 Z=0
    g7: LineSegment [constr] StartX=-8.91 StartY=-41.6 StartZ=0 EndX=-8.91 EndY=-45.1 EndZ=0
  constraints (20):
    c: Tangent(g0,g3) = -1.5708
    c: Tangent(g0,g4) = -1.5708
    c: Tangent(g1,g5) = -1.5708
    c: Tangent(g1,g2) = -1.5708
    c: Vertical(g0)
    c: Vertical(g1)
    c: Equal(g2,g3)
    c: Equal(g3,g4)
    c: Equal(g4,g5)
    c: Coincident(g2,g3)
    c: DistanceX(g1,g0) = 2
    c: DistanceY(g2,g4) = 3.5
    c: Tangent(g5,g4) = -1.5708
    c: Distance(g4,g-3) = 7.41
    c: Symmetric(g1,g1,g6)
    c: DistanceY(g-4,g6) = 7.65
    c: Coincident(g7,g4)
    c: Coincident(g7,g2)
    c: Vertical(g7)
    c: PointOnObject(g4,g7)
FEATURE [PartDesign::Pocket] Pocket001  label="RST"
  BaseFeature = -> Pocket
  Direction = (-1,0,0)
  Length = 0
  Length2 = 5
  Profile = -> Sketch009
  ReferenceAxis = -> Sketch009 [N_Axis]
  Refine = true
  SideType = 0
  Suppressed = false
  Type = 2
  Type2 = 0
FEATURE [Sketcher::SketchObject] Sketch010
  ArcFitTolerance = 1e-06
  AttachmentSupport = -> [Pocket001]
  ExternalTypes = [0]
  FullyConstrained = true
  MakeInternals = false
  MapMode = 5
  Placement = pos=(36,0,0) rot=(0.57735,-0.57735,-0.57735;2.0944rad)
  _ExternalGeoVersion = 0
  sketch-geometry (4):
    g0: LineSegment StartX=1.5 StartY=-10 StartZ=0 EndX=1.5 EndY=-11 EndZ=0
    g1: LineSegment StartX=1.5 StartY=-11 StartZ=0 EndX=11.5 EndY=-11 EndZ=0
    g2: LineSegment StartX=11.5 StartY=-11 StartZ=0 EndX=11.5 EndY=-10 EndZ=0
    g3: LineSegment StartX=11.5 StartY=-10 StartZ=0 EndX=1.5 EndY=-10 EndZ=0
  constraints (12):
    c: Coincident(g0,g1)
    c: Coincident(g1,g2)
    c: Coincident(g2,g3)
    c: Coincident(g3,g0)
    c: Vertical(g0)
    c: Vertical(g2)
    c: Horizontal(g1)
    c: Horizontal(g3)
    c: Distance(g0,g2) = 10
    c: Distance(g1,g3) = 1
    c: PointOnObject(g0,g-3)
    c: Distance(g-4,g3) = 6
FEATURE [PartDesign::Pad] Pad008  label="LED separation"
  BaseFeature = -> Pocket001
  Direction = (-1,0,0)
  Length = 0.8
  Length2 = 10
  Profile = -> Sketch010
  ReferenceAxis = -> Sketch010 [N_Axis]
  Refine = true
  SideType = 0
  Suppressed = false
  Type = 0
  Type2 = 0
FEATURE [Sketcher::SketchObject] Sketch011
  ArcFitTolerance = 1e-06
  AttachmentSupport = -> [Pad008]
  ExternalTypes = [0]
  FullyConstrained = true
  MakeInternals = false
  MapMode = 5
  Placement = pos=(37.5,0,0) rot=(0.57735,0.57735,0.57735;2.0944rad)
  _ExternalGeoVersion = 0
  sketch-geometry (3):
    g0: Circle CenterX=-7.7 CenterY=-9 CenterZ=0 NormalX=0 NormalY=0 NormalZ=1 AngleXU=0 Radius=1
    g1: Circle CenterX=-7.7 CenterY=-12 CenterZ=0 NormalX=0 NormalY=0 NormalZ=1 AngleXU=0 Radius=1
    g2: Circle CenterX=-7.7 CenterY=-27.8 CenterZ=0 NormalX=0 NormalY=0 NormalZ=1 AngleXU=0 Radius=1
  constraints (9):
    c: Diameter(g2) = 2
    c: Equal(g2,g1)
    c: Equal(g1,g0)
    c: Vertical(g2,g1)
    c: Vertical(g1,g0)
    c: Distance(g2,g-4) = 23.8
    c: Tangent(g-7,g1)
    c: Tangent(g-8,g0)
    c: Distance(g2,g-6) = 6.2
FEATURE [PartDesign::Pocket] Pocket002  label="LEDs"
  BaseFeature = -> Pad008
  Direction = (-1,0,0)
  Length = 0
  Length2 = 5
  Profile = -> Sketch011
  ReferenceAxis = -> Sketch011 [N_Axis]
  Refine = true
  SideType = 0
  Suppressed = false
  Type = 2
  Type2 = 0
FEATURE [Sketcher::SketchObject] Sketch013
  ArcFitTolerance = 1e-06
  AttachmentSupport = -> [Pocket002]
  ExternalGeometry = -> [Pocket002]
  ExternalTypes = [1,1,1]
  FullyConstrained = true
  MakeInternals = false
  MapMode = 5
  Placement = pos=(0,-1.5,3e-16) rot=(1,0,0;1.5708rad)
  _ExternalGeoVersion = 0
  expr: Constraints[10] = Spreadsheet.GPS_ant_Size + Spreadsheet.Tolerance
  sketch-geometry (12):
    g0: LineSegment StartX=13.5 StartY=-63 StartZ=0 EndX=15.9 EndY=-63 EndZ=0
    g1: LineSegment StartX=15.9 StartY=-63 StartZ=0 EndX=15.9 EndY=-58 EndZ=0
    g2: LineSegment StartX=15.9 StartY=-58 StartZ=0 EndX=10.5981 EndY=-58 EndZ=0
    g3: LineSegment StartX=31.1 StartY=-63 StartZ=0 EndX=33.5 EndY=-63 EndZ=0
    g4: LineSegment StartX=36 StartY=-58 StartZ=0 EndX=31.1 EndY=-58 EndZ=0
    g5: LineSegment StartX=31.1 StartY=-58 StartZ=0 EndX=31.1 EndY=-63 EndZ=0
    g6: LineSegment [constr] StartX=15.9 StartY=-63 StartZ=0 EndX=31.1 EndY=-63 EndZ=0
    g7: LineSegment [constr] StartX=11 StartY=-60.5 StartZ=0 EndX=36 EndY=-60.5 EndZ=0
    g8: GeomPoint [constr] X=23.5 Y=-60.5 Z=0
    g9: GeomPoint [constr] X=23.5 Y=-63 Z=0
    g10: LineSegment StartX=36 StartY=-60.5 StartZ=0 EndX=36 EndY=-58 EndZ=0
    g11: ArcOfCircle CenterX=8 CenterY=-59.5 CenterZ=0 NormalX=0 NormalY=0 NormalZ=1 AngleXU=0 Radius=3 StartAngle=1.7e-15 EndAngle=0.523599
  constraints (28):
    c: Coincident(g0,g1)
    c: Coincident(g1,g2)
    c: Horizontal(g0)
    c: Horizontal(g2)
    c: Vertical(g1)
    c: Coincident(g4,g5)
    c: Coincident(g5,g3)
    c: Horizontal(g3)
    c: Horizontal(g4)
    c: Vertical(g5)
    c: DistanceX(g0,g3) = 15.2
    c: Horizontal(g1,g4)
    c: DistanceY(g0,g2) = 5
    c: Coincident(g6,g0)
    c: Coincident(g6,g3)
    c: Coincident(g7,g-5)
    c: Symmetric(g7,g7,g8)
    c: Symmetric(g6,g6,g9)
    c: Vertical(g9,g8)
    c: Coincident(g-6,g3)
    c: PointOnObject(g4,g-5)
    c: Coincident(g7,g10)
    c: Coincident(g4,g10)
    c: Coincident(g-4,g0)
    c: Coincident(g11,g-3)
    c: Coincident(g11,g-8)
    c: Coincident(g2,g11)
    c: Coincident(g7,g-8)
FEATURE [Sketcher::SketchObject] Sketch019
  ArcFitTolerance = 1e-06
  AttachmentSupport = -> [Pocket002]
  ExternalTypes = [0]
  FullyConstrained = true
  MakeInternals = false
  MapMode = 5
  Placement = pos=(37.5,0,0) rot=(0.57735,0.57735,0.57735;2.0944rad)
  _ExternalGeoVersion = 0
  sketch-geometry (16):
    g0: LineSegment [constr] StartX=-8.87 StartY=-19.65 StartZ=0 EndX=-8.87 EndY=-33.45 EndZ=0
    g1: LineSegment StartX=-10.37 StartY=-36.95 StartZ=0 EndX=-7.37 EndY=-36.95 EndZ=0
    g2: LineSegment StartX=-6.37 StartY=-35.95 StartZ=0 EndX=-6.37 EndY=-30.95 EndZ=0
    g3: LineSegment StartX=-7.37 StartY=-29.95 StartZ=0 EndX=-10.37 EndY=-29.95 EndZ=0
    g4: LineSegment StartX=-11.37 StartY=-30.95 StartZ=0 EndX=-11.37 EndY=-35.95 EndZ=0
    g5: GeomPoint [constr] X=-8.87 Y=-33.45 Z=0
    g6: LineSegment [constr] StartX=-10.67 StartY=-22.87 StartZ=0 EndX=-7.07 EndY=-16.43 EndZ=0
    g7: GeomPoint X=-8.87 Y=-19.65 Z=0
    g8: ArcOfCircle CenterX=-10.37 CenterY=-30.95 CenterZ=0 NormalX=0 NormalY=0 NormalZ=1 AngleXU=0 Radius=1 StartAngle=1.5708 EndAngle=3.14159
    g9: GeomPoint [constr] X=-11.37 Y=-29.95 Z=0
    g10: ArcOfCircle CenterX=-7.37 CenterY=-30.95 CenterZ=0 NormalX=0 NormalY=0 NormalZ=1 AngleXU=0 Radius=1 StartAngle=0 EndAngle=1.5708
    g11: GeomPoint [constr] X=-6.37 Y=-29.95 Z=0
    g12: ArcOfCircle CenterX=-7.37 CenterY=-35.95 CenterZ=0 NormalX=0 NormalY=0 NormalZ=1 AngleXU=0 Radius=1 StartAngle=4.71239 EndAngle=6.28319
    g13: GeomPoint [constr] X=-6.37 Y=-36.95 Z=0
    g14: ArcOfCircle CenterX=-10.37 CenterY=-35.95 CenterZ=0 NormalX=0 NormalY=0 NormalZ=1 AngleXU=0 Radius=1 StartAngle=3.14159 EndAngle=4.71239
    g15: GeomPoint [constr] X=-11.37 Y=-36.95 Z=0
  constraints (34):
    c: Vertical(g0)
    c: Horizontal(g1)
    c: Horizontal(g3)
    c: Vertical(g2)
    c: Vertical(g4)
    c: Symmetric(g11,g15,g5)
    c: Distance(g13,g15) = 5
    c: Distance(g15,g9) = 7
    c: Coincident(g6,g-3)
    c: Coincident(g6,g-4)
    c: Symmetric(g6,g6,g7)
    c: Coincident(g0,g7)
    c: Coincident(g5,g0)
    c: DistanceY(g0,g0) = 13.8
    c: PointOnObject(g9,g3)
    c: PointOnObject(g9,g4)
    c: Tangent(g3,g8) = -1.5708
    c: Tangent(g4,g8) = -1.5708
    c: PointOnObject(g11,g3)
    c: PointOnObject(g11,g2)
    c: Tangent(g3,g10) = -1.5708
    c: Tangent(g2,g10) = -1.5708
    c: PointOnObject(g13,g2)
    c: PointOnObject(g13,g1)
    c: Tangent(g2,g12) = -1.5708
    c: Tangent(g1,g12) = -1.5708
    c: PointOnObject(g15,g1)
    c: PointOnObject(g15,g4)
    c: Tangent(g1,g14) = -1.5708
    c: Tangent(g4,g14) = -1.5708
    c: Equal(g14,g12)
    c: Equal(g12,g10)
    c: Equal(g10,g8)
    c: Radius(g8) = 1
FEATURE [PartDesign::Pocket] Pocket004  label="ON-OFF hole"
  BaseFeature = -> Pocket002
  Direction = (-1,0,0)
  Length = 5
  Length2 = 5
  Profile = -> Sketch019
  ReferenceAxis = -> Sketch019 [N_Axis]
  Refine = true
  SideType = 0
  Suppressed = false
  Type = 2
  Type2 = 0
FEATURE [PartDesign::Pad] Pad010  label="GPS antenna"
  BaseFeature = -> Pocket004
  Direction = (0,-1,2e-16)
  Length = 15
  Length2 = 10
  Profile = -> Sketch013
  ReferenceAxis = -> Sketch013 [N_Axis]
  Refine = true
  SideType = 0
  Suppressed = false
  Type = 3
  Type2 = 0
  UpToFace = -> Pocket004 [Face35]
  expr: Length = Spreadsheet.GPS_ant_Size
FEATURE [Sketcher::SketchObject] Sketch028
  ArcFitTolerance = 1e-06
  AttachmentSupport = -> [Pocket004]
  ExternalTypes = [0]
  FullyConstrained = true
  MakeInternals = false
  MapMode = 5
  Placement = pos=(0,0,0) rot=(0,0.707107,0.707107;3.14159rad)
  _ExternalGeoVersion = 0
  expr: Constraints[34] = Spreadsheet.Wall + 3
  sketch-geometry (15):
    g0: LineSegment StartX=-15 StartY=53.5 StartZ=0 EndX=-15 EndY=43.5 EndZ=0
    g1: LineSegment StartX=-15 StartY=43.5 StartZ=0 EndX=15 EndY=43.5 EndZ=0
    g2: LineSegment StartX=15 StartY=43.5 StartZ=0 EndX=15 EndY=53.5 EndZ=0
    g3: LineSegment StartX=15 StartY=53.5 StartZ=0 EndX=-15 EndY=53.5 EndZ=0
    g4: GeomPoint [constr] X=0 Y=48.5 Z=0
    g5: LineSegment StartX=-15 StartY=-53.5 StartZ=0 EndX=15 EndY=-53.5 EndZ=0
    g6: LineSegment StartX=15 StartY=-53.5 StartZ=0 EndX=15 EndY=-43.5 EndZ=0
    g7: LineSegment StartX=15 StartY=-43.5 StartZ=0 EndX=-15 EndY=-43.5 EndZ=0
    g8: LineSegment StartX=-15 StartY=-43.5 StartZ=0 EndX=-15 EndY=-53.5 EndZ=0
    g9: GeomPoint [constr] X=0 Y=-48.5 Z=0
    g10: LineSegment StartX=-2.5 StartY=-43.5 StartZ=0 EndX=2.5 EndY=-43.5 EndZ=0
    g11: LineSegment StartX=2.5 StartY=-43.5 StartZ=0 EndX=2.5 EndY=43.5 EndZ=0
    g12: LineSegment StartX=2.5 StartY=43.5 StartZ=0 EndX=-2.5 EndY=43.5 EndZ=0
    g13: LineSegment StartX=-2.5 StartY=43.5 StartZ=0 EndX=-2.5 EndY=-43.5 EndZ=0
    g14: GeomPoint [constr] X=0 Y=0 Z=0
  constraints (38):
    c: Coincident(g0,g1)
    c: Coincident(g1,g2)
    c: Coincident(g2,g3)
    c: Coincident(g3,g0)
    c: Vertical(g0)
    c: Vertical(g2)
    c: Horizontal(g1)
    c: Horizontal(g3)
    c: Symmetric(g2,g0,g4)
    c: PointOnObject(g4,g-2)
    c: Coincident(g5,g6)
    c: Coincident(g6,g7)
    c: Coincident(g7,g8)
    c: Coincident(g8,g5)
    c: Horizontal(g5)
    c: Horizontal(g7)
    c: Vertical(g6)
    c: Vertical(g8)
    c: Symmetric(g7,g5,g9)
    c: PointOnObject(g9,g-2)
    c: Coincident(g10,g11)
    c: Coincident(g11,g12)
    c: Coincident(g12,g13)
    c: Coincident(g13,g10)
    c: Horizontal(g10)
    c: Horizontal(g12)
    c: Vertical(g11)
    c: Vertical(g13)
    c: Symmetric(g12,g10,g14)
    c: Coincident(g14,g-1)
    c: PointOnObject(g11,g1)
    c: PointOnObject(g10,g7)
    c: Equal(g7,g1)
    c: Equal(g2,g6)
    c: Distance(g3,g-3) = 4.5
    c: DistanceY(g2,g2) = 10
    c: DistanceX(g3,g3) = 30
    c: Distance(g11,g12) = 5
FEATURE [PartDesign::Pocket] Pocket007  label="solar Pocket"
  BaseFeature = -> Pad010
  Direction = (0,-1,2e-16)
  Length = 0.5
  Length2 = 5
  Profile = -> Sketch028
  ReferenceAxis = -> Sketch028 [N_Axis]
  Refine = true
  SideType = 0
  Suppressed = false
  Type = 0
  Type2 = 0
FEATURE [Sketcher::SketchObject] Sketch050
  ArcFitTolerance = 1e-06
  AttachmentSupport = -> [Pocket007]
  ExternalGeometry = -> [Pocket007]
  ExternalTypes = [0,0,0]
  FullyConstrained = true
  MakeInternals = false
  MapMode = 5
  Placement = pos=(0,-1.5,3e-16) rot=(1,0,0;1.5708rad)
  _ExternalGeoVersion = 1
  sketch-geometry (3):
    g0: LineSegment StartX=15 StartY=53.5 StartZ=0 EndX=-36 EndY=53.5 EndZ=0
    g1: LineSegment StartX=-36 StartY=53.5 StartZ=0 EndX=-36 EndY=43.5 EndZ=0
    g2: LineSegment StartX=-36 StartY=43.5 StartZ=0 EndX=15 EndY=43.5 EndZ=0
  constraints (8):
    c: Coincident(g-4,g0)
    c: Horizontal(g0)
    c: Coincident(g0,g1)
    c: Vertical(g1)
    c: Coincident(g1,g2)
    c: Coincident(g2,g-4)
    c: Horizontal(g2)
    c: PointOnObject(g0,g-5)
FEATURE [PartDesign::Pocket] Pocket018
  BaseFeature = -> Pocket007
  Direction = (0,1,-2e-16)
  Length = 5
  Length2 = 5
  Profile = -> Sketch050
  ReferenceAxis = -> Sketch050 [N_Axis]
  Refine = true
  SideType = 0
  Suppressed = false
  Type = 3
  Type2 = 0
  UpToFace = -> Pocket007 [Face4]
FEATURE [App::Point] Origin120
  Role = Origin
FEATURE [Sketcher::SketchObject] Sketch051
  ArcFitTolerance = 1e-06
  AttachmentSupport = -> [Origin119]
  ExternalTypes = [0]
  FullyConstrained = true
  MakeInternals = false
  MapMode = 5
  _ExternalGeoVersion = 1
  sketch-geometry (5):
    g0: LineSegment StartX=-35 StartY=-27.5 StartZ=0 EndX=35 EndY=-27.5 EndZ=0
    g1: LineSegment StartX=35 StartY=-27.5 StartZ=0 EndX=35 EndY=27.5 EndZ=0
    g2: LineSegment StartX=35 StartY=27.5 StartZ=0 EndX=-35 EndY=27.5 EndZ=0
    g3: LineSegment StartX=-35 StartY=27.5 StartZ=0 EndX=-35 EndY=-27.5 EndZ=0
    g4: GeomPoint [constr] X=0 Y=0 Z=0
  constraints (12):
    c: Coincident(g0,g1)
    c: Coincident(g1,g2)
    c: Coincident(g2,g3)
    c: Coincident(g3,g0)
    c: Horizontal(g0)
    c: Horizontal(g2)
    c: Vertical(g1)
    c: Vertical(g3)
    c: Symmetric(g2,g0,g4)
    c: Coincident(g4,g-1)
    c: DistanceX(g2,g2) = 70
    c: DistanceY(g3,g3) = 55
FEATURE [PartDesign::Pad] Pad029
  Direction = (0,0,1)
  Length = 9.5
  Length2 = 10
  Profile = -> Sketch051
  ReferenceAxis = -> Sketch051 [N_Axis]
  Refine = true
  SideType = 0
  Suppressed = false
  Type = 0
  Type2 = 0
FEATURE [PartDesign::Body] Body013  label="Battery 65x55x9.5-5Ah ;)"
  AllowCompound = false
  Group = -> [Sketch051,Pad029]
  Origin = -> Origin119
  Placement = pos=(0.8,-1.6,28.5) rot=(1,0,0;1.5708rad)
  Tip = -> Pad029
FEATURE [App::Point] Origin122  label="Origin123"
  Role = Origin
FEATURE [Sketcher::SketchObject] Sketch056
  ArcFitTolerance = 1e-06
  AttachmentSupport = -> [Origin121]
  ExternalTypes = [0]
  FullyConstrained = true
  MakeInternals = false
  MapMode = 5
  Placement = pos=(0,0,0) rot=(1,0,0;1.5708rad)
  _ExternalGeoVersion = 1
  sketch-geometry (5):
    g0: LineSegment StartX=-35 StartY=-27.5 StartZ=0 EndX=35 EndY=-27.5 EndZ=0
    g1: LineSegment StartX=35 StartY=-27.5 StartZ=0 EndX=35 EndY=27.5 EndZ=0
    g2: LineSegment StartX=35 StartY=27.5 StartZ=0 EndX=-35 EndY=27.5 EndZ=0
    g3: LineSegment StartX=-35 StartY=27.5 StartZ=0 EndX=-35 EndY=-27.5 EndZ=0
    g4: GeomPoint [constr] X=0 Y=0 Z=0
  constraints (12):
    c: Coincident(g0,g1)
    c: Coincident(g1,g2)
    c: Coincident(g2,g3)
    c: Coincident(g3,g0)
    c: Horizontal(g0)
    c: Horizontal(g2)
    c: Vertical(g1)
    c: Vertical(g3)
    c: Symmetric(g2,g0,g4)
    c: Distance(g1,g3) = 70
    c: Distance(g0,g2) = 55
    c: Coincident(g4,g-1)
FEATURE [PartDesign::Pad] Pad035
  Direction = (0,-1,0)
  Length = 3
  Length2 = 10
  Profile = -> Sketch056
  ReferenceAxis = -> Sketch056 [N_Axis]
  Refine = true
  SideType = 0
  Suppressed = false
  Type = 0
  Type2 = 0
FEATURE [PartDesign::Body] Body014  label="3mmFoam_battery"
  AllowCompound = false
  Group = -> [Sketch056,Pad035]
  Origin = -> Origin121
  Placement = pos=(0.7,-11.1,28.3) rot=(0,0,1;0rad)
  Tip = -> Pad035
FEATURE [App::Part] Part  label="Components"
  Group = -> [MESHTASTIC_REPEATER_HANDLE_1_ASM,Body,T9_keyboard_1,T9_keyboard_002,T9_keyboard_003,T9_keyboard_004,Body004,Body005,Body003,Body006,Body013,Body011,Body014]
  Origin = -> Origin067
FEATURE [App::Part] Part001  label="case"
  Group = -> [Body002,Body007,Body010,Part__Feature1557,Body008,Body009]
  Origin = -> Origin071
FEATURE [Sketcher::SketchObject] Sketch030
  ArcFitTolerance = 1e-06
  AttachmentSupport = -> [Pocket009]
  ExternalTypes = [0]
  FullyConstrained = true
  MakeInternals = false
  MapMode = 5
  Placement = pos=(0,-2.49e-14,-56.5) rot=(0,0,1;0rad)
  _ExternalGeoVersion = 0
  expr: Constraints[7] = Spreadsheet.Wall
  sketch-geometry (3):
    g0: Circle CenterX=-25.5 CenterY=-8.5 CenterZ=0 NormalX=0 NormalY=0 NormalZ=1 AngleXU=0 Radius=3.25
    g1: LineSegment [constr] StartX=-25.5 StartY=-10 StartZ=0 EndX=-35.5 EndY=-10 EndZ=0
    g2: LineSegment [constr] StartX=-25.5 StartY=-10 StartZ=0 EndX=-25.5 EndY=-8.5 EndZ=0
  constraints (8):
    c: Diameter(g0) = 6.5
    c: Symmetric(g-3,g-3,g1)
    c: Horizontal(g1)
    c: DistanceX(g1,g1) = 10
    c: Coincident(g2,g1)
    c: Coincident(g2,g0)
    c: Vertical(g2)
    c: DistanceY(g2,g2) = 1.5
FEATURE [PartDesign::Pocket] Pocket009  label="antenna hole"
  BaseFeature = -> Pocket018
  Direction = (0,0,-1)
  Length = 5
  Length2 = 5
  Profile = -> Sketch030
  ReferenceAxis = -> Sketch030 [N_Axis]
  Refine = true
  SideType = 0
  Suppressed = false
  Type = 2
  Type2 = 0
FEATURE [Sketcher::SketchObject] Sketch031
  ArcFitTolerance = 1e-06
  AttachmentSupport = -> [Pocket009]
  ExternalGeometry = -> [Pocket009]
  ExternalTypes = [0]
  FullyConstrained = true
  MakeInternals = false
  MapMode = 5
  Placement = pos=(0,-2.49e-14,-56.5) rot=(0,0,1;0rad)
  _ExternalGeoVersion = 0
  expr: Constraints[21] = 7.9 + Spreadsheet.Tolerance
  sketch-geometry (8):
    g0: LineSegment StartX=-21.45 StartY=-6.16173 StartZ=0 EndX=-25.5 EndY=-3.82346 EndZ=0
    g1: LineSegment StartX=-25.5 StartY=-3.82346 StartZ=0 EndX=-29.55 EndY=-6.16173 EndZ=0
    g2: LineSegment StartX=-29.55 StartY=-6.16173 StartZ=0 EndX=-29.55 EndY=-10.8383 EndZ=0
    g3: LineSegment StartX=-29.55 StartY=-10.8383 StartZ=0 EndX=-25.5 EndY=-13.1765 EndZ=0
    g4: LineSegment StartX=-25.5 StartY=-13.1765 StartZ=0 EndX=-21.45 EndY=-10.8383 EndZ=0
    g5: LineSegment StartX=-21.45 StartY=-10.8383 StartZ=0 EndX=-21.45 EndY=-6.16173 EndZ=0
    g6: Circle [constr] CenterX=-25.5 CenterY=-8.5 CenterZ=0 NormalX=0 NormalY=0 NormalZ=1 AngleXU=0 Radius=4.67654
    g7: Circle CenterX=-25.5 CenterY=-8.5 CenterZ=0 NormalX=0 NormalY=0 NormalZ=1 AngleXU=0 Radius=6.67654
  constraints (18):
    c: Coincident(g0,g1)
    c: Coincident(g1,g2)
    c: Coincident(g2,g3)
    c: Coincident(g3,g4)
    c: Coincident(g4,g5)
    c: Coincident(g5,g0)
    c: Equal(g0, g1-g5) x5
    c: PointOnObject(g0,g6)
    c: PointOnObject(g1,g6)
    c: PointOnObject(g2,g6)
    c: PointOnObject(g3,g6)
    c: PointOnObject(g4,g6)
    c: PointOnObject(g5,g6)
    c: Vertical(g5)
    c: Coincident(g7,g6)
    c: Distance(g0,g7) = 2
    c: Coincident(g-3,g6)
    c: DistanceX(g2,g4) = 8.1
FEATURE [PartDesign::Pad] Pad019  label="antenna hex"
  BaseFeature = -> Pocket009
  Direction = (0,0,1)
  Length = 2
  Length2 = 10
  Profile = -> Sketch031
  ReferenceAxis = -> Sketch031 [N_Axis]
  Refine = true
  SideType = 0
  Suppressed = false
  Type = 0
  Type2 = 0
FEATURE [PartDesign::Fillet] Fillet003  label="fileting the antenna"
  Base = -> Pad019 [Face64]
  BaseFeature = -> Pad019
  Radius = 0.8
  Refine = true
  SupportTransform = false
  Suppressed = false
  UseAllEdges = false
FEATURE [Sketcher::SketchObject] Sketch034
  ArcFitTolerance = 1e-06
  AttachmentSupport = -> [Fillet003]
  ExternalTypes = [0]
  FullyConstrained = true
  MakeInternals = false
  MapMode = 5
  Placement = pos=(0,-18.5,4.4e-15) rot=(1,0,0;1.5708rad)
  _ExternalGeoVersion = 0
  expr: Constraints[12] = Spreadsheet.threeM_holes_thread
  expr: Constraints[13] = Spreadsheet.Wall
  sketch-geometry (12):
    g0: Circle CenterX=33 CenterY=53.5 CenterZ=0 NormalX=0 NormalY=0 NormalZ=1 AngleXU=0 Radius=1.35
    g1: ArcOfCircle CenterX=33 CenterY=53.5 CenterZ=0 NormalX=0 NormalY=0 NormalZ=1 AngleXU=0 Radius=2.85 StartAngle=3.14159 EndAngle=4.71239
    g2: LineSegment StartX=30.15 StartY=53.5 StartZ=0 EndX=30.15 EndY=56.5 EndZ=0
    g3: LineSegment StartX=30.15 StartY=56.5 StartZ=0 EndX=36 EndY=56.5 EndZ=0
    g4: LineSegment StartX=36 StartY=56.5 StartZ=0 EndX=36 EndY=50.65 EndZ=0
    g5: LineSegment StartX=36 StartY=50.65 StartZ=0 EndX=33 EndY=50.65 EndZ=0
    g6: Circle CenterX=-33 CenterY=53.5 CenterZ=0 NormalX=0 NormalY=0 NormalZ=1 AngleXU=0 Radius=1.35
    g7: ArcOfCircle CenterX=-33 CenterY=53.5 CenterZ=0 NormalX=0 NormalY=0 NormalZ=1 AngleXU=0 Radius=2.85 StartAngle=4.71239 EndAngle=6.28319
    g8: LineSegment StartX=-30.15 StartY=53.5 StartZ=0 EndX=-30.15 EndY=56.5 EndZ=0
    g9: LineSegment StartX=-30.15 StartY=56.5 StartZ=0 EndX=-36 EndY=56.5 EndZ=0
    g10: LineSegment StartX=-36 StartY=56.5 StartZ=0 EndX=-36 EndY=50.65 EndZ=0
    g11: LineSegment StartX=-36 StartY=50.65 StartZ=0 EndX=-33 EndY=50.65 EndZ=0
  constraints (29):
    c: Coincident(g1,g0)
    c: PointOnObject(g2,g-3)
    c: Vertical(g2)
    c: Coincident(g3,g2)
    c: Horizontal(g3)
    c: Coincident(g4,g3)
    c: PointOnObject(g4,g-4)
    c: Vertical(g4)
    c: Coincident(g5,g4)
    c: Tangent(g2,g1) = 1.5708
    c: Tangent(g5,g1) = 1.5708
    c: Horizontal(g5)
    c: Diameter(g0) = 2.7
    c: Distance(g1,g0) = 1.5
    c: DistanceY(g0,g2) = 3
    c: Equal(g2,g5)
    c: Equal(g0,g6)
    c: Symmetric(g0,g6,g-2)
    c: Equal(g1,g7)
    c: Symmetric(g1,g7,g-2)
    c: Symmetric(g1,g7,g-2)
    c: Symmetric(g2,g8,g-2)
    c: Symmetric(g2,g8,g-2)
    c: Symmetric(g3,g9,g-2)
    c: Symmetric(g3,g9,g-2)
    c: Symmetric(g4,g10,g-2)
    c: Symmetric(g4,g10,g-2)
    c: Symmetric(g5,g11,g-2)
    c: Symmetric(g5,g11,g-2)
FEATURE [PartDesign::Pad] Pad020  label="mounting holes"
  BaseFeature = -> Fillet003
  Direction = (0,-1,2e-16)
  Length = 7
  Length2 = 10
  Offset = -9.5
  Profile = -> Sketch034
  ReferenceAxis = -> Sketch034 [N_Axis]
  Refine = true
  Reversed = true
  SideType = 0
  Suppressed = false
  Type = 0
  Type2 = 0
FEATURE [Sketcher::SketchObject] Sketch035
  ArcFitTolerance = 1e-06
  AttachmentSupport = -> [Pad020]
  ExternalTypes = [0]
  FullyConstrained = true
  MakeInternals = false
  MapMode = 5
  Placement = pos=(0,-1.5,3e-16) rot=(1,0,0;1.5708rad)
  _ExternalGeoVersion = 0
  expr: Constraints[4] = Spreadsheet.threeM_holes_thread
  sketch-geometry (9):
    g0: LineSegment [constr] StartX=37.5 StartY=-19.65 StartZ=0 EndX=-20.25 EndY=-19.65 EndZ=0
    g1: GeomPoint [constr] X=-20.25 Y=-17.45 Z=0
    g2: Circle CenterX=-20.25 CenterY=-17.45 CenterZ=0 NormalX=0 NormalY=0 NormalZ=1 AngleXU=0 Radius=1.35
    g3: LineSegment StartX=-19.25 StartY=-12.2 StartZ=0 EndX=-36 EndY=-12.2 EndZ=0
    g4: LineSegment StartX=-36 StartY=-12.2 StartZ=0 EndX=-36 EndY=-22.7 EndZ=0
    g5: LineSegment StartX=-36 StartY=-22.7 StartZ=0 EndX=-19.25 EndY=-22.7 EndZ=0
    g6: GeomPoint X=-36 Y=-17.45 Z=0
    g7: ArcOfCircle CenterX=-19.25 CenterY=-17.45 CenterZ=0 NormalX=0 NormalY=0 NormalZ=1 AngleXU=0 Radius=5.25 StartAngle=4.71239 EndAngle=7.85398
    g8: GeomPoint X=-14 Y=-17.45 Z=0
  constraints (22):
    c: Symmetric(g-3,g-3,g0)
    c: Horizontal(g0)
    c: Vertical(g1,g0)
    c: Coincident(g2,g1)
    c: Diameter(g2) = 2.7
    c: PointOnObject(g3,g-5)
    c: Horizontal(g3)
    c: Coincident(g3,g4)
    c: PointOnObject(g4,g-5)
    c: Coincident(g4,g5)
    c: Horizontal(g5)
    c: Vertical(g3,g5)
    c: Symmetric(g4,g4,g6)
    c: Horizontal(g6,g1)
    c: Coincident(g7,g5)
    c: Tangent(g7,g3) = -1.5708
    c: PointOnObject(g8,g7)
    c: Horizontal(g8,g7)
    c: DistanceX(g3,g8) = 22
    c: Distance(g8,g0) = 2.2
    c: DistanceY(g5,g3) = 10.5
    c: DistanceX(g1,g7) = 1
FEATURE [PartDesign::Pad] Pad021  label="mounting holes001"
  BaseFeature = -> Chamfer005
  Direction = (0,-1,2e-16)
  Length = 17
  Length2 = 10
  Profile = -> Sketch035
  ReferenceAxis = -> Sketch035 [N_Axis]
  Refine = true
  SideType = 0
  Suppressed = false
  Type = 0
  Type2 = 0
  expr: Length = Spreadsheet.Mounting_height
FEATURE [Sketcher::SketchObject] Sketch036
  ArcFitTolerance = 1e-06
  AttachmentSupport = -> [Pad021]
  ExternalGeometry = -> [Pad021]
  ExternalTypes = [0,0,0]
  FullyConstrained = true
  MakeInternals = false
  MapMode = 5
  Placement = pos=(0,-18.5,4.4e-15) rot=(1,0,0;1.5708rad)
  _ExternalGeoVersion = 0
  expr: Constraints[0] = Spreadsheet.threeM_holes_thread
  expr: Constraints[6] = Spreadsheet.threeM_holes_thread
  sketch-geometry (17):
    g0: Circle CenterX=32.5 CenterY=-17.45 CenterZ=0 NormalX=0 NormalY=0 NormalZ=1 AngleXU=0 Radius=1.35
    g1: LineSegment StartX=32.5 StartY=-20.95 StartZ=0 EndX=36 EndY=-20.95 EndZ=0
    g2: LineSegment StartX=36 StartY=-20.95 StartZ=0 EndX=36 EndY=-7 EndZ=0
    g3: ArcOfCircle CenterX=32.5 CenterY=-17.45 CenterZ=0 NormalX=0 NormalY=0 NormalZ=1 AngleXU=0 Radius=3.5 StartAngle=3.14159 EndAngle=4.71239
    g4: Circle CenterX=32.5 CenterY=-51 CenterZ=0 NormalX=0 NormalY=0 NormalZ=1 AngleXU=0 Radius=1.35
    g5: LineSegment StartX=30.5 StartY=-48 StartZ=0 EndX=36 EndY=-48 EndZ=0
    g6: LineSegment StartX=36 StartY=-48 StartZ=0 EndX=36 EndY=-54 EndZ=0
    g7: LineSegment StartX=36 StartY=-54 StartZ=0 EndX=30.5 EndY=-54 EndZ=0
    g8: LineSegment StartX=29.5 StartY=-49 StartZ=0 EndX=29.5 EndY=-53 EndZ=0
    g9: ArcOfCircle CenterX=30.5 CenterY=-49 CenterZ=0 NormalX=0 NormalY=0 NormalZ=1 AngleXU=0 Radius=1 StartAngle=1.5708 EndAngle=3.14159
    g10: GeomPoint [constr] X=29.5 Y=-48 Z=0
    g11: ArcOfCircle CenterX=30.5 CenterY=-53 CenterZ=0 NormalX=0 NormalY=0 NormalZ=1 AngleXU=0 Radius=1 StartAngle=3.14159 EndAngle=4.71239
    g12: GeomPoint [constr] X=29.5 Y=-54 Z=0
    g13: GeomPoint X=29.5 Y=-51 Z=0
    g14: LineSegment StartX=29 StartY=-17.45 StartZ=0 EndX=29 EndY=-9 EndZ=0
    g15: LineSegment StartX=31 StartY=-7 StartZ=0 EndX=36 EndY=-7 EndZ=0
    g16: ArcOfCircle CenterX=31 CenterY=-9 CenterZ=0 NormalX=0 NormalY=0 NormalZ=1 AngleXU=0 Radius=2 StartAngle=1.5708 EndAngle=3.14159
  constraints (41):
    c: Diameter(g0) = 2.7
    c: Horizontal(g1)
    c: Coincident(g1,g2)
    c: Vertical(g2)
    c: PointOnObject(g2,g-3)
    c: Coincident(g4,g-7)
    c: Diameter(g4) = 2.7
    c: PointOnObject(g5,g-3)
    c: Horizontal(g5)
    c: PointOnObject(g6,g-3)
    c: Coincident(g7,g6)
    c: Horizontal(g7)
    c: Vertical(g10,g12)
    c: Coincident(g6,g5)
    c: PointOnObject(g10,g5)
    c: PointOnObject(g10,g8)
    c: Tangent(g5,g9) = 1.5708
    c: Tangent(g8,g9) = -1.5708
    c: PointOnObject(g12,g8)
    c: PointOnObject(g12,g7)
    c: Tangent(g8,g11) = -1.5708
    c: Tangent(g7,g11) = 1.5708
    c: Radius(g11) = 1
    c: Equal(g11,g9)
    c: Symmetric(g8,g8,g13)
    c: Horizontal(g13,g4)
    c: Distance(g4,g8) = 3
    c: DistanceY(g6,g6) = 6
    c: Coincident(g3,g0)
    c: Vertical(g-5,g0)
    c: Horizontal(g-8,g0)
    c: DistanceY(g1,g0) = 3.5
    c: Tangent(g3,g1) = -1.5708
    c: Vertical(g14)
    c: Coincident(g15,g2)
    c: Horizontal(g15)
    c: Tangent(g16,g15) = 1.5708
    c: Tangent(g16,g14) = 1.5708
    c: Tangent(g14,g3) = 1.5708
    c: Distance(g-10,g15) = 3
    c: Radius(g16) = 2
FEATURE [PartDesign::Fillet] Fillet006
  Base = -> Pad034 [Edge48,Edge52]
  BaseFeature = -> Pad034
  Radius = 2
  Refine = true
  SupportTransform = false
  Suppressed = false
  UseAllEdges = false
FEATURE [PartDesign::Pad] Pad022  label="mounting hole top"
  BaseFeature = -> Fillet006
  Direction = (0,-1,2e-16)
  Length = 7.5
  Length2 = 10
  Offset = 4
  Profile = -> Sketch036
  ReferenceAxis = -> Sketch036 [N_Axis]
  Refine = true
  Reversed = true
  SideType = 0
  Suppressed = false
  Type = 0
  Type2 = 0
FEATURE [Sketcher::SketchObject] Sketch037
  ArcFitTolerance = 1e-06
  AttachmentSupport = -> [Pad022]
  ExternalGeometry = -> [Pad022]
  ExternalTypes = [0,0,0]
  FullyConstrained = true
  MakeInternals = false
  MapMode = 5
  Placement = pos=(0,-1.5e-15,-7) rot=(0,0,1;0rad)
  _ExternalGeoVersion = 0
  sketch-geometry (3):
    g0: LineSegment StartX=29 StartY=-16.7 StartZ=0 EndX=34.7 EndY=-11 EndZ=0
    g1: LineSegment StartX=34.7 StartY=-11 StartZ=0 EndX=29 EndY=-11 EndZ=0
    g2: LineSegment StartX=29 StartY=-11 StartZ=0 EndX=29 EndY=-16.7 EndZ=0
  constraints (9):
    c: Coincident(g1,g0)
    c: Coincident(g2,g0)
    c: Horizontal(g1)
    c: Coincident(g2,g1)
    c: Vertical(g2)
    c: Angle(g1,g0) = 0.785398
    c: Distance(g0,g-5) = 0.5
    c: PointOnObject(g0,g-6)
    c: PointOnObject(g0,g-4)
FEATURE [PartDesign::Pocket] Pocket012  label="mounting hole top chamfer"
  BaseFeature = -> Pad022
  Direction = (0,0,-1)
  Length = 0
  Length2 = 5
  Profile = -> Sketch037
  ReferenceAxis = -> Sketch037 [N_Axis]
  Refine = true
  SideType = 0
  Suppressed = false
  Type = 3
  Type2 = 0
  UpToFace = -> Pad022 [Face95]
FEATURE [PartDesign::Fillet] Fillet007
  Base = -> Pocket012 [Edge166,Edge201,Edge209,Edge203]
  BaseFeature = -> Pocket012
  Radius = 1.3
  Refine = true
  SupportTransform = false
  Suppressed = false
  UseAllEdges = false
FEATURE [Sketcher::SketchObject] Sketch043
  ArcFitTolerance = 1e-06
  AttachmentSupport = -> [DatumPlane005]
  ExternalGeometry = -> [Pad023]
  ExternalTypes = [0,0,0,0,0]
  FullyConstrained = true
  MakeInternals = false
  MapMode = 5
  Placement = pos=(8,-9.25,-58) rot=(-1,0,0;1.5708rad)
  _ExternalGeoVersion = 0
  sketch-geometry (14):
    g0: LineSegment StartX=5.5 StartY=6.5 StartZ=0 EndX=8.5 EndY=6.5 EndZ=0
    g1: ArcOfCircle CenterX=6.5 CenterY=7.5 CenterZ=0 NormalX=0 NormalY=0 NormalZ=1 AngleXU=0 Radius=1 StartAngle=-4.4e-15 EndAngle=1.5708
    g2: LineSegment StartX=6.5 StartY=8.5 StartZ=0 EndX=-8 EndY=8.5 EndZ=0
    g3: ArcOfCircle CenterX=-8 CenterY=3 CenterZ=0 NormalX=0 NormalY=0 NormalZ=1 AngleXU=0 Radius=5.5 StartAngle=1.5708 EndAngle=3.14159
    g4: LineSegment StartX=-13.5 StartY=3 StartZ=0 EndX=-13.5 EndY=1 EndZ=0
    g5: ArcOfCircle CenterX=-14.5 CenterY=1 CenterZ=0 NormalX=0 NormalY=0 NormalZ=1 AngleXU=0 Radius=1 StartAngle=4.71239 EndAngle=6.28319
    g6: LineSegment StartX=1.5 StartY=6.5 StartZ=0 EndX=-8 EndY=6.5 EndZ=0
    g7: ArcOfCircle CenterX=-8 CenterY=3 CenterZ=0 NormalX=0 NormalY=0 NormalZ=1 AngleXU=0 Radius=3.5 StartAngle=1.5708 EndAngle=3.14159
    g8: LineSegment StartX=-11.5 StartY=3 StartZ=0 EndX=-11.5 EndY=1 EndZ=0
    g9: ArcOfCircle CenterX=-10.5 CenterY=1 CenterZ=0 NormalX=0 NormalY=0 NormalZ=1 AngleXU=0 Radius=1 StartAngle=3.14159 EndAngle=4.71239
    g10: LineSegment StartX=-10.5 StartY=0 StartZ=0 EndX=-14.5 EndY=-5e-16 EndZ=0
    g11: ArcOfCircle CenterX=8.5 CenterY=7.5 CenterZ=0 NormalX=0 NormalY=0 NormalZ=1 AngleXU=0 Radius=1 StartAngle=3.14159 EndAngle=4.71239
    g12: ArcOfCircle CenterX=5.5 CenterY=2.5 CenterZ=0 NormalX=0 NormalY=0 NormalZ=1 AngleXU=0 Radius=4 StartAngle=1.5708 EndAngle=2.49809
    g13: ArcOfCircle CenterX=1.5 CenterY=5.5 CenterZ=0 NormalX=0 NormalY=0 NormalZ=1 AngleXU=0 Radius=1 StartAngle=5.63968 EndAngle=7.85398
  constraints (35):
    c: Coincident(g0,g-5)
    c: PointOnObject(g0,g-4)
    c: Horizontal(g2)
    c: Tangent(g2,g3) = -1.5708
    c: Vertical(g4)
    c: Tangent(g4,g5) = 1.5708
    c: Tangent(g5,g-3) = -1.5708
    c: Tangent(g1,g2) = -1.5708
    c: Tangent(g3,g4) = -1.5708
    c: Horizontal(g6)
    c: Tangent(g6,g7) = -1.5708
    c: Vertical(g8)
    c: Tangent(g8,g9) = -1.5708
    c: Tangent(g9,g-3) = -1.5708
    c: Tangent(g7,g8) = -1.5708
    c: Distance(g0,g-1) = 6.5
    c: DistanceX(g9,g-7) = 12
    c: Tangent(g10,g9) = 1.5708
    c: Coincident(g10,g5)
    c: DistanceX(g4,g8) = 2
    c: Equal(g1,g5)
    c: Equal(g9,g5)
    c: Radius(g7) = 3.5
    c: Coincident(g7,g3)
    c: Radius(g1) = 1
    c: Tangent(g11,g0) = -1.5708
    c: Tangent(g11,g1) = 1.5708
    c: Equal(g11,g1)
    c: DistanceX(g0,g1) = 2
    c: Horizontal(g6,g0)
    c: Coincident(g12,g-5)
    c: Tangent(g13,g6) = -1.5708
    c: Tangent(g13,g12) = 1.5708
    c: Equal(g13,g1)
    c: Coincident(g0,g12)
FEATURE [PartDesign::Body] Body002  label="BASE"
  AllowCompound = false
  Group = -> [Sketch004,Pad004,Thickness,Sketch005,Pad005,Sketch006,Chamfer001,Fillet005,Chamfer004,Pocket,Sketch009,Pocket001,Sketch010,Pad008,Sketch011,Pocket002,Pocket004,Sketch013,Pad010,Sketch019,Sketch028,Pocket007,Sketch030,Sketch050,Pocket018,Pocket009,Sketch031,Pad019,Fillet003,Sketch034,Pad020,Sketch035,Chamfer005,Pad021,Sketch036,Sketch055,Pad034,Fillet006,Pad022,Sketch037,Pocket012,Sketch038,+14 more]
  Origin = -> Origin072
  Tip = -> Fillet018
FEATURE [PartDesign::Body] Body010  label="TPU protector"
  AllowCompound = false
  Group = -> [Binder006,Sketch042,Pad024,Binder007,Sketch044,Pocket015,Binder008,Sketch045,Pocket016,Fillet009,Sketch046,Pad026,Chamfer003,Sketch047,Pad027,Fillet010,Fillet011,Fillet013,Boolean,Sketch054,Pocket019]
  Origin = -> Origin082
  Tip = -> Fillet013
FEATURE [PartDesign::Body] Body012  label="base clone for bool"
  AllowCompound = false
  Group = -> [Clone]
  Origin = -> Origin084
  Tip = -> Clone
FEATURE [PartDesign::FeatureBase] Clone
  BaseFeature = -> Body002
  Suppressed = false
FEATURE [PartDesign::Boolean] Boolean
  BaseFeature = -> Fillet013
  Group = -> [Body012]
  Refine = true
  Suppressed = false
  Type = 1
FEATURE [App::Part] Part002  label="all"
  Group = -> [Part001,Part]
  Origin = -> Origin085
FEATURE [PartDesign::Chamfer] Chamfer005
  Angle = 45
  Base = -> Pad020 [Edge251,Edge223]
  BaseFeature = -> Pad020
  ChamferType = 0
  FlipDirection = false
  Refine = true
  Size = 1
  Size2 = 1
  SupportTransform = false
  Suppressed = false
  UseAllEdges = false
FEATURE [Sketcher::SketchObject] Sketch052
  ArcFitTolerance = 1e-06
  AttachmentSupport = -> [Pad033]
  ExternalTypes = [0,0,0]
  FullyConstrained = true
  MakeInternals = false
  MapMode = 5
  Placement = pos=(0,-2.7e-15,-12.2) rot=(0,0,1;0rad)
  _ExternalGeoVersion = 1
  expr: Constraints[9] = 3.5 - Spreadsheet.Tolerance
  sketch-geometry (4):
    g0: LineSegment StartX=-32.7 StartY=-18.5 StartZ=0 EndX=-32.7 EndY=-14.3 EndZ=0
    g1: LineSegment StartX=-32.7 StartY=-14.3 StartZ=0 EndX=-36 EndY=-11 EndZ=0
    g2: LineSegment StartX=-36 StartY=-11 StartZ=0 EndX=-36 EndY=-18.5 EndZ=0
    g3: LineSegment StartX=-36 StartY=-18.5 StartZ=0 EndX=-32.7 EndY=-18.5 EndZ=0
  constraints (11):
    c: PointOnObject(g0,g-4)
    c: Vertical(g0)
    c: Coincident(g0,g1)
    c: PointOnObject(g1,g-5)
    c: Coincident(g1,g2)
    c: Coincident(g2,g-5)
    c: Coincident(g2,g3)
    c: Coincident(g3,g0)
    c: DistanceY(g1,g-3) = 9.5
    c: DistanceX(g3,g3) = 3.3
    c: Angle(g2,g1) = 0.785398
FEATURE [PartDesign::Pad] Pad030  label="keyboard lid support"
  BaseFeature = -> Fillet017
  Direction = (0,0,1)
  Length = 10
  Length2 = 10
  Offset = 1
  Profile = -> Sketch052
  ReferenceAxis = -> Sketch052 [N_Axis]
  Refine = true
  SideType = 0
  Suppressed = false
  Type = 3
  Type2 = 0
  UpToFace = -> Pad033 [Face16]
FEATURE [PartDesign::Pad] Pad031  label="how not to do cad"
  BaseFeature = -> Pad030
  Direction = (0,2e-16,1)
  Length = 10
  Length2 = 10
  Profile = -> Pad030 [Face122]
  Refine = true
  SideType = 0
  Suppressed = false
  Type = 3
  Type2 = 0
  UpToFace = -> Pad030 [Face5]
FEATURE [Sketcher::SketchObject] Sketch053
  ArcFitTolerance = 1e-06
  AttachmentSupport = -> [Pad031]
  ExternalGeometry = -> [Pad031]
  ExternalTypes = [0,0,0,0,0,0]
  FullyConstrained = true
  MakeInternals = false
  MapMode = 5
  Placement = pos=(0,-1.5,3e-16) rot=(1,0,0;1.5708rad)
  _ExternalGeoVersion = 1
  sketch-geometry (10):
    g0: LineSegment StartX=-32.7 StartY=-3.2 StartZ=0 EndX=-32.7 EndY=-5.7 EndZ=0
    g1: LineSegment StartX=-29.7 StartY=-8.7 StartZ=0 EndX=-19.06 EndY=-8.7 EndZ=0
    g2: LineSegment StartX=-16.06 StartY=-5.7 StartZ=0 EndX=-16.06 EndY=-3.2 EndZ=0
    g3: LineSegment StartX=-19.06 StartY=-0.2 StartZ=0 EndX=-29.7 EndY=-0.2 EndZ=0
    g4: ArcOfCircle CenterX=-29.7 CenterY=-3.2 CenterZ=0 NormalX=0 NormalY=0 NormalZ=1 AngleXU=0 Radius=3 StartAngle=1.5708 EndAngle=3.14159
    g5: ArcOfCircle CenterX=-29.7 CenterY=-5.7 CenterZ=0 NormalX=0 NormalY=0 NormalZ=1 AngleXU=0 Radius=3 StartAngle=3.14159 EndAngle=4.71239
    g6: ArcOfCircle CenterX=-19.06 CenterY=-5.7 CenterZ=0 NormalX=0 NormalY=0 NormalZ=1 AngleXU=0 Radius=3 StartAngle=4.71239 EndAngle=6.28319
    g7: ArcOfCircle CenterX=-19.06 CenterY=-3.2 CenterZ=0 NormalX=0 NormalY=0 NormalZ=1 AngleXU=0 Radius=3 StartAngle=0 EndAngle=1.5708
    g8: GeomPoint [constr] X=-32.7 Y=-0.2 Z=0
    g9: GeomPoint [constr] X=-16.06 Y=-8.7 Z=0
  constraints (24):
    c: Tangent(g0,g4) = -1.5708
    c: Tangent(g0,g5) = -1.5708
    c: Tangent(g1,g5) = -1.5708
    c: Tangent(g1,g6) = -1.5708
    c: Tangent(g2,g6) = -1.5708
    c: Tangent(g2,g7) = -1.5708
    c: Tangent(g3,g7) = -1.5708
    c: Tangent(g3,g4) = -1.5708
    c: Vertical(g0)
    c: Vertical(g2)
    c: Horizontal(g1)
    c: Horizontal(g3)
    c: Equal(g4,g5)
    c: Equal(g5,g6)
    c: Equal(g6,g7)
    c: PointOnObject(g8,g0)
    c: PointOnObject(g8,g3)
    c: PointOnObject(g9,g1)
    c: PointOnObject(g9,g2)
    c: Distance(g1,g-6) = 3.5
    c: Radius(g5) = 3
    c: Distance(g-7,g2) = 3
    c: DistanceY(g1,g3) = 8.5
    c: PointOnObject(g0,g-8)
FEATURE [PartDesign::Pad] Pad032  label="Switches support"
  BaseFeature = -> Pad031
  Direction = (0,-1,0)
  Length = 9.3
  Length2 = 10
  Profile = -> Sketch053
  ReferenceAxis = -> Sketch053 [N_Axis]
  Refine = true
  SideType = 0
  Suppressed = false
  Type = 0
  Type2 = 0
  expr: Length = 12 - Spreadsheet.EINKfoam
FEATURE [Part::DatumPoint] DatumPoint  label="midpoint helper"
  AttacherType = Attacher::AttachEnginePoint
  AttachmentSupport = -> [Pad023]
  MapMode = 37
  Placement = pos=(8,-9.25,-58) rot=(0,0,1;0rad)
FEATURE [Part::DatumPlane] DatumPlane005  label="Midplane"
  AttachmentOffset = pos=(0,0,0) rot=(0,0,-1;1.5708rad)
  AttachmentSupport = -> [DatumPoint,Pad023]
  MapMode = 6
  Placement = pos=(8,-9.25,-58) rot=(1,0,0;4.71239rad)
FEATURE [PartDesign::Pad] Pad033  label="Hanger"
  BaseFeature = -> Pad023
  Direction = (0,1,2e-16)
  Length = 10
  Length2 = 5
  Profile = -> Sketch043
  ReferenceAxis = -> Sketch043 [N_Axis]
  Refine = true
  SideType = 2
  Suppressed = false
  Type = 0
  Type2 = 3
  UpToFace2 = -> Pad023 [Face1]
  expr: Length2 = 10 / 2
FEATURE [PartDesign::Fillet] Fillet016
  Base = -> Pad033 [Edge409,Edge416,Edge204,Edge253]
  BaseFeature = -> Pad033
  Radius = 0.8
  Refine = true
  SupportTransform = false
  Suppressed = false
  UseAllEdges = false
FEATURE [PartDesign::Fillet] Fillet017
  Base = -> Fillet016 [Edge102,Edge110,Edge106,Edge8]
  BaseFeature = -> Fillet016
  Radius = 0.8
  Refine = true
  SupportTransform = false
  Suppressed = false
  UseAllEdges = false
FEATURE [PartDesign::Fillet] Fillet018  label="SWs fillet"
  Base = -> Pad032 [Edge127]
  BaseFeature = -> Pad032
  Radius = 1
  Refine = true
  SupportTransform = false
  Suppressed = false
  UseAllEdges = false
FEATURE [Sketcher::SketchObject] Sketch054
  ArcFitTolerance = 1e-06
  AttachmentSupport = -> [Boolean]
  ExternalTypes = [0,0,0,0]
  FullyConstrained = true
  MakeInternals = false
  MapMode = 5
  Placement = pos=(-1.51124e-11,-1.72122e-11,-59.5) rot=(1,0,0;3.14159rad)
  _ExternalGeoVersion = 1
  sketch-geometry (8):
    g0: GeomPoint [constr] X=-3.5 Y=9.25 Z=0
    g1: LineSegment StartX=12.5346 StartY=8.5 StartZ=0 EndX=12.5346 EndY=10 EndZ=0
    g2: LineSegment StartX=12.5346 StartY=10 StartZ=0 EndX=-4.5 EndY=10 EndZ=0
    g3: LineSegment StartX=-4.5 StartY=10 StartZ=0 EndX=-4.5 EndY=8.5 EndZ=0
    g4: LineSegment StartX=-4.5 StartY=8.5 StartZ=0 EndX=12.5346 EndY=8.5 EndZ=0
    g5: GeomPoint [constr] X=4.01729 Y=9.25 Z=0
    g6: LineSegment [constr] StartX=-5.5 StartY=10 StartZ=0 EndX=-3.5 EndY=10 EndZ=0
    g7: LineSegment [constr] StartX=9.70312 StartY=10 StartZ=0 EndX=15.366 EndY=10 EndZ=0
  constraints (20):
    c: Symmetric(g-3,g-3,g0)
    c: Coincident(g1,g2)
    c: Coincident(g2,g3)
    c: Coincident(g3,g4)
    c: Coincident(g4,g1)
    c: Vertical(g1)
    c: Vertical(g3)
    c: Horizontal(g2)
    c: Horizontal(g4)
    c: Symmetric(g3,g1,g5)
    c: Horizontal(g0,g5)
    c: PointOnObject(g6,g-5)
    c: PointOnObject(g6,g-3)
    c: Horizontal(g6)
    c: PointOnObject(g7,g-6)
    c: PointOnObject(g7,g-4)
    c: Horizontal(g7)
    c: Symmetric(g6,g6,g2)
    c: Symmetric(g7,g7,g1)
    c: DistanceY(g3,g3) = 1.5
FEATURE [PartDesign::Pocket] Pocket019
  BaseFeature = -> Boolean
  Direction = (2.54e-13,2.891e-13,1)
  Length = 6.6
  Length2 = 5
  Profile = -> Sketch054
  ReferenceAxis = -> Sketch054 [N_Axis]
  Refine = true
  Reversed = true
  SideType = 0
  Suppressed = false
  Type = 0
  Type2 = 0
FEATURE [Sketcher::SketchObject] Sketch038
  ArcFitTolerance = 1e-06
  AttachmentSupport = -> [Pocket012]
  ExternalTypes = [0]
  FullyConstrained = true
  MakeInternals = false
  MapMode = 5
  Placement = pos=(0,-1.5,3e-16) rot=(1,0,0;1.5708rad)
  _ExternalGeoVersion = 0
  sketch-geometry (6):
    g0: LineSegment StartX=-36 StartY=-56.5 StartZ=0 EndX=-30.1373 EndY=-56.5 EndZ=0
    g1: LineSegment StartX=-30.1373 StartY=-56.5 StartZ=0 EndX=-30.1373 EndY=-50.5 EndZ=0
    g2: LineSegment StartX=-31.1373 StartY=-49.5 StartZ=0 EndX=-36 EndY=-49.5 EndZ=0
    g3: LineSegment StartX=-36 StartY=-49.5 StartZ=0 EndX=-36 EndY=-56.5 EndZ=0
    g4: ArcOfCircle CenterX=-31.1373 CenterY=-50.5 CenterZ=0 NormalX=0 NormalY=0 NormalZ=1 AngleXU=0 Radius=1 StartAngle=1.2e-15 EndAngle=1.5708
    g5: GeomPoint [constr] X=-30.1373 Y=-49.5 Z=0
  constraints (16):
    c: Coincident(g0,g1)
    c: Coincident(g2,g3)
    c: Coincident(g3,g0)
    c: Horizontal(g0)
    c: Horizontal(g2)
    c: Vertical(g1)
    c: Vertical(g3)
    c: Vertical(g0,g-3)
    c: Horizontal(g-4,g0)
    c: DistanceX(g0,g-6) = 1
    c: DistanceY(g3,g3) = 7
    c: PointOnObject(g5,g2)
    c: PointOnObject(g5,g1)
    c: Tangent(g2,g4) = -1.5708
    c: Tangent(g1,g4) = -1.5708
    c: Radius(g4) = 1
FEATURE [PartDesign::Pad] Pad023  label="Eink support"
  BaseFeature = -> Fillet007
  Direction = (0,-1,0)
  Length = 12.8
  Length2 = 10
  Profile = -> Sketch038
  ReferenceAxis = -> Sketch038 [N_Axis]
  Refine = true
  SideType = 0
  Suppressed = false
  Type = 0
  Type2 = 0
  expr: Length = 15.5 - Spreadsheet.EINKfoam
FEATURE [Sketcher::SketchObject] Sketch055
  ArcFitTolerance = 1e-06
  AttachmentSupport = -> [Pad021]
  ExternalGeometry = -> [Pad021]
  ExternalTypes = [0,0]
  FullyConstrained = true
  MakeInternals = false
  MapMode = 5
  Placement = pos=(0,-1.5,3e-16) rot=(1,0,0;1.5708rad)
  _ExternalGeoVersion = 1
  sketch-geometry (6):
    g0: LineSegment StartX=-36 StartY=-22.7 StartZ=0 EndX=-36 EndY=-29.7 EndZ=0
    g1: LineSegment StartX=-36 StartY=-29.7 StartZ=0 EndX=-26 EndY=-29.7 EndZ=0
    g2: LineSegment StartX=-24 StartY=-27.7 StartZ=0 EndX=-24 EndY=-22.7 EndZ=0
    g3: LineSegment StartX=-24 StartY=-22.7 StartZ=0 EndX=-36 EndY=-22.7 EndZ=0
    g4: ArcOfCircle CenterX=-26 CenterY=-27.7 CenterZ=0 NormalX=0 NormalY=0 NormalZ=1 AngleXU=0 Radius=2 StartAngle=4.71239 EndAngle=6.28319
    g5: GeomPoint [constr] X=-24 Y=-29.7 Z=0
  constraints (15):
    c: Coincident(g0,g1)
    c: Coincident(g2,g3)
    c: Coincident(g3,g0)
    c: Vertical(g0)
    c: Vertical(g2)
    c: Horizontal(g1)
    c: Horizontal(g3)
    c: Coincident(g0,g-4)
    c: DistanceY(g0,g0) = 7
    c: DistanceX(g3,g3) = 12
    c: PointOnObject(g5,g2)
    c: PointOnObject(g5,g1)
    c: Tangent(g2,g4) = -1.5708
    c: Tangent(g1,g4) = -1.5708
    c: Radius(g4) = 2
FEATURE [PartDesign::Pad] Pad034  label="Eink support down"
  BaseFeature = -> Pad021
  Direction = (0,-1,0)
  Length = 12.8
  Length2 = 10
  Profile = -> Sketch055
  ReferenceAxis = -> Sketch055 [N_Axis]
  Refine = true
  SideType = 0
  Suppressed = false
  Type = 0
  Type2 = 0
  expr: Length = 15.5 - Spreadsheet.EINKfoam
